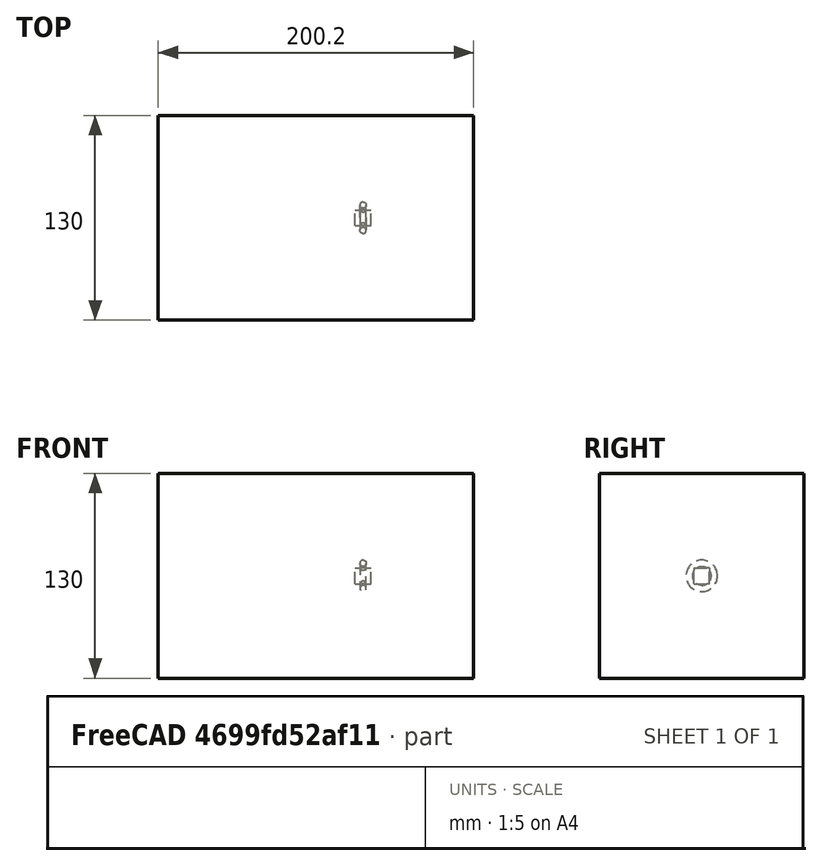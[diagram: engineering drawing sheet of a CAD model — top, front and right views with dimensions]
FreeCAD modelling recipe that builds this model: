
FCSTD DOCUMENT  (FreeCAD 0.21R33694 (Git))
Label: polarArray-7-array-rotated
License: All rights reserved
objects: App::DocumentObjectGroupPython×1251, Part::FeaturePython×4, App::Part×2, Part::MultiFuse×1
note: 4 computed .brp shape members not serialized (recipe doc carries the construction recipe); baked Part::Feature solids carry a one-line shape summary decoded from their .brp

FEATURE [App::DocumentObjectGroupPython] HALFPI  # scripted group (container) (typed FeaturePython)
  name = HALFPI
  value = pi/2.
FEATURE [App::DocumentObjectGroupPython] PI  # scripted group (container) (typed FeaturePython)
  name = PI
  value = 1.*pi
FEATURE [App::DocumentObjectGroupPython] TWOPI  # scripted group (container) (typed FeaturePython)
  name = TWOPI
  value = 2.*pi
FEATURE [App::DocumentObjectGroupPython] Constants  # scripted group (container) (typed FeaturePython)
  Group = -> [HALFPI,PI,TWOPI]
FEATURE [App::DocumentObjectGroupPython] Variables  # scripted group (container) (typed FeaturePython)
FEATURE [App::DocumentObjectGroupPython] Quantities  # scripted group (container) (typed FeaturePython)
FEATURE [App::DocumentObjectGroupPython] Isotopes  # scripted group (container) (typed FeaturePython)
FEATURE [App::DocumentObjectGroupPython] Elements  # scripted group (container) (typed FeaturePython)
FEATURE [App::DocumentObjectGroupPython] Matrix  # scripted group (container) (typed FeaturePython)
FEATURE [App::DocumentObjectGroupPython] Surfaces  # scripted group (container) (typed FeaturePython)
FEATURE [App::DocumentObjectGroupPython] Opticals  # scripted group (container) (typed FeaturePython)
  Group = -> [Matrix,Surfaces]
FEATURE [App::DocumentObjectGroupPython] G4Isotopes  # scripted group (container) (typed FeaturePython)
FEATURE [App::DocumentObjectGroupPython] H_element  # scripted group (container) (typed FeaturePython)
  Z = 1
  atom_value = 1.008
  formula = H
  name = H_element
FEATURE [App::DocumentObjectGroupPython] He_element  # scripted group (container) (typed FeaturePython)
  Z = 2
  atom_value = 4.0026
  formula = He
  name = He_element
FEATURE [App::DocumentObjectGroupPython] Li_element  # scripted group (container) (typed FeaturePython)
  Z = 3
  atom_value = 6.94
  formula = Li
  name = Li_element
FEATURE [App::DocumentObjectGroupPython] Be_element  # scripted group (container) (typed FeaturePython)
  Z = 4
  atom_value = 9.01218
  formula = Be
  name = Be_element
FEATURE [App::DocumentObjectGroupPython] B_element  # scripted group (container) (typed FeaturePython)
  Z = 5
  atom_value = 10.81
  formula = B
  name = B_element
FEATURE [App::DocumentObjectGroupPython] C_element  # scripted group (container) (typed FeaturePython)
  Z = 6
  atom_value = 12.011
  formula = C
  name = C_element
FEATURE [App::DocumentObjectGroupPython] N_element  # scripted group (container) (typed FeaturePython)
  Z = 7
  atom_value = 14.007
  formula = N
  name = N_element
FEATURE [App::DocumentObjectGroupPython] O_element  # scripted group (container) (typed FeaturePython)
  Z = 8
  atom_value = 15.999
  formula = O
  name = O_element
FEATURE [App::DocumentObjectGroupPython] F_element  # scripted group (container) (typed FeaturePython)
  Z = 9
  atom_value = 18.9984
  formula = F
  name = F_element
FEATURE [App::DocumentObjectGroupPython] Ne_element  # scripted group (container) (typed FeaturePython)
  Z = 10
  atom_value = 20.1797
  formula = Ne
  name = Ne_element
FEATURE [App::DocumentObjectGroupPython] Na_element  # scripted group (container) (typed FeaturePython)
  Z = 11
  atom_value = 22.9898
  formula = Na
  name = Na_element
FEATURE [App::DocumentObjectGroupPython] Mg_element  # scripted group (container) (typed FeaturePython)
  Z = 12
  atom_value = 24.305
  formula = Mg
  name = Mg_element
FEATURE [App::DocumentObjectGroupPython] Al_element  # scripted group (container) (typed FeaturePython)
  Z = 13
  atom_value = 26.9815
  formula = Al
  name = Al_element
FEATURE [App::DocumentObjectGroupPython] Si_element  # scripted group (container) (typed FeaturePython)
  Z = 14
  atom_value = 28.085
  formula = Si
  name = Si_element
FEATURE [App::DocumentObjectGroupPython] P_element  # scripted group (container) (typed FeaturePython)
  Z = 15
  atom_value = 30.9738
  formula = P
  name = P_element
FEATURE [App::DocumentObjectGroupPython] S_element  # scripted group (container) (typed FeaturePython)
  Z = 16
  atom_value = 32.06
  formula = S
  name = S_element
FEATURE [App::DocumentObjectGroupPython] Cl_element  # scripted group (container) (typed FeaturePython)
  Z = 17
  atom_value = 35.45
  formula = Cl
  name = Cl_element
FEATURE [App::DocumentObjectGroupPython] Ar_element  # scripted group (container) (typed FeaturePython)
  Z = 18
  atom_value = 39.95
  formula = Ar
  name = Ar_element
FEATURE [App::DocumentObjectGroupPython] K_element  # scripted group (container) (typed FeaturePython)
  Z = 19
  atom_value = 39.0983
  formula = K
  name = K_element
FEATURE [App::DocumentObjectGroupPython] Ca_element  # scripted group (container) (typed FeaturePython)
  Z = 20
  atom_value = 40.078
  formula = Ca
  name = Ca_element
FEATURE [App::DocumentObjectGroupPython] Sc_element  # scripted group (container) (typed FeaturePython)
  Z = 21
  atom_value = 44.9559
  formula = Sc
  name = Sc_element
FEATURE [App::DocumentObjectGroupPython] Ti_element  # scripted group (container) (typed FeaturePython)
  Z = 22
  atom_value = 47.867
  formula = Ti
  name = Ti_element
FEATURE [App::DocumentObjectGroupPython] V_element  # scripted group (container) (typed FeaturePython)
  Z = 23
  atom_value = 50.9415
  formula = V
  name = V_element
FEATURE [App::DocumentObjectGroupPython] Cr_element  # scripted group (container) (typed FeaturePython)
  Z = 24
  atom_value = 51.9961
  formula = Cr
  name = Cr_element
FEATURE [App::DocumentObjectGroupPython] Mn_element  # scripted group (container) (typed FeaturePython)
  Z = 25
  atom_value = 54.938
  formula = Mn
  name = Mn_element
FEATURE [App::DocumentObjectGroupPython] Fe_element  # scripted group (container) (typed FeaturePython)
  Z = 26
  atom_value = 55.845
  formula = Fe
  name = Fe_element
FEATURE [App::DocumentObjectGroupPython] Co_element  # scripted group (container) (typed FeaturePython)
  Z = 27
  atom_value = 58.9332
  formula = Co
  name = Co_element
FEATURE [App::DocumentObjectGroupPython] Ni_element  # scripted group (container) (typed FeaturePython)
  Z = 28
  atom_value = 58.6934
  formula = Ni
  name = Ni_element
FEATURE [App::DocumentObjectGroupPython] Cu_element  # scripted group (container) (typed FeaturePython)
  Z = 29
  atom_value = 63.546
  formula = Cu
  name = Cu_element
FEATURE [App::DocumentObjectGroupPython] Zn_element  # scripted group (container) (typed FeaturePython)
  Z = 30
  atom_value = 65.38
  formula = Zn
  name = Zn_element
FEATURE [App::DocumentObjectGroupPython] Ga_element  # scripted group (container) (typed FeaturePython)
  Z = 31
  atom_value = 69.723
  formula = Ga
  name = Ga_element
FEATURE [App::DocumentObjectGroupPython] Ge_element  # scripted group (container) (typed FeaturePython)
  Z = 32
  atom_value = 72.63
  formula = Ge
  name = Ge_element
FEATURE [App::DocumentObjectGroupPython] As_element  # scripted group (container) (typed FeaturePython)
  Z = 33
  atom_value = 74.9216
  formula = As
  name = As_element
FEATURE [App::DocumentObjectGroupPython] Se_element  # scripted group (container) (typed FeaturePython)
  Z = 34
  atom_value = 78.971
  formula = Se
  name = Se_element
FEATURE [App::DocumentObjectGroupPython] Br_element  # scripted group (container) (typed FeaturePython)
  Z = 35
  atom_value = 79.904
  formula = Br
  name = Br_element
FEATURE [App::DocumentObjectGroupPython] Kr_element  # scripted group (container) (typed FeaturePython)
  Z = 36
  atom_value = 83.798
  formula = Kr
  name = Kr_element
FEATURE [App::DocumentObjectGroupPython] Rb_element  # scripted group (container) (typed FeaturePython)
  Z = 37
  atom_value = 85.4678
  formula = Rb
  name = Rb_element
FEATURE [App::DocumentObjectGroupPython] Sr_element  # scripted group (container) (typed FeaturePython)
  Z = 38
  atom_value = 87.62
  formula = Sr
  name = Sr_element
FEATURE [App::DocumentObjectGroupPython] Y_element  # scripted group (container) (typed FeaturePython)
  Z = 39
  atom_value = 88.9058
  formula = Y
  name = Y_element
FEATURE [App::DocumentObjectGroupPython] Zr_element  # scripted group (container) (typed FeaturePython)
  Z = 40
  atom_value = 91.224
  formula = Zr
  name = Zr_element
FEATURE [App::DocumentObjectGroupPython] Nb_element  # scripted group (container) (typed FeaturePython)
  Z = 41
  atom_value = 92.9064
  formula = Nb
  name = Nb_element
FEATURE [App::DocumentObjectGroupPython] Mo_element  # scripted group (container) (typed FeaturePython)
  Z = 42
  atom_value = 95.95
  formula = Mo
  name = Mo_element
FEATURE [App::DocumentObjectGroupPython] Tc_element  # scripted group (container) (typed FeaturePython)
  Z = 43
  atom_value = 97
  formula = Tc
  name = Tc_element
FEATURE [App::DocumentObjectGroupPython] Ru_element  # scripted group (container) (typed FeaturePython)
  Z = 44
  atom_value = 101.07
  formula = Ru
  name = Ru_element
FEATURE [App::DocumentObjectGroupPython] Rh_element  # scripted group (container) (typed FeaturePython)
  Z = 45
  atom_value = 102.905
  formula = Rh
  name = Rh_element
FEATURE [App::DocumentObjectGroupPython] Pd_element  # scripted group (container) (typed FeaturePython)
  Z = 46
  atom_value = 106.42
  formula = Pd
  name = Pd_element
FEATURE [App::DocumentObjectGroupPython] Ag_element  # scripted group (container) (typed FeaturePython)
  Z = 47
  atom_value = 107.868
  formula = Ag
  name = Ag_element
FEATURE [App::DocumentObjectGroupPython] Cd_element  # scripted group (container) (typed FeaturePython)
  Z = 48
  atom_value = 112.414
  formula = Cd
  name = Cd_element
FEATURE [App::DocumentObjectGroupPython] In_element  # scripted group (container) (typed FeaturePython)
  Z = 49
  atom_value = 114.818
  formula = In
  name = In_element
FEATURE [App::DocumentObjectGroupPython] Sn_element  # scripted group (container) (typed FeaturePython)
  Z = 50
  atom_value = 118.71
  formula = Sn
  name = Sn_element
FEATURE [App::DocumentObjectGroupPython] Sb_element  # scripted group (container) (typed FeaturePython)
  Z = 51
  atom_value = 121.76
  formula = Sb
  name = Sb_element
FEATURE [App::DocumentObjectGroupPython] Te_element  # scripted group (container) (typed FeaturePython)
  Z = 52
  atom_value = 127.6
  formula = Te
  name = Te_element
FEATURE [App::DocumentObjectGroupPython] I_element  # scripted group (container) (typed FeaturePython)
  Z = 53
  atom_value = 126.904
  formula = I
  name = I_element
FEATURE [App::DocumentObjectGroupPython] Xe_element  # scripted group (container) (typed FeaturePython)
  Z = 54
  atom_value = 131.293
  formula = Xe
  name = Xe_element
FEATURE [App::DocumentObjectGroupPython] Cs_element  # scripted group (container) (typed FeaturePython)
  Z = 55
  atom_value = 132.905
  formula = Cs
  name = Cs_element
FEATURE [App::DocumentObjectGroupPython] Ba_element  # scripted group (container) (typed FeaturePython)
  Z = 56
  atom_value = 137.327
  formula = Ba
  name = Ba_element
FEATURE [App::DocumentObjectGroupPython] La_element  # scripted group (container) (typed FeaturePython)
  Z = 57
  atom_value = 138.905
  formula = La
  name = La_element
FEATURE [App::DocumentObjectGroupPython] Ce_element  # scripted group (container) (typed FeaturePython)
  Z = 58
  atom_value = 140.116
  formula = Ce
  name = Ce_element
FEATURE [App::DocumentObjectGroupPython] Pr_element  # scripted group (container) (typed FeaturePython)
  Z = 59
  atom_value = 140.908
  formula = Pr
  name = Pr_element
FEATURE [App::DocumentObjectGroupPython] Nd_element  # scripted group (container) (typed FeaturePython)
  Z = 60
  atom_value = 144.242
  formula = Nd
  name = Nd_element
FEATURE [App::DocumentObjectGroupPython] Pm_element  # scripted group (container) (typed FeaturePython)
  Z = 61
  atom_value = 145
  formula = Pm
  name = Pm_element
FEATURE [App::DocumentObjectGroupPython] Sm_element  # scripted group (container) (typed FeaturePython)
  Z = 62
  atom_value = 150.36
  formula = Sm
  name = Sm_element
FEATURE [App::DocumentObjectGroupPython] Eu_element  # scripted group (container) (typed FeaturePython)
  Z = 63
  atom_value = 151.964
  formula = Eu
  name = Eu_element
FEATURE [App::DocumentObjectGroupPython] Gd_element  # scripted group (container) (typed FeaturePython)
  Z = 64
  atom_value = 157.25
  formula = Gd
  name = Gd_element
FEATURE [App::DocumentObjectGroupPython] Tb_element  # scripted group (container) (typed FeaturePython)
  Z = 65
  atom_value = 158.925
  formula = Tb
  name = Tb_element
FEATURE [App::DocumentObjectGroupPython] Dy_element  # scripted group (container) (typed FeaturePython)
  Z = 66
  atom_value = 162.5
  formula = Dy
  name = Dy_element
FEATURE [App::DocumentObjectGroupPython] Ho_element  # scripted group (container) (typed FeaturePython)
  Z = 67
  atom_value = 164.93
  formula = Ho
  name = Ho_element
FEATURE [App::DocumentObjectGroupPython] Er_element  # scripted group (container) (typed FeaturePython)
  Z = 68
  atom_value = 167.259
  formula = Er
  name = Er_element
FEATURE [App::DocumentObjectGroupPython] Tm_element  # scripted group (container) (typed FeaturePython)
  Z = 69
  atom_value = 168.934
  formula = Tm
  name = Tm_element
FEATURE [App::DocumentObjectGroupPython] Yb_element  # scripted group (container) (typed FeaturePython)
  Z = 70
  atom_value = 173.045
  formula = Yb
  name = Yb_element
FEATURE [App::DocumentObjectGroupPython] Lu_element  # scripted group (container) (typed FeaturePython)
  Z = 71
  atom_value = 174.967
  formula = Lu
  name = Lu_element
FEATURE [App::DocumentObjectGroupPython] Hf_element  # scripted group (container) (typed FeaturePython)
  Z = 72
  atom_value = 178.49
  formula = Hf
  name = Hf_element
FEATURE [App::DocumentObjectGroupPython] Ta_element  # scripted group (container) (typed FeaturePython)
  Z = 73
  atom_value = 180.948
  formula = Ta
  name = Ta_element
FEATURE [App::DocumentObjectGroupPython] W_element  # scripted group (container) (typed FeaturePython)
  Z = 74
  atom_value = 183.84
  formula = W
  name = W_element
FEATURE [App::DocumentObjectGroupPython] Re_element  # scripted group (container) (typed FeaturePython)
  Z = 75
  atom_value = 186.207
  formula = Re
  name = Re_element
FEATURE [App::DocumentObjectGroupPython] Os_element  # scripted group (container) (typed FeaturePython)
  Z = 76
  atom_value = 190.23
  formula = Os
  name = Os_element
FEATURE [App::DocumentObjectGroupPython] Ir_element  # scripted group (container) (typed FeaturePython)
  Z = 77
  atom_value = 192.217
  formula = Ir
  name = Ir_element
FEATURE [App::DocumentObjectGroupPython] Pt_element  # scripted group (container) (typed FeaturePython)
  Z = 78
  atom_value = 195.084
  formula = Pt
  name = Pt_element
FEATURE [App::DocumentObjectGroupPython] Au_element  # scripted group (container) (typed FeaturePython)
  Z = 79
  atom_value = 196.967
  formula = Au
  name = Au_element
FEATURE [App::DocumentObjectGroupPython] Hg_element  # scripted group (container) (typed FeaturePython)
  Z = 80
  atom_value = 200.592
  formula = Hg
  name = Hg_element
FEATURE [App::DocumentObjectGroupPython] Tl_element  # scripted group (container) (typed FeaturePython)
  Z = 81
  atom_value = 204.38
  formula = Tl
  name = Tl_element
FEATURE [App::DocumentObjectGroupPython] Pb_element  # scripted group (container) (typed FeaturePython)
  Z = 82
  atom_value = 207.2
  formula = Pb
  name = Pb_element
FEATURE [App::DocumentObjectGroupPython] Bi_element  # scripted group (container) (typed FeaturePython)
  Z = 83
  atom_value = 208.98
  formula = Bi
  name = Bi_element
FEATURE [App::DocumentObjectGroupPython] Po_element  # scripted group (container) (typed FeaturePython)
  Z = 84
  atom_value = 209
  formula = Po
  name = Po_element
FEATURE [App::DocumentObjectGroupPython] At_element  # scripted group (container) (typed FeaturePython)
  Z = 85
  atom_value = 210
  formula = At
  name = At_element
FEATURE [App::DocumentObjectGroupPython] Rn_element  # scripted group (container) (typed FeaturePython)
  Z = 86
  atom_value = 222
  formula = Rn
  name = Rn_element
FEATURE [App::DocumentObjectGroupPython] Fr_element  # scripted group (container) (typed FeaturePython)
  Z = 87
  atom_value = 223
  formula = Fr
  name = Fr_element
FEATURE [App::DocumentObjectGroupPython] Ra_element  # scripted group (container) (typed FeaturePython)
  Z = 88
  atom_value = 226
  formula = Ra
  name = Ra_element
FEATURE [App::DocumentObjectGroupPython] Ac_element  # scripted group (container) (typed FeaturePython)
  Z = 89
  atom_value = 227
  formula = Ac
  name = Ac_element
FEATURE [App::DocumentObjectGroupPython] Th_element  # scripted group (container) (typed FeaturePython)
  Z = 90
  atom_value = 232.038
  formula = Th
  name = Th_element
FEATURE [App::DocumentObjectGroupPython] Pa_element  # scripted group (container) (typed FeaturePython)
  Z = 91
  atom_value = 231.036
  formula = Pa
  name = Pa_element
FEATURE [App::DocumentObjectGroupPython] U_element  # scripted group (container) (typed FeaturePython)
  Z = 92
  atom_value = 238.029
  formula = U
  name = U_element
FEATURE [App::DocumentObjectGroupPython] Np_element  # scripted group (container) (typed FeaturePython)
  Z = 93
  atom_value = 237
  formula = Np
  name = Np_element
FEATURE [App::DocumentObjectGroupPython] Pu_element  # scripted group (container) (typed FeaturePython)
  Z = 94
  atom_value = 244
  formula = Pu
  name = Pu_element
FEATURE [App::DocumentObjectGroupPython] Am_element  # scripted group (container) (typed FeaturePython)
  Z = 95
  atom_value = 243
  formula = Am
  name = Am_element
FEATURE [App::DocumentObjectGroupPython] Cm_element  # scripted group (container) (typed FeaturePython)
  Z = 96
  atom_value = 247
  formula = Cm
  name = Cm_element
FEATURE [App::DocumentObjectGroupPython] Bk_element  # scripted group (container) (typed FeaturePython)
  Z = 97
  atom_value = 247
  formula = Bk
  name = Bk_element
FEATURE [App::DocumentObjectGroupPython] Cf_element  # scripted group (container) (typed FeaturePython)
  Z = 98
  atom_value = 251
  formula = Cf
  name = Cf_element
FEATURE [App::DocumentObjectGroupPython] G4Elements  # scripted group (container) (typed FeaturePython)
  Group = -> [H_element,He_element,Li_element,Be_element,B_element,C_element,N_element,O_element,F_element,Ne_element,Na_element,Mg_element,Al_element,Si_element,P_element,S_element,Cl_element,Ar_element,K_element,Ca_element,Sc_element,Ti_element,V_element,Cr_element,Mn_element,Fe_element,Co_element,Ni_element,Cu_element,Zn_element,Ga_element,Ge_element,As_element,Se_element,Br_element,Kr_element,Rb_element,+61 more]
FEATURE [App::DocumentObjectGroupPython] H_element001  label="H_element : 0.101"  # scripted group (container) (typed FeaturePython)
  n = 0.101327
FEATURE [App::DocumentObjectGroupPython] C_element001  label="C_element : 0.775"  # scripted group (container) (typed FeaturePython)
  n = 0.7755
FEATURE [App::DocumentObjectGroupPython] N_element001  label="N_element : 0.035"  # scripted group (container) (typed FeaturePython)
  n = 0.035057
FEATURE [App::DocumentObjectGroupPython] O_element001  label="O_element : 0.052"  # scripted group (container) (typed FeaturePython)
  n = 0.0523159
FEATURE [App::DocumentObjectGroupPython] F_element001  label="F_element : 0.017"  # scripted group (container) (typed FeaturePython)
  n = 0.017422
FEATURE [App::DocumentObjectGroupPython] Ca_element001  label="Ca_element : 0.018"  # scripted group (container) (typed FeaturePython)
  n = 0.018378
FEATURE [App::DocumentObjectGroupPython] G4_A_150_TISSUE  label="G4_A-150_TISSUE"  # scripted group (container) (typed FeaturePython)
  Dunit = g/cm3
  Dvalue = 1.127
  Group = -> [H_element001,C_element001,N_element001,O_element001,F_element001,Ca_element001]
  conduct = 2
  density = 1
  expand = 3
  formula = G4_A-150_TISSUE
  name = G4_A-150_TISSUE
  specific = 4
FEATURE [App::DocumentObjectGroupPython] C_element002  label="C_element : 3"  # scripted group (container) (typed FeaturePython)
  n = 3
  ref = C_element
FEATURE [App::DocumentObjectGroupPython] H_element002  label="H_element : 6"  # scripted group (container) (typed FeaturePython)
  n = 6
  ref = H_element
FEATURE [App::DocumentObjectGroupPython] O_element002  label="O_element : 1"  # scripted group (container) (typed FeaturePython)
  n = 1
  ref = O_element
FEATURE [App::DocumentObjectGroupPython] G4_ACETONE  # scripted group (container) (typed FeaturePython)
  Dunit = g/cm3
  Dvalue = 0.7899
  Group = -> [C_element002,H_element002,O_element002]
  conduct = 2
  density = 1
  expand = 3
  formula = G4_ACETONE
  name = G4_ACETONE
  specific = 4
FEATURE [App::DocumentObjectGroupPython] C_element003  label="C_element : 2"  # scripted group (container) (typed FeaturePython)
  n = 2
  ref = C_element
FEATURE [App::DocumentObjectGroupPython] H_element003  label="H_element : 2"  # scripted group (container) (typed FeaturePython)
  n = 2
  ref = H_element
FEATURE [App::DocumentObjectGroupPython] G4_ACETYLENE  # scripted group (container) (typed FeaturePython)
  Dunit = g/cm3
  Dvalue = 0.0010967
  Group = -> [C_element003,H_element003]
  conduct = 2
  density = 1
  expand = 3
  formula = G4_ACETYLENE
  name = G4_ACETYLENE
  specific = 4
FEATURE [App::DocumentObjectGroupPython] C_element004  label="C_element : 5"  # scripted group (container) (typed FeaturePython)
  n = 5
  ref = C_element
FEATURE [App::DocumentObjectGroupPython] H_element004  label="H_element : 5"  # scripted group (container) (typed FeaturePython)
  n = 5
  ref = H_element
FEATURE [App::DocumentObjectGroupPython] N_element002  label="N_element : 5"  # scripted group (container) (typed FeaturePython)
  n = 5
  ref = N_element
FEATURE [App::DocumentObjectGroupPython] G4_ADENINE  # scripted group (container) (typed FeaturePython)
  Dunit = g/cm3
  Dvalue = 1.6
  Group = -> [C_element004,H_element004,N_element002]
  conduct = 2
  density = 1
  expand = 3
  formula = G4_ADENINE
  name = G4_ADENINE
  specific = 4
FEATURE [App::DocumentObjectGroupPython] H_element005  label="H_element : 0.114"  # scripted group (container) (typed FeaturePython)
  n = 0.114
FEATURE [App::DocumentObjectGroupPython] C_element005  label="C_element : 0.598"  # scripted group (container) (typed FeaturePython)
  n = 0.598
FEATURE [App::DocumentObjectGroupPython] N_element003  label="N_element : 0.007"  # scripted group (container) (typed FeaturePython)
  n = 0.007
FEATURE [App::DocumentObjectGroupPython] O_element003  label="O_element : 0.278"  # scripted group (container) (typed FeaturePython)
  n = 0.278
FEATURE [App::DocumentObjectGroupPython] Na_element001  label="Na_element : 0.001"  # scripted group (container) (typed FeaturePython)
  n = 0.001
FEATURE [App::DocumentObjectGroupPython] S_element001  label="S_element : 0.001"  # scripted group (container) (typed FeaturePython)
  n = 0.001
FEATURE [App::DocumentObjectGroupPython] Cl_element001  label="Cl_element : 0.001"  # scripted group (container) (typed FeaturePython)
  n = 0.001
FEATURE [App::DocumentObjectGroupPython] G4_ADIPOSE_TISSUE_ICRP  # scripted group (container) (typed FeaturePython)
  Dunit = g/cm3
  Dvalue = 0.95
  Group = -> [H_element005,C_element005,N_element003,O_element003,Na_element001,S_element001,Cl_element001]
  conduct = 2
  density = 1
  expand = 3
  formula = G4_ADIPOSE_TISSUE_ICRP
  name = G4_ADIPOSE_TISSUE_ICRP
  specific = 4
FEATURE [App::DocumentObjectGroupPython] C_element006  label="C_element : 0.000"  # scripted group (container) (typed FeaturePython)
  n = 0.000124
FEATURE [App::DocumentObjectGroupPython] N_element004  label="N_element : 0.755"  # scripted group (container) (typed FeaturePython)
  n = 0.755268
FEATURE [App::DocumentObjectGroupPython] O_element004  label="O_element : 0.232"  # scripted group (container) (typed FeaturePython)
  n = 0.231781
FEATURE [App::DocumentObjectGroupPython] Ar_element001  label="Ar_element : 0.013"  # scripted group (container) (typed FeaturePython)
  n = 0.012827
FEATURE [App::DocumentObjectGroupPython] G4_AIR  # scripted group (container) (typed FeaturePython)
  Dunit = g/cm3
  Dvalue = 0.00120479
  Group = -> [C_element006,N_element004,O_element004,Ar_element001]
  conduct = 2
  density = 1
  expand = 3
  formula = G4_AIR
  name = G4_AIR
  specific = 4
FEATURE [App::DocumentObjectGroupPython] C_element007  label="C_element : 006"  # scripted group (container) (typed FeaturePython)
  n = 3
  ref = C_element
FEATURE [App::DocumentObjectGroupPython] H_element006  label="H_element : 7"  # scripted group (container) (typed FeaturePython)
  n = 7
  ref = H_element
FEATURE [App::DocumentObjectGroupPython] N_element005  label="N_element : 1"  # scripted group (container) (typed FeaturePython)
  n = 1
  ref = N_element
FEATURE [App::DocumentObjectGroupPython] O_element005  label="O_element : 2"  # scripted group (container) (typed FeaturePython)
  n = 2
  ref = O_element
FEATURE [App::DocumentObjectGroupPython] G4_ALANINE  # scripted group (container) (typed FeaturePython)
  Dunit = g/cm3
  Dvalue = 1.42
  Group = -> [C_element007,H_element006,N_element005,O_element005]
  conduct = 2
  density = 1
  expand = 3
  formula = G4_ALANINE
  name = G4_ALANINE
  specific = 4
FEATURE [App::DocumentObjectGroupPython] Al_element001  label="Al_element : 2"  # scripted group (container) (typed FeaturePython)
  n = 2
  ref = Al_element
FEATURE [App::DocumentObjectGroupPython] O_element006  label="O_element : 3"  # scripted group (container) (typed FeaturePython)
  n = 3
  ref = O_element
FEATURE [App::DocumentObjectGroupPython] G4_ALUMINUM_OXIDE  # scripted group (container) (typed FeaturePython)
  Dunit = g/cm3
  Dvalue = 3.97
  Group = -> [Al_element001,O_element006]
  conduct = 2
  density = 1
  expand = 3
  formula = G4_ALUMINUM_OXIDE
  name = G4_ALUMINUM_OXIDE
  specific = 4
FEATURE [App::DocumentObjectGroupPython] H_element007  label="H_element : 0.106"  # scripted group (container) (typed FeaturePython)
  n = 0.10593
FEATURE [App::DocumentObjectGroupPython] C_element008  label="C_element : 0.789"  # scripted group (container) (typed FeaturePython)
  n = 0.788974
FEATURE [App::DocumentObjectGroupPython] O_element007  label="O_element : 0.105"  # scripted group (container) (typed FeaturePython)
  n = 0.105096
FEATURE [App::DocumentObjectGroupPython] G4_AMBER  # scripted group (container) (typed FeaturePython)
  Dunit = g/cm3
  Dvalue = 1.1
  Group = -> [H_element007,C_element008,O_element007]
  conduct = 2
  density = 1
  expand = 3
  formula = G4_AMBER
  name = G4_AMBER
  specific = 4
FEATURE [App::DocumentObjectGroupPython] N_element006  label="N_element : 006"  # scripted group (container) (typed FeaturePython)
  n = 1
  ref = N_element
FEATURE [App::DocumentObjectGroupPython] H_element008  label="H_element : 3"  # scripted group (container) (typed FeaturePython)
  n = 3
  ref = H_element
FEATURE [App::DocumentObjectGroupPython] G4_AMMONIA  # scripted group (container) (typed FeaturePython)
  Dunit = g/cm3
  Dvalue = 0.000826019
  Group = -> [N_element006,H_element008]
  conduct = 2
  density = 1
  expand = 3
  formula = G4_AMMONIA
  name = G4_AMMONIA
  specific = 4
FEATURE [App::DocumentObjectGroupPython] C_element009  label="C_element : 6"  # scripted group (container) (typed FeaturePython)
  n = 6
  ref = C_element
FEATURE [App::DocumentObjectGroupPython] H_element009  label="H_element : 008"  # scripted group (container) (typed FeaturePython)
  n = 7
  ref = H_element
FEATURE [App::DocumentObjectGroupPython] N_element007  label="N_element : 007"  # scripted group (container) (typed FeaturePython)
  n = 1
  ref = N_element
FEATURE [App::DocumentObjectGroupPython] G4_ANILINE  # scripted group (container) (typed FeaturePython)
  Dunit = g/cm3
  Dvalue = 1.0235
  Group = -> [C_element009,H_element009,N_element007]
  conduct = 2
  density = 1
  expand = 3
  formula = G4_ANILINE
  name = G4_ANILINE
  specific = 4
FEATURE [App::DocumentObjectGroupPython] C_element010  label="C_element : 14"  # scripted group (container) (typed FeaturePython)
  n = 14
  ref = C_element
FEATURE [App::DocumentObjectGroupPython] H_element010  label="H_element : 10"  # scripted group (container) (typed FeaturePython)
  n = 10
  ref = H_element
FEATURE [App::DocumentObjectGroupPython] G4_ANTHRACENE  # scripted group (container) (typed FeaturePython)
  Dunit = g/cm3
  Dvalue = 1.283
  Group = -> [C_element010,H_element010]
  conduct = 2
  density = 1
  expand = 3
  formula = G4_ANTHRACENE
  name = G4_ANTHRACENE
  specific = 4
FEATURE [App::DocumentObjectGroupPython] H_element011  label="H_element : 0.065"  # scripted group (container) (typed FeaturePython)
  n = 0.0654709
FEATURE [App::DocumentObjectGroupPython] C_element011  label="C_element : 0.537"  # scripted group (container) (typed FeaturePython)
  n = 0.536944
FEATURE [App::DocumentObjectGroupPython] N_element008  label="N_element : 0.021"  # scripted group (container) (typed FeaturePython)
  n = 0.0215
FEATURE [App::DocumentObjectGroupPython] O_element008  label="O_element : 0.032"  # scripted group (container) (typed FeaturePython)
  n = 0.032085
FEATURE [App::DocumentObjectGroupPython] F_element002  label="F_element : 0.167"  # scripted group (container) (typed FeaturePython)
  n = 0.167411
FEATURE [App::DocumentObjectGroupPython] Ca_element002  label="Ca_element : 0.177"  # scripted group (container) (typed FeaturePython)
  n = 0.176589
FEATURE [App::DocumentObjectGroupPython] G4_B_100_BONE  label="G4_B-100_BONE"  # scripted group (container) (typed FeaturePython)
  Dunit = g/cm3
  Dvalue = 1.45
  Group = -> [H_element011,C_element011,N_element008,O_element008,F_element002,Ca_element002]
  conduct = 2
  density = 1
  expand = 3
  formula = G4_B-100_BONE
  name = G4_B-100_BONE
  specific = 4
FEATURE [App::DocumentObjectGroupPython] H_element012  label="H_element : 0.057"  # scripted group (container) (typed FeaturePython)
  n = 0.057441
FEATURE [App::DocumentObjectGroupPython] C_element012  label="C_element : 0.790"  # scripted group (container) (typed FeaturePython)
  n = 0.774591
FEATURE [App::DocumentObjectGroupPython] O_element009  label="O_element : 0.168"  # scripted group (container) (typed FeaturePython)
  n = 0.167968
FEATURE [App::DocumentObjectGroupPython] G4_BAKELITE  # scripted group (container) (typed FeaturePython)
  Dunit = g/cm3
  Dvalue = 1.25
  Group = -> [H_element012,C_element012,O_element009]
  conduct = 2
  density = 1
  expand = 3
  formula = G4_BAKELITE
  name = G4_BAKELITE
  specific = 4
FEATURE [App::DocumentObjectGroupPython] Ba_element001  label="Ba_element : 1"  # scripted group (container) (typed FeaturePython)
  n = 1
  ref = Ba_element
FEATURE [App::DocumentObjectGroupPython] F_element003  label="F_element : 2"  # scripted group (container) (typed FeaturePython)
  n = 2
  ref = F_element
FEATURE [App::DocumentObjectGroupPython] G4_BARIUM_FLUORIDE  # scripted group (container) (typed FeaturePython)
  Dunit = g/cm3
  Dvalue = 4.89
  Group = -> [Ba_element001,F_element003]
  conduct = 2
  density = 1
  expand = 3
  formula = G4_BARIUM_FLUORIDE
  name = G4_BARIUM_FLUORIDE
  specific = 4
FEATURE [App::DocumentObjectGroupPython] Ba_element002  label="Ba_element : 002"  # scripted group (container) (typed FeaturePython)
  n = 1
  ref = Ba_element
FEATURE [App::DocumentObjectGroupPython] S_element002  label="S_element : 1"  # scripted group (container) (typed FeaturePython)
  n = 1
  ref = S_element
FEATURE [App::DocumentObjectGroupPython] O_element010  label="O_element : 4"  # scripted group (container) (typed FeaturePython)
  n = 4
  ref = O_element
FEATURE [App::DocumentObjectGroupPython] G4_BARIUM_SULFATE  # scripted group (container) (typed FeaturePython)
  Dunit = g/cm3
  Dvalue = 4.5
  Group = -> [Ba_element002,S_element002,O_element010]
  conduct = 2
  density = 1
  expand = 3
  formula = G4_BARIUM_SULFATE
  name = G4_BARIUM_SULFATE
  specific = 4
FEATURE [App::DocumentObjectGroupPython] C_element013  label="C_element : 007"  # scripted group (container) (typed FeaturePython)
  n = 6
  ref = C_element
FEATURE [App::DocumentObjectGroupPython] H_element013  label="H_element : 009"  # scripted group (container) (typed FeaturePython)
  n = 6
  ref = H_element
FEATURE [App::DocumentObjectGroupPython] G4_BENZENE  # scripted group (container) (typed FeaturePython)
  Dunit = g/cm3
  Dvalue = 0.87865
  Group = -> [C_element013,H_element013]
  conduct = 2
  density = 1
  expand = 3
  formula = G4_BENZENE
  name = G4_BENZENE
  specific = 4
FEATURE [App::DocumentObjectGroupPython] Be_element001  label="Be_element : 1"  # scripted group (container) (typed FeaturePython)
  n = 1
  ref = Be_element
FEATURE [App::DocumentObjectGroupPython] O_element011  label="O_element : 005"  # scripted group (container) (typed FeaturePython)
  n = 1
  ref = O_element
FEATURE [App::DocumentObjectGroupPython] G4_BERYLLIUM_OXIDE  # scripted group (container) (typed FeaturePython)
  Dunit = g/cm3
  Dvalue = 3.01
  Group = -> [Be_element001,O_element011]
  conduct = 2
  density = 1
  expand = 3
  formula = G4_BERYLLIUM_OXIDE
  name = G4_BERYLLIUM_OXIDE
  specific = 4
FEATURE [App::DocumentObjectGroupPython] Bi_element001  label="Bi_element : 4"  # scripted group (container) (typed FeaturePython)
  n = 4
  ref = Bi_element
FEATURE [App::DocumentObjectGroupPython] Ge_element001  label="Ge_element : 3"  # scripted group (container) (typed FeaturePython)
  n = 3
  ref = Ge_element
FEATURE [App::DocumentObjectGroupPython] O_element012  label="O_element : 12"  # scripted group (container) (typed FeaturePython)
  n = 12
  ref = O_element
FEATURE [App::DocumentObjectGroupPython] G4_BGO  # scripted group (container) (typed FeaturePython)
  Dunit = g/cm3
  Dvalue = 7.13
  Group = -> [Bi_element001,Ge_element001,O_element012]
  conduct = 2
  density = 1
  expand = 3
  formula = G4_BGO
  name = G4_BGO
  specific = 4
FEATURE [App::DocumentObjectGroupPython] H_element014  label="H_element : 0.102"  # scripted group (container) (typed FeaturePython)
  n = 0.102
FEATURE [App::DocumentObjectGroupPython] C_element014  label="C_element : 0.110"  # scripted group (container) (typed FeaturePython)
  n = 0.11
FEATURE [App::DocumentObjectGroupPython] N_element009  label="N_element : 0.033"  # scripted group (container) (typed FeaturePython)
  n = 0.033
FEATURE [App::DocumentObjectGroupPython] O_element013  label="O_element : 0.745"  # scripted group (container) (typed FeaturePython)
  n = 0.745
FEATURE [App::DocumentObjectGroupPython] Na_element002  label="Na_element : 0.002"  # scripted group (container) (typed FeaturePython)
  n = 0.001
FEATURE [App::DocumentObjectGroupPython] P_element001  label="P_element : 0.001"  # scripted group (container) (typed FeaturePython)
  n = 0.001
FEATURE [App::DocumentObjectGroupPython] S_element003  label="S_element : 0.002"  # scripted group (container) (typed FeaturePython)
  n = 0.002
FEATURE [App::DocumentObjectGroupPython] Cl_element002  label="Cl_element : 0.003"  # scripted group (container) (typed FeaturePython)
  n = 0.003
FEATURE [App::DocumentObjectGroupPython] K_element001  label="K_element : 0.002"  # scripted group (container) (typed FeaturePython)
  n = 0.002
FEATURE [App::DocumentObjectGroupPython] Fe_element001  label="Fe_element : 0.001"  # scripted group (container) (typed FeaturePython)
  n = 0.001
FEATURE [App::DocumentObjectGroupPython] G4_BLOOD_ICRP  # scripted group (container) (typed FeaturePython)
  Dunit = g/cm3
  Dvalue = 1.06
  Group = -> [H_element014,C_element014,N_element009,O_element013,Na_element002,P_element001,S_element003,Cl_element002,K_element001,Fe_element001]
  conduct = 2
  density = 1
  expand = 3
  formula = G4_BLOOD_ICRP
  name = G4_BLOOD_ICRP
  specific = 4
FEATURE [App::DocumentObjectGroupPython] H_element015  label="H_element : 0.064"  # scripted group (container) (typed FeaturePython)
  n = 0.064
FEATURE [App::DocumentObjectGroupPython] C_element015  label="C_element : 0.278"  # scripted group (container) (typed FeaturePython)
  n = 0.278
FEATURE [App::DocumentObjectGroupPython] N_element010  label="N_element : 0.027"  # scripted group (container) (typed FeaturePython)
  n = 0.027
FEATURE [App::DocumentObjectGroupPython] O_element014  label="O_element : 0.410"  # scripted group (container) (typed FeaturePython)
  n = 0.41
FEATURE [App::DocumentObjectGroupPython] Mg_element001  label="Mg_element : 0.002"  # scripted group (container) (typed FeaturePython)
  n = 0.002
FEATURE [App::DocumentObjectGroupPython] P_element002  label="P_element : 0.070"  # scripted group (container) (typed FeaturePython)
  n = 0.07
FEATURE [App::DocumentObjectGroupPython] S_element004  label="S_element : 0.003"  # scripted group (container) (typed FeaturePython)
  n = 0.002
FEATURE [App::DocumentObjectGroupPython] Ca_element003  label="Ca_element : 0.147"  # scripted group (container) (typed FeaturePython)
  n = 0.147
FEATURE [App::DocumentObjectGroupPython] G4_BONE_COMPACT_ICRU  # scripted group (container) (typed FeaturePython)
  Dunit = g/cm3
  Dvalue = 1.85
  Group = -> [H_element015,C_element015,N_element010,O_element014,Mg_element001,P_element002,S_element004,Ca_element003]
  conduct = 2
  density = 1
  expand = 3
  formula = G4_BONE_COMPACT_ICRU
  name = G4_BONE_COMPACT_ICRU
  specific = 4
FEATURE [App::DocumentObjectGroupPython] H_element016  label="H_element : 0.034"  # scripted group (container) (typed FeaturePython)
  n = 0.034
FEATURE [App::DocumentObjectGroupPython] C_element016  label="C_element : 0.155"  # scripted group (container) (typed FeaturePython)
  n = 0.155
FEATURE [App::DocumentObjectGroupPython] N_element011  label="N_element : 0.042"  # scripted group (container) (typed FeaturePython)
  n = 0.042
FEATURE [App::DocumentObjectGroupPython] O_element015  label="O_element : 0.435"  # scripted group (container) (typed FeaturePython)
  n = 0.435
FEATURE [App::DocumentObjectGroupPython] Na_element003  label="Na_element : 0.003"  # scripted group (container) (typed FeaturePython)
  n = 0.001
FEATURE [App::DocumentObjectGroupPython] Mg_element002  label="Mg_element : 0.003"  # scripted group (container) (typed FeaturePython)
  n = 0.002
FEATURE [App::DocumentObjectGroupPython] P_element003  label="P_element : 0.103"  # scripted group (container) (typed FeaturePython)
  n = 0.103
FEATURE [App::DocumentObjectGroupPython] S_element005  label="S_element : 0.004"  # scripted group (container) (typed FeaturePython)
  n = 0.003
FEATURE [App::DocumentObjectGroupPython] Ca_element004  label="Ca_element : 0.225"  # scripted group (container) (typed FeaturePython)
  n = 0.225
FEATURE [App::DocumentObjectGroupPython] G4_BONE_CORTICAL_ICRP  # scripted group (container) (typed FeaturePython)
  Dunit = g/cm3
  Dvalue = 1.92
  Group = -> [H_element016,C_element016,N_element011,O_element015,Na_element003,Mg_element002,P_element003,S_element005,Ca_element004]
  conduct = 2
  density = 1
  expand = 3
  formula = G4_BONE_CORTICAL_ICRP
  name = G4_BONE_CORTICAL_ICRP
  specific = 4
FEATURE [App::DocumentObjectGroupPython] B_element001  label="B_element : 4"  # scripted group (container) (typed FeaturePython)
  n = 4
  ref = B_element
FEATURE [App::DocumentObjectGroupPython] C_element017  label="C_element : 1"  # scripted group (container) (typed FeaturePython)
  n = 1
  ref = C_element
FEATURE [App::DocumentObjectGroupPython] G4_BORON_CARBIDE  # scripted group (container) (typed FeaturePython)
  Dunit = g/cm3
  Dvalue = 2.52
  Group = -> [B_element001,C_element017]
  conduct = 2
  density = 1
  expand = 3
  formula = G4_BORON_CARBIDE
  name = G4_BORON_CARBIDE
  specific = 4
FEATURE [App::DocumentObjectGroupPython] B_element002  label="B_element : 2"  # scripted group (container) (typed FeaturePython)
  n = 2
  ref = B_element
FEATURE [App::DocumentObjectGroupPython] O_element016  label="O_element : 006"  # scripted group (container) (typed FeaturePython)
  n = 3
  ref = O_element
FEATURE [App::DocumentObjectGroupPython] G4_BORON_OXIDE  # scripted group (container) (typed FeaturePython)
  Dunit = g/cm3
  Dvalue = 1.812
  Group = -> [B_element002,O_element016]
  conduct = 2
  density = 1
  expand = 3
  formula = G4_BORON_OXIDE
  name = G4_BORON_OXIDE
  specific = 4
FEATURE [App::DocumentObjectGroupPython] H_element017  label="H_element : 0.107"  # scripted group (container) (typed FeaturePython)
  n = 0.107
FEATURE [App::DocumentObjectGroupPython] C_element018  label="C_element : 0.145"  # scripted group (container) (typed FeaturePython)
  n = 0.145
FEATURE [App::DocumentObjectGroupPython] N_element012  label="N_element : 0.022"  # scripted group (container) (typed FeaturePython)
  n = 0.022
FEATURE [App::DocumentObjectGroupPython] O_element017  label="O_element : 0.712"  # scripted group (container) (typed FeaturePython)
  n = 0.712
FEATURE [App::DocumentObjectGroupPython] Na_element004  label="Na_element : 0.004"  # scripted group (container) (typed FeaturePython)
  n = 0.002
FEATURE [App::DocumentObjectGroupPython] P_element004  label="P_element : 0.004"  # scripted group (container) (typed FeaturePython)
  n = 0.004
FEATURE [App::DocumentObjectGroupPython] S_element006  label="S_element : 0.005"  # scripted group (container) (typed FeaturePython)
  n = 0.002
FEATURE [App::DocumentObjectGroupPython] Cl_element003  label="Cl_element : 0.004"  # scripted group (container) (typed FeaturePython)
  n = 0.003
FEATURE [App::DocumentObjectGroupPython] K_element002  label="K_element : 0.003"  # scripted group (container) (typed FeaturePython)
  n = 0.003
FEATURE [App::DocumentObjectGroupPython] G4_BRAIN_ICRP  # scripted group (container) (typed FeaturePython)
  Dunit = g/cm3
  Dvalue = 1.04
  Group = -> [H_element017,C_element018,N_element012,O_element017,Na_element004,P_element004,S_element006,Cl_element003,K_element002]
  conduct = 2
  density = 1
  expand = 3
  formula = G4_BRAIN_ICRP
  name = G4_BRAIN_ICRP
  specific = 4
FEATURE [App::DocumentObjectGroupPython] C_element019  label="C_element : 4"  # scripted group (container) (typed FeaturePython)
  n = 4
  ref = C_element
FEATURE [App::DocumentObjectGroupPython] H_element018  label="H_element : 010"  # scripted group (container) (typed FeaturePython)
  n = 10
  ref = H_element
FEATURE [App::DocumentObjectGroupPython] G4_BUTANE  # scripted group (container) (typed FeaturePython)
  Dunit = g/cm3
  Dvalue = 0.00249343
  Group = -> [C_element019,H_element018]
  conduct = 2
  density = 1
  expand = 3
  formula = G4_BUTANE
  name = G4_BUTANE
  specific = 4
FEATURE [App::DocumentObjectGroupPython] C_element020  label="C_element : 008"  # scripted group (container) (typed FeaturePython)
  n = 4
  ref = C_element
FEATURE [App::DocumentObjectGroupPython] H_element019  label="H_element : 011"  # scripted group (container) (typed FeaturePython)
  n = 10
  ref = H_element
FEATURE [App::DocumentObjectGroupPython] O_element018  label="O_element : 007"  # scripted group (container) (typed FeaturePython)
  n = 1
  ref = O_element
FEATURE [App::DocumentObjectGroupPython] G4_N_BUTYL_ALCOHOL  label="G4_N-BUTYL_ALCOHOL"  # scripted group (container) (typed FeaturePython)
  Dunit = g/cm3
  Dvalue = 0.8098
  Group = -> [C_element020,H_element019,O_element018]
  conduct = 2
  density = 1
  expand = 3
  formula = G4_N-BUTYL_ALCOHOL
  name = G4_N-BUTYL_ALCOHOL
  specific = 4
FEATURE [App::DocumentObjectGroupPython] H_element020  label="H_element : 0.025"  # scripted group (container) (typed FeaturePython)
  n = 0.02468
FEATURE [App::DocumentObjectGroupPython] C_element021  label="C_element : 0.502"  # scripted group (container) (typed FeaturePython)
  n = 0.501611
FEATURE [App::DocumentObjectGroupPython] O_element019  label="O_element : 0.005"  # scripted group (container) (typed FeaturePython)
  n = 0.004527
FEATURE [App::DocumentObjectGroupPython] F_element004  label="F_element : 0.465"  # scripted group (container) (typed FeaturePython)
  n = 0.465209
FEATURE [App::DocumentObjectGroupPython] Si_element001  label="Si_element : 0.004"  # scripted group (container) (typed FeaturePython)
  n = 0.003973
FEATURE [App::DocumentObjectGroupPython] G4_C_552  label="G4_C-552"  # scripted group (container) (typed FeaturePython)
  Dunit = g/cm3
  Dvalue = 1.76
  Group = -> [H_element020,C_element021,O_element019,F_element004,Si_element001]
  conduct = 2
  density = 1
  expand = 3
  formula = G4_C-552
  name = G4_C-552
  specific = 4
FEATURE [App::DocumentObjectGroupPython] Cd_element001  label="Cd_element : 1"  # scripted group (container) (typed FeaturePython)
  n = 1
  ref = Cd_element
FEATURE [App::DocumentObjectGroupPython] Te_element001  label="Te_element : 1"  # scripted group (container) (typed FeaturePython)
  n = 1
  ref = Te_element
FEATURE [App::DocumentObjectGroupPython] G4_CADMIUM_TELLURIDE  # scripted group (container) (typed FeaturePython)
  Dunit = g/cm3
  Dvalue = 6.2
  Group = -> [Cd_element001,Te_element001]
  conduct = 2
  density = 1
  expand = 3
  formula = G4_CADMIUM_TELLURIDE
  name = G4_CADMIUM_TELLURIDE
  specific = 4
FEATURE [App::DocumentObjectGroupPython] Cd_element002  label="Cd_element : 002"  # scripted group (container) (typed FeaturePython)
  n = 1
  ref = Cd_element
FEATURE [App::DocumentObjectGroupPython] W_element001  label="W_element : 1"  # scripted group (container) (typed FeaturePython)
  n = 1
  ref = W_element
FEATURE [App::DocumentObjectGroupPython] O_element020  label="O_element : 008"  # scripted group (container) (typed FeaturePython)
  n = 4
  ref = O_element
FEATURE [App::DocumentObjectGroupPython] G4_CADMIUM_TUNGSTATE  # scripted group (container) (typed FeaturePython)
  Dunit = g/cm3
  Dvalue = 7.9
  Group = -> [Cd_element002,W_element001,O_element020]
  conduct = 2
  density = 1
  expand = 3
  formula = G4_CADMIUM_TUNGSTATE
  name = G4_CADMIUM_TUNGSTATE
  specific = 4
FEATURE [App::DocumentObjectGroupPython] Ca_element005  label="Ca_element : 1"  # scripted group (container) (typed FeaturePython)
  n = 1
  ref = Ca_element
FEATURE [App::DocumentObjectGroupPython] C_element022  label="C_element : 009"  # scripted group (container) (typed FeaturePython)
  n = 1
  ref = C_element
FEATURE [App::DocumentObjectGroupPython] O_element021  label="O_element : 009"  # scripted group (container) (typed FeaturePython)
  n = 3
  ref = O_element
FEATURE [App::DocumentObjectGroupPython] G4_CALCIUM_CARBONATE  # scripted group (container) (typed FeaturePython)
  Dunit = g/cm3
  Dvalue = 2.8
  Group = -> [Ca_element005,C_element022,O_element021]
  conduct = 2
  density = 1
  expand = 3
  formula = G4_CALCIUM_CARBONATE
  name = G4_CALCIUM_CARBONATE
  specific = 4
FEATURE [App::DocumentObjectGroupPython] Ca_element006  label="Ca_element : 002"  # scripted group (container) (typed FeaturePython)
  n = 1
  ref = Ca_element
FEATURE [App::DocumentObjectGroupPython] F_element005  label="F_element : 003"  # scripted group (container) (typed FeaturePython)
  n = 2
  ref = F_element
FEATURE [App::DocumentObjectGroupPython] G4_CALCIUM_FLUORIDE  # scripted group (container) (typed FeaturePython)
  Dunit = g/cm3
  Dvalue = 3.18
  Group = -> [Ca_element006,F_element005]
  conduct = 2
  density = 1
  expand = 3
  formula = G4_CALCIUM_FLUORIDE
  name = G4_CALCIUM_FLUORIDE
  specific = 4
FEATURE [App::DocumentObjectGroupPython] Ca_element007  label="Ca_element : 003"  # scripted group (container) (typed FeaturePython)
  n = 1
  ref = Ca_element
FEATURE [App::DocumentObjectGroupPython] O_element022  label="O_element : 010"  # scripted group (container) (typed FeaturePython)
  n = 1
  ref = O_element
FEATURE [App::DocumentObjectGroupPython] G4_CALCIUM_OXIDE  # scripted group (container) (typed FeaturePython)
  Dunit = g/cm3
  Dvalue = 3.3
  Group = -> [Ca_element007,O_element022]
  conduct = 2
  density = 1
  expand = 3
  formula = G4_CALCIUM_OXIDE
  name = G4_CALCIUM_OXIDE
  specific = 4
FEATURE [App::DocumentObjectGroupPython] Ca_element008  label="Ca_element : 004"  # scripted group (container) (typed FeaturePython)
  n = 1
  ref = Ca_element
FEATURE [App::DocumentObjectGroupPython] S_element007  label="S_element : 002"  # scripted group (container) (typed FeaturePython)
  n = 1
  ref = S_element
FEATURE [App::DocumentObjectGroupPython] O_element023  label="O_element : 011"  # scripted group (container) (typed FeaturePython)
  n = 4
  ref = O_element
FEATURE [App::DocumentObjectGroupPython] G4_CALCIUM_SULFATE  # scripted group (container) (typed FeaturePython)
  Dunit = g/cm3
  Dvalue = 2.96
  Group = -> [Ca_element008,S_element007,O_element023]
  conduct = 2
  density = 1
  expand = 3
  formula = G4_CALCIUM_SULFATE
  name = G4_CALCIUM_SULFATE
  specific = 4
FEATURE [App::DocumentObjectGroupPython] Ca_element009  label="Ca_element : 005"  # scripted group (container) (typed FeaturePython)
  n = 1
  ref = Ca_element
FEATURE [App::DocumentObjectGroupPython] W_element002  label="W_element : 002"  # scripted group (container) (typed FeaturePython)
  n = 1
  ref = W_element
FEATURE [App::DocumentObjectGroupPython] O_element024  label="O_element : 012"  # scripted group (container) (typed FeaturePython)
  n = 4
  ref = O_element
FEATURE [App::DocumentObjectGroupPython] G4_CALCIUM_TUNGSTATE  # scripted group (container) (typed FeaturePython)
  Dunit = g/cm3
  Dvalue = 6.062
  Group = -> [Ca_element009,W_element002,O_element024]
  conduct = 2
  density = 1
  expand = 3
  formula = G4_CALCIUM_TUNGSTATE
  name = G4_CALCIUM_TUNGSTATE
  specific = 4
FEATURE [App::DocumentObjectGroupPython] C_element023  label="C_element : 010"  # scripted group (container) (typed FeaturePython)
  n = 1
  ref = C_element
FEATURE [App::DocumentObjectGroupPython] O_element025  label="O_element : 013"  # scripted group (container) (typed FeaturePython)
  n = 2
  ref = O_element
FEATURE [App::DocumentObjectGroupPython] G4_CARBON_DIOXIDE  # scripted group (container) (typed FeaturePython)
  Dunit = g/cm3
  Dvalue = 0.00184212
  Group = -> [C_element023,O_element025]
  conduct = 2
  density = 1
  expand = 3
  formula = G4_CARBON_DIOXIDE
  name = G4_CARBON_DIOXIDE
  specific = 4
FEATURE [App::DocumentObjectGroupPython] C_element024  label="C_element : 011"  # scripted group (container) (typed FeaturePython)
  n = 1
  ref = C_element
FEATURE [App::DocumentObjectGroupPython] Cl_element004  label="Cl_element : 4"  # scripted group (container) (typed FeaturePython)
  n = 4
  ref = Cl_element
FEATURE [App::DocumentObjectGroupPython] G4_CARBON_TETRACHLORIDE  # scripted group (container) (typed FeaturePython)
  Dunit = g/cm3
  Dvalue = 1.594
  Group = -> [C_element024,Cl_element004]
  conduct = 2
  density = 1
  expand = 3
  formula = G4_CARBON_TETRACHLORIDE
  name = G4_CARBON_TETRACHLORIDE
  specific = 4
FEATURE [App::DocumentObjectGroupPython] C_element025  label="C_element : 012"  # scripted group (container) (typed FeaturePython)
  n = 6
  ref = C_element
FEATURE [App::DocumentObjectGroupPython] H_element021  label="H_element : 012"  # scripted group (container) (typed FeaturePython)
  n = 10
  ref = H_element
FEATURE [App::DocumentObjectGroupPython] O_element026  label="O_element : 5"  # scripted group (container) (typed FeaturePython)
  n = 5
  ref = O_element
FEATURE [App::DocumentObjectGroupPython] G4_CELLULOSE_CELLOPHANE  # scripted group (container) (typed FeaturePython)
  Dunit = g/cm3
  Dvalue = 1.42
  Group = -> [C_element025,H_element021,O_element026]
  conduct = 2
  density = 1
  expand = 3
  formula = G4_CELLULOSE_CELLOPHANE
  name = G4_CELLULOSE_CELLOPHANE
  specific = 4
FEATURE [App::DocumentObjectGroupPython] H_element022  label="H_element : 0.067"  # scripted group (container) (typed FeaturePython)
  n = 0.067125
FEATURE [App::DocumentObjectGroupPython] C_element026  label="C_element : 0.545"  # scripted group (container) (typed FeaturePython)
  n = 0.545403
FEATURE [App::DocumentObjectGroupPython] O_element027  label="O_element : 0.387"  # scripted group (container) (typed FeaturePython)
  n = 0.387472
FEATURE [App::DocumentObjectGroupPython] G4_CELLULOSE_BUTYRATE  # scripted group (container) (typed FeaturePython)
  Dunit = g/cm3
  Dvalue = 1.2
  Group = -> [H_element022,C_element026,O_element027]
  conduct = 2
  density = 1
  expand = 3
  formula = G4_CELLULOSE_BUTYRATE
  name = G4_CELLULOSE_BUTYRATE
  specific = 4
FEATURE [App::DocumentObjectGroupPython] H_element023  label="H_element : 0.029"  # scripted group (container) (typed FeaturePython)
  n = 0.029216
FEATURE [App::DocumentObjectGroupPython] C_element027  label="C_element : 0.271"  # scripted group (container) (typed FeaturePython)
  n = 0.271296
FEATURE [App::DocumentObjectGroupPython] N_element013  label="N_element : 0.121"  # scripted group (container) (typed FeaturePython)
  n = 0.121276
FEATURE [App::DocumentObjectGroupPython] O_element028  label="O_element : 0.578"  # scripted group (container) (typed FeaturePython)
  n = 0.578212
FEATURE [App::DocumentObjectGroupPython] G4_CELLULOSE_NITRATE  # scripted group (container) (typed FeaturePython)
  Dunit = g/cm3
  Dvalue = 1.49
  Group = -> [H_element023,C_element027,N_element013,O_element028]
  conduct = 2
  density = 1
  expand = 3
  formula = G4_CELLULOSE_NITRATE
  name = G4_CELLULOSE_NITRATE
  specific = 4
FEATURE [App::DocumentObjectGroupPython] H_element024  label="H_element : 0.108"  # scripted group (container) (typed FeaturePython)
  n = 0.107596
FEATURE [App::DocumentObjectGroupPython] N_element014  label="N_element : 0.001"  # scripted group (container) (typed FeaturePython)
  n = 0.0008
FEATURE [App::DocumentObjectGroupPython] O_element029  label="O_element : 0.875"  # scripted group (container) (typed FeaturePython)
  n = 0.874976
FEATURE [App::DocumentObjectGroupPython] S_element008  label="S_element : 0.015"  # scripted group (container) (typed FeaturePython)
  n = 0.014627
FEATURE [App::DocumentObjectGroupPython] Ce_element001  label="Ce_element : 0.002"  # scripted group (container) (typed FeaturePython)
  n = 0.002001
FEATURE [App::DocumentObjectGroupPython] G4_CERIC_SULFATE  # scripted group (container) (typed FeaturePython)
  Dunit = g/cm3
  Dvalue = 1.03
  Group = -> [H_element024,N_element014,O_element029,S_element008,Ce_element001]
  conduct = 2
  density = 1
  expand = 3
  formula = G4_CERIC_SULFATE
  name = G4_CERIC_SULFATE
  specific = 4
FEATURE [App::DocumentObjectGroupPython] Cs_element001  label="Cs_element : 1"  # scripted group (container) (typed FeaturePython)
  n = 1
  ref = Cs_element
FEATURE [App::DocumentObjectGroupPython] F_element006  label="F_element : 1"  # scripted group (container) (typed FeaturePython)
  n = 1
  ref = F_element
FEATURE [App::DocumentObjectGroupPython] G4_CESIUM_FLUORIDE  # scripted group (container) (typed FeaturePython)
  Dunit = g/cm3
  Dvalue = 4.115
  Group = -> [Cs_element001,F_element006]
  conduct = 2
  density = 1
  expand = 3
  formula = G4_CESIUM_FLUORIDE
  name = G4_CESIUM_FLUORIDE
  specific = 4
FEATURE [App::DocumentObjectGroupPython] Cs_element002  label="Cs_element : 002"  # scripted group (container) (typed FeaturePython)
  n = 1
  ref = Cs_element
FEATURE [App::DocumentObjectGroupPython] I_element001  label="I_element : 1"  # scripted group (container) (typed FeaturePython)
  n = 1
  ref = I_element
FEATURE [App::DocumentObjectGroupPython] G4_CESIUM_IODIDE  # scripted group (container) (typed FeaturePython)
  Dunit = g/cm3
  Dvalue = 4.51
  Group = -> [Cs_element002,I_element001]
  conduct = 2
  density = 1
  expand = 3
  formula = G4_CESIUM_IODIDE
  name = G4_CESIUM_IODIDE
  specific = 4
FEATURE [App::DocumentObjectGroupPython] C_element028  label="C_element : 013"  # scripted group (container) (typed FeaturePython)
  n = 6
  ref = C_element
FEATURE [App::DocumentObjectGroupPython] H_element025  label="H_element : 013"  # scripted group (container) (typed FeaturePython)
  n = 5
  ref = H_element
FEATURE [App::DocumentObjectGroupPython] Cl_element005  label="Cl_element : 1"  # scripted group (container) (typed FeaturePython)
  n = 1
  ref = Cl_element
FEATURE [App::DocumentObjectGroupPython] G4_CHLOROBENZENE  # scripted group (container) (typed FeaturePython)
  Dunit = g/cm3
  Dvalue = 1.1058
  Group = -> [C_element028,H_element025,Cl_element005]
  conduct = 2
  density = 1
  expand = 3
  formula = G4_CHLOROBENZENE
  name = G4_CHLOROBENZENE
  specific = 4
FEATURE [App::DocumentObjectGroupPython] C_element029  label="C_element : 014"  # scripted group (container) (typed FeaturePython)
  n = 1
  ref = C_element
FEATURE [App::DocumentObjectGroupPython] H_element026  label="H_element : 1"  # scripted group (container) (typed FeaturePython)
  n = 1
  ref = H_element
FEATURE [App::DocumentObjectGroupPython] Cl_element006  label="Cl_element : 3"  # scripted group (container) (typed FeaturePython)
  n = 3
  ref = Cl_element
FEATURE [App::DocumentObjectGroupPython] G4_CHLOROFORM  # scripted group (container) (typed FeaturePython)
  Dunit = g/cm3
  Dvalue = 1.4832
  Group = -> [C_element029,H_element026,Cl_element006]
  conduct = 2
  density = 1
  expand = 3
  formula = G4_CHLOROFORM
  name = G4_CHLOROFORM
  specific = 4
FEATURE [App::DocumentObjectGroupPython] H_element027  label="H_element : 0.010"  # scripted group (container) (typed FeaturePython)
  n = 0.01
FEATURE [App::DocumentObjectGroupPython] C_element030  label="C_element : 0.001"  # scripted group (container) (typed FeaturePython)
  n = 0.001
FEATURE [App::DocumentObjectGroupPython] O_element030  label="O_element : 0.529"  # scripted group (container) (typed FeaturePython)
  n = 0.529107
FEATURE [App::DocumentObjectGroupPython] Na_element005  label="Na_element : 0.016"  # scripted group (container) (typed FeaturePython)
  n = 0.016
FEATURE [App::DocumentObjectGroupPython] Mg_element003  label="Mg_element : 0.004"  # scripted group (container) (typed FeaturePython)
  n = 0.002
FEATURE [App::DocumentObjectGroupPython] Al_element002  label="Al_element : 0.034"  # scripted group (container) (typed FeaturePython)
  n = 0.033872
FEATURE [App::DocumentObjectGroupPython] Si_element002  label="Si_element : 0.337"  # scripted group (container) (typed FeaturePython)
  n = 0.337021
FEATURE [App::DocumentObjectGroupPython] K_element003  label="K_element : 0.013"  # scripted group (container) (typed FeaturePython)
  n = 0.013
FEATURE [App::DocumentObjectGroupPython] Ca_element010  label="Ca_element : 0.044"  # scripted group (container) (typed FeaturePython)
  n = 0.044
FEATURE [App::DocumentObjectGroupPython] Fe_element002  label="Fe_element : 0.014"  # scripted group (container) (typed FeaturePython)
  n = 0.014
FEATURE [App::DocumentObjectGroupPython] G4_CONCRETE  # scripted group (container) (typed FeaturePython)
  Dunit = g/cm3
  Dvalue = 2.3
  Group = -> [H_element027,C_element030,O_element030,Na_element005,Mg_element003,Al_element002,Si_element002,K_element003,Ca_element010,Fe_element002]
  conduct = 2
  density = 1
  expand = 3
  formula = G4_CONCRETE
  name = G4_CONCRETE
  specific = 4
FEATURE [App::DocumentObjectGroupPython] C_element031  label="C_element : 015"  # scripted group (container) (typed FeaturePython)
  n = 6
  ref = C_element
FEATURE [App::DocumentObjectGroupPython] H_element028  label="H_element : 12"  # scripted group (container) (typed FeaturePython)
  n = 12
  ref = H_element
FEATURE [App::DocumentObjectGroupPython] G4_CYCLOHEXANE  # scripted group (container) (typed FeaturePython)
  Dunit = g/cm3
  Dvalue = 0.779
  Group = -> [C_element031,H_element028]
  conduct = 2
  density = 1
  expand = 3
  formula = G4_CYCLOHEXANE
  name = G4_CYCLOHEXANE
  specific = 4
FEATURE [App::DocumentObjectGroupPython] C_element032  label="C_element : 016"  # scripted group (container) (typed FeaturePython)
  n = 6
  ref = C_element
FEATURE [App::DocumentObjectGroupPython] H_element029  label="H_element : 4"  # scripted group (container) (typed FeaturePython)
  n = 4
  ref = H_element
FEATURE [App::DocumentObjectGroupPython] Cl_element007  label="Cl_element : 2"  # scripted group (container) (typed FeaturePython)
  n = 2
  ref = Cl_element
FEATURE [App::DocumentObjectGroupPython] G4_1_2_DICHLOROBENZENE  label="G4_1.2-DICHLOROBENZENE"  # scripted group (container) (typed FeaturePython)
  Dunit = g/cm3
  Dvalue = 1.3048
  Group = -> [C_element032,H_element029,Cl_element007]
  conduct = 2
  density = 1
  expand = 3
  formula = G4_1.2-DICHLOROBENZENE
  name = G4_1.2-DICHLOROBENZENE
  specific = 4
FEATURE [App::DocumentObjectGroupPython] C_element033  label="C_element : 017"  # scripted group (container) (typed FeaturePython)
  n = 4
  ref = C_element
FEATURE [App::DocumentObjectGroupPython] H_element030  label="H_element : 8"  # scripted group (container) (typed FeaturePython)
  n = 8
  ref = H_element
FEATURE [App::DocumentObjectGroupPython] O_element031  label="O_element : 014"  # scripted group (container) (typed FeaturePython)
  n = 1
  ref = O_element
FEATURE [App::DocumentObjectGroupPython] Cl_element008  label="Cl_element : 005"  # scripted group (container) (typed FeaturePython)
  n = 2
  ref = Cl_element
FEATURE [App::DocumentObjectGroupPython] G4_DICHLORODIETHYL_ETHER  # scripted group (container) (typed FeaturePython)
  Dunit = g/cm3
  Dvalue = 1.2199
  Group = -> [C_element033,H_element030,O_element031,Cl_element008]
  conduct = 2
  density = 1
  expand = 3
  formula = G4_DICHLORODIETHYL_ETHER
  name = G4_DICHLORODIETHYL_ETHER
  specific = 4
FEATURE [App::DocumentObjectGroupPython] C_element034  label="C_element : 018"  # scripted group (container) (typed FeaturePython)
  n = 2
  ref = C_element
FEATURE [App::DocumentObjectGroupPython] H_element031  label="H_element : 014"  # scripted group (container) (typed FeaturePython)
  n = 4
  ref = H_element
FEATURE [App::DocumentObjectGroupPython] Cl_element009  label="Cl_element : 006"  # scripted group (container) (typed FeaturePython)
  n = 2
  ref = Cl_element
FEATURE [App::DocumentObjectGroupPython] G4_1_2_DICHLOROETHANE  label="G4_1.2-DICHLOROETHANE"  # scripted group (container) (typed FeaturePython)
  Dunit = g/cm3
  Dvalue = 1.2351
  Group = -> [C_element034,H_element031,Cl_element009]
  conduct = 2
  density = 1
  expand = 3
  formula = G4_1.2-DICHLOROETHANE
  name = G4_1.2-DICHLOROETHANE
  specific = 4
FEATURE [App::DocumentObjectGroupPython] C_element035  label="C_element : 019"  # scripted group (container) (typed FeaturePython)
  n = 4
  ref = C_element
FEATURE [App::DocumentObjectGroupPython] H_element032  label="H_element : 015"  # scripted group (container) (typed FeaturePython)
  n = 10
  ref = H_element
FEATURE [App::DocumentObjectGroupPython] O_element032  label="O_element : 015"  # scripted group (container) (typed FeaturePython)
  n = 1
  ref = O_element
FEATURE [App::DocumentObjectGroupPython] G4_DIETHYL_ETHER  # scripted group (container) (typed FeaturePython)
  Dunit = g/cm3
  Dvalue = 0.71378
  Group = -> [C_element035,H_element032,O_element032]
  conduct = 2
  density = 1
  expand = 3
  formula = G4_DIETHYL_ETHER
  name = G4_DIETHYL_ETHER
  specific = 4
FEATURE [App::DocumentObjectGroupPython] C_element036  label="C_element : 020"  # scripted group (container) (typed FeaturePython)
  n = 3
  ref = C_element
FEATURE [App::DocumentObjectGroupPython] H_element033  label="H_element : 016"  # scripted group (container) (typed FeaturePython)
  n = 7
  ref = H_element
FEATURE [App::DocumentObjectGroupPython] N_element015  label="N_element : 008"  # scripted group (container) (typed FeaturePython)
  n = 1
  ref = N_element
FEATURE [App::DocumentObjectGroupPython] O_element033  label="O_element : 016"  # scripted group (container) (typed FeaturePython)
  n = 1
  ref = O_element
FEATURE [App::DocumentObjectGroupPython] G4_N_N_DIMETHYL_FORMAMIDE  label="G4_N.N-DIMETHYL_FORMAMIDE"  # scripted group (container) (typed FeaturePython)
  Dunit = g/cm3
  Dvalue = 0.9487
  Group = -> [C_element036,H_element033,N_element015,O_element033]
  conduct = 2
  density = 1
  expand = 3
  formula = G4_N.N-DIMETHYL_FORMAMIDE
  name = G4_N.N-DIMETHYL_FORMAMIDE
  specific = 4
FEATURE [App::DocumentObjectGroupPython] C_element037  label="C_element : 021"  # scripted group (container) (typed FeaturePython)
  n = 2
  ref = C_element
FEATURE [App::DocumentObjectGroupPython] H_element034  label="H_element : 017"  # scripted group (container) (typed FeaturePython)
  n = 6
  ref = H_element
FEATURE [App::DocumentObjectGroupPython] O_element034  label="O_element : 017"  # scripted group (container) (typed FeaturePython)
  n = 1
  ref = O_element
FEATURE [App::DocumentObjectGroupPython] S_element009  label="S_element : 003"  # scripted group (container) (typed FeaturePython)
  n = 1
  ref = S_element
FEATURE [App::DocumentObjectGroupPython] G4_DIMETHYL_SULFOXIDE  # scripted group (container) (typed FeaturePython)
  Dunit = g/cm3
  Dvalue = 1.1014
  Group = -> [C_element037,H_element034,O_element034,S_element009]
  conduct = 2
  density = 1
  expand = 3
  formula = G4_DIMETHYL_SULFOXIDE
  name = G4_DIMETHYL_SULFOXIDE
  specific = 4
FEATURE [App::DocumentObjectGroupPython] C_element038  label="C_element : 022"  # scripted group (container) (typed FeaturePython)
  n = 2
  ref = C_element
FEATURE [App::DocumentObjectGroupPython] H_element035  label="H_element : 018"  # scripted group (container) (typed FeaturePython)
  n = 6
  ref = H_element
FEATURE [App::DocumentObjectGroupPython] G4_ETHANE  # scripted group (container) (typed FeaturePython)
  Dunit = g/cm3
  Dvalue = 0.00125324
  Group = -> [C_element038,H_element035]
  conduct = 2
  density = 1
  expand = 3
  formula = G4_ETHANE
  name = G4_ETHANE
  specific = 4
FEATURE [App::DocumentObjectGroupPython] C_element039  label="C_element : 023"  # scripted group (container) (typed FeaturePython)
  n = 2
  ref = C_element
FEATURE [App::DocumentObjectGroupPython] H_element036  label="H_element : 019"  # scripted group (container) (typed FeaturePython)
  n = 6
  ref = H_element
FEATURE [App::DocumentObjectGroupPython] O_element035  label="O_element : 018"  # scripted group (container) (typed FeaturePython)
  n = 1
  ref = O_element
FEATURE [App::DocumentObjectGroupPython] G4_ETHYL_ALCOHOL  # scripted group (container) (typed FeaturePython)
  Dunit = g/cm3
  Dvalue = 0.7893
  Group = -> [C_element039,H_element036,O_element035]
  conduct = 2
  density = 1
  expand = 3
  formula = G4_ETHYL_ALCOHOL
  name = G4_ETHYL_ALCOHOL
  specific = 4
FEATURE [App::DocumentObjectGroupPython] H_element037  label="H_element : 0.090"  # scripted group (container) (typed FeaturePython)
  n = 0.090027
FEATURE [App::DocumentObjectGroupPython] C_element040  label="C_element : 0.585"  # scripted group (container) (typed FeaturePython)
  n = 0.585182
FEATURE [App::DocumentObjectGroupPython] O_element036  label="O_element : 0.325"  # scripted group (container) (typed FeaturePython)
  n = 0.324791
FEATURE [App::DocumentObjectGroupPython] G4_ETHYL_CELLULOSE  # scripted group (container) (typed FeaturePython)
  Dunit = g/cm3
  Dvalue = 1.13
  Group = -> [H_element037,C_element040,O_element036]
  conduct = 2
  density = 1
  expand = 3
  formula = G4_ETHYL_CELLULOSE
  name = G4_ETHYL_CELLULOSE
  specific = 4
FEATURE [App::DocumentObjectGroupPython] C_element041  label="C_element : 024"  # scripted group (container) (typed FeaturePython)
  n = 2
  ref = C_element
FEATURE [App::DocumentObjectGroupPython] H_element038  label="H_element : 020"  # scripted group (container) (typed FeaturePython)
  n = 4
  ref = H_element
FEATURE [App::DocumentObjectGroupPython] G4_ETHYLENE  # scripted group (container) (typed FeaturePython)
  Dunit = g/cm3
  Dvalue = 0.00117497
  Group = -> [C_element041,H_element038]
  conduct = 2
  density = 1
  expand = 3
  formula = G4_ETHYLENE
  name = G4_ETHYLENE
  specific = 4
FEATURE [App::DocumentObjectGroupPython] H_element039  label="H_element : 0.096"  # scripted group (container) (typed FeaturePython)
  n = 0.096
FEATURE [App::DocumentObjectGroupPython] C_element042  label="C_element : 0.195"  # scripted group (container) (typed FeaturePython)
  n = 0.195
FEATURE [App::DocumentObjectGroupPython] N_element016  label="N_element : 0.057"  # scripted group (container) (typed FeaturePython)
  n = 0.057
FEATURE [App::DocumentObjectGroupPython] O_element037  label="O_element : 0.646"  # scripted group (container) (typed FeaturePython)
  n = 0.646
FEATURE [App::DocumentObjectGroupPython] Na_element006  label="Na_element : 0.017"  # scripted group (container) (typed FeaturePython)
  n = 0.001
FEATURE [App::DocumentObjectGroupPython] P_element005  label="P_element : 0.104"  # scripted group (container) (typed FeaturePython)
  n = 0.001
FEATURE [App::DocumentObjectGroupPython] S_element010  label="S_element : 0.016"  # scripted group (container) (typed FeaturePython)
  n = 0.003
FEATURE [App::DocumentObjectGroupPython] Cl_element010  label="Cl_element : 0.005"  # scripted group (container) (typed FeaturePython)
  n = 0.001
FEATURE [App::DocumentObjectGroupPython] G4_EYE_LENS_ICRP  # scripted group (container) (typed FeaturePython)
  Dunit = g/cm3
  Dvalue = 1.07
  Group = -> [H_element039,C_element042,N_element016,O_element037,Na_element006,P_element005,S_element010,Cl_element010]
  conduct = 2
  density = 1
  expand = 3
  formula = G4_EYE_LENS_ICRP
  name = G4_EYE_LENS_ICRP
  specific = 4
FEATURE [App::DocumentObjectGroupPython] Fe_element003  label="Fe_element : 2"  # scripted group (container) (typed FeaturePython)
  n = 2
  ref = Fe_element
FEATURE [App::DocumentObjectGroupPython] O_element038  label="O_element : 019"  # scripted group (container) (typed FeaturePython)
  n = 3
  ref = O_element
FEATURE [App::DocumentObjectGroupPython] G4_FERRIC_OXIDE  # scripted group (container) (typed FeaturePython)
  Dunit = g/cm3
  Dvalue = 5.2
  Group = -> [Fe_element003,O_element038]
  conduct = 2
  density = 1
  expand = 3
  formula = G4_FERRIC_OXIDE
  name = G4_FERRIC_OXIDE
  specific = 4
FEATURE [App::DocumentObjectGroupPython] Fe_element004  label="Fe_element : 1"  # scripted group (container) (typed FeaturePython)
  n = 1
  ref = Fe_element
FEATURE [App::DocumentObjectGroupPython] B_element003  label="B_element : 1"  # scripted group (container) (typed FeaturePython)
  n = 1
  ref = B_element
FEATURE [App::DocumentObjectGroupPython] G4_FERROBORIDE  # scripted group (container) (typed FeaturePython)
  Dunit = g/cm3
  Dvalue = 7.15
  Group = -> [Fe_element004,B_element003]
  conduct = 2
  density = 1
  expand = 3
  formula = G4_FERROBORIDE
  name = G4_FERROBORIDE
  specific = 4
FEATURE [App::DocumentObjectGroupPython] Fe_element005  label="Fe_element : 003"  # scripted group (container) (typed FeaturePython)
  n = 1
  ref = Fe_element
FEATURE [App::DocumentObjectGroupPython] O_element039  label="O_element : 020"  # scripted group (container) (typed FeaturePython)
  n = 1
  ref = O_element
FEATURE [App::DocumentObjectGroupPython] G4_FERROUS_OXIDE  # scripted group (container) (typed FeaturePython)
  Dunit = g/cm3
  Dvalue = 5.7
  Group = -> [Fe_element005,O_element039]
  conduct = 2
  density = 1
  expand = 3
  formula = G4_FERROUS_OXIDE
  name = G4_FERROUS_OXIDE
  specific = 4
FEATURE [App::DocumentObjectGroupPython] H_element040  label="H_element : 0.115"  # scripted group (container) (typed FeaturePython)
  n = 0.108259
FEATURE [App::DocumentObjectGroupPython] N_element017  label="N_element : 0.000"  # scripted group (container) (typed FeaturePython)
  n = 2.7e-05
FEATURE [App::DocumentObjectGroupPython] O_element040  label="O_element : 0.879"  # scripted group (container) (typed FeaturePython)
  n = 0.878636
FEATURE [App::DocumentObjectGroupPython] Na_element007  label="Na_element : 0.000"  # scripted group (container) (typed FeaturePython)
  n = 2.2e-05
FEATURE [App::DocumentObjectGroupPython] S_element011  label="S_element : 0.013"  # scripted group (container) (typed FeaturePython)
  n = 0.012968
FEATURE [App::DocumentObjectGroupPython] Cl_element011  label="Cl_element : 0.000"  # scripted group (container) (typed FeaturePython)
  n = 3.4e-05
FEATURE [App::DocumentObjectGroupPython] Fe_element006  label="Fe_element : 0.000"  # scripted group (container) (typed FeaturePython)
  n = 5.4e-05
FEATURE [App::DocumentObjectGroupPython] G4_FERROUS_SULFATE  # scripted group (container) (typed FeaturePython)
  Dunit = g/cm3
  Dvalue = 1.024
  Group = -> [H_element040,N_element017,O_element040,Na_element007,S_element011,Cl_element011,Fe_element006]
  conduct = 2
  density = 1
  expand = 3
  formula = G4_FERROUS_SULFATE
  name = G4_FERROUS_SULFATE
  specific = 4
FEATURE [App::DocumentObjectGroupPython] C_element043  label="C_element : 0.099"  # scripted group (container) (typed FeaturePython)
  n = 0.099335
FEATURE [App::DocumentObjectGroupPython] F_element007  label="F_element : 0.314"  # scripted group (container) (typed FeaturePython)
  n = 0.314247
FEATURE [App::DocumentObjectGroupPython] Cl_element012  label="Cl_element : 0.586"  # scripted group (container) (typed FeaturePython)
  n = 0.586418
FEATURE [App::DocumentObjectGroupPython] G4_FREON_12  label="G4_FREON-12"  # scripted group (container) (typed FeaturePython)
  Dunit = g/cm3
  Dvalue = 1.12
  Group = -> [C_element043,F_element007,Cl_element012]
  conduct = 2
  density = 1
  expand = 3
  formula = G4_FREON-12
  name = G4_FREON-12
  specific = 4
FEATURE [App::DocumentObjectGroupPython] C_element044  label="C_element : 0.057"  # scripted group (container) (typed FeaturePython)
  n = 0.057245
FEATURE [App::DocumentObjectGroupPython] F_element008  label="F_element : 0.181"  # scripted group (container) (typed FeaturePython)
  n = 0.181096
FEATURE [App::DocumentObjectGroupPython] Br_element001  label="Br_element : 0.762"  # scripted group (container) (typed FeaturePython)
  n = 0.761659
FEATURE [App::DocumentObjectGroupPython] G4_FREON_12B2  label="G4_FREON-12B2"  # scripted group (container) (typed FeaturePython)
  Dunit = g/cm3
  Dvalue = 1.8
  Group = -> [C_element044,F_element008,Br_element001]
  conduct = 2
  density = 1
  expand = 3
  formula = G4_FREON-12B2
  name = G4_FREON-12B2
  specific = 4
FEATURE [App::DocumentObjectGroupPython] C_element045  label="C_element : 0.115"  # scripted group (container) (typed FeaturePython)
  n = 0.114983
FEATURE [App::DocumentObjectGroupPython] F_element009  label="F_element : 0.546"  # scripted group (container) (typed FeaturePython)
  n = 0.545621
FEATURE [App::DocumentObjectGroupPython] Cl_element013  label="Cl_element : 0.339"  # scripted group (container) (typed FeaturePython)
  n = 0.339396
FEATURE [App::DocumentObjectGroupPython] G4_FREON_13  label="G4_FREON-13"  # scripted group (container) (typed FeaturePython)
  Dunit = g/cm3
  Dvalue = 0.95
  Group = -> [C_element045,F_element009,Cl_element013]
  conduct = 2
  density = 1
  expand = 3
  formula = G4_FREON-13
  name = G4_FREON-13
  specific = 4
FEATURE [App::DocumentObjectGroupPython] C_element046  label="C_element : 025"  # scripted group (container) (typed FeaturePython)
  n = 1
  ref = C_element
FEATURE [App::DocumentObjectGroupPython] F_element010  label="F_element : 3"  # scripted group (container) (typed FeaturePython)
  n = 3
  ref = F_element
FEATURE [App::DocumentObjectGroupPython] Br_element002  label="Br_element : 1"  # scripted group (container) (typed FeaturePython)
  n = 1
  ref = Br_element
FEATURE [App::DocumentObjectGroupPython] G4_FREON_13B1  label="G4_FREON-13B1"  # scripted group (container) (typed FeaturePython)
  Dunit = g/cm3
  Dvalue = 1.5
  Group = -> [C_element046,F_element010,Br_element002]
  conduct = 2
  density = 1
  expand = 3
  formula = G4_FREON-13B1
  name = G4_FREON-13B1
  specific = 4
FEATURE [App::DocumentObjectGroupPython] C_element047  label="C_element : 0.061"  # scripted group (container) (typed FeaturePython)
  n = 0.061309
FEATURE [App::DocumentObjectGroupPython] F_element011  label="F_element : 0.291"  # scripted group (container) (typed FeaturePython)
  n = 0.290924
FEATURE [App::DocumentObjectGroupPython] I_element002  label="I_element : 0.648"  # scripted group (container) (typed FeaturePython)
  n = 0.647767
FEATURE [App::DocumentObjectGroupPython] G4_FREON_13I1  label="G4_FREON-13I1"  # scripted group (container) (typed FeaturePython)
  Dunit = g/cm3
  Dvalue = 1.8
  Group = -> [C_element047,F_element011,I_element002]
  conduct = 2
  density = 1
  expand = 3
  formula = G4_FREON-13I1
  name = G4_FREON-13I1
  specific = 4
FEATURE [App::DocumentObjectGroupPython] Gd_element001  label="Gd_element : 2"  # scripted group (container) (typed FeaturePython)
  n = 2
  ref = Gd_element
FEATURE [App::DocumentObjectGroupPython] O_element041  label="O_element : 021"  # scripted group (container) (typed FeaturePython)
  n = 2
  ref = O_element
FEATURE [App::DocumentObjectGroupPython] S_element012  label="S_element : 004"  # scripted group (container) (typed FeaturePython)
  n = 1
  ref = S_element
FEATURE [App::DocumentObjectGroupPython] G4_GADOLINIUM_OXYSULFIDE  # scripted group (container) (typed FeaturePython)
  Dunit = g/cm3
  Dvalue = 7.44
  Group = -> [Gd_element001,O_element041,S_element012]
  conduct = 2
  density = 1
  expand = 3
  formula = G4_GADOLINIUM_OXYSULFIDE
  name = G4_GADOLINIUM_OXYSULFIDE
  specific = 4
FEATURE [App::DocumentObjectGroupPython] Ga_element001  label="Ga_element : 1"  # scripted group (container) (typed FeaturePython)
  n = 1
  ref = Ga_element
FEATURE [App::DocumentObjectGroupPython] As_element001  label="As_element : 1"  # scripted group (container) (typed FeaturePython)
  n = 1
  ref = As_element
FEATURE [App::DocumentObjectGroupPython] G4_GALLIUM_ARSENIDE  # scripted group (container) (typed FeaturePython)
  Dunit = g/cm3
  Dvalue = 5.31
  Group = -> [Ga_element001,As_element001]
  conduct = 2
  density = 1
  expand = 3
  formula = G4_GALLIUM_ARSENIDE
  name = G4_GALLIUM_ARSENIDE
  specific = 4
FEATURE [App::DocumentObjectGroupPython] H_element041  label="H_element : 0.081"  # scripted group (container) (typed FeaturePython)
  n = 0.08118
FEATURE [App::DocumentObjectGroupPython] C_element048  label="C_element : 0.416"  # scripted group (container) (typed FeaturePython)
  n = 0.41606
FEATURE [App::DocumentObjectGroupPython] N_element018  label="N_element : 0.111"  # scripted group (container) (typed FeaturePython)
  n = 0.11124
FEATURE [App::DocumentObjectGroupPython] O_element042  label="O_element : 0.381"  # scripted group (container) (typed FeaturePython)
  n = 0.38064
FEATURE [App::DocumentObjectGroupPython] S_element013  label="S_element : 0.011"  # scripted group (container) (typed FeaturePython)
  n = 0.01088
FEATURE [App::DocumentObjectGroupPython] G4_GEL_PHOTO_EMULSION  # scripted group (container) (typed FeaturePython)
  Dunit = g/cm3
  Dvalue = 1.2914
  Group = -> [H_element041,C_element048,N_element018,O_element042,S_element013]
  conduct = 2
  density = 1
  expand = 3
  formula = G4_GEL_PHOTO_EMULSION
  name = G4_GEL_PHOTO_EMULSION
  specific = 4
FEATURE [App::DocumentObjectGroupPython] B_element004  label="B_element : 0.040"  # scripted group (container) (typed FeaturePython)
  n = 0.0400639
FEATURE [App::DocumentObjectGroupPython] O_element043  label="O_element : 0.540"  # scripted group (container) (typed FeaturePython)
  n = 0.539561
FEATURE [App::DocumentObjectGroupPython] Na_element008  label="Na_element : 0.028"  # scripted group (container) (typed FeaturePython)
  n = 0.0281909
FEATURE [App::DocumentObjectGroupPython] Al_element003  label="Al_element : 0.012"  # scripted group (container) (typed FeaturePython)
  n = 0.011644
FEATURE [App::DocumentObjectGroupPython] Si_element003  label="Si_element : 0.377"  # scripted group (container) (typed FeaturePython)
  n = 0.377219
FEATURE [App::DocumentObjectGroupPython] K_element004  label="K_element : 0.014"  # scripted group (container) (typed FeaturePython)
  n = 0.00332099
FEATURE [App::DocumentObjectGroupPython] G4_Pyrex_Glass  # scripted group (container) (typed FeaturePython)
  Dunit = g/cm3
  Dvalue = 2.23
  Group = -> [B_element004,O_element043,Na_element008,Al_element003,Si_element003,K_element004]
  conduct = 2
  density = 1
  expand = 3
  formula = G4_Pyrex_Glass
  name = G4_Pyrex_Glass
  specific = 4
FEATURE [App::DocumentObjectGroupPython] O_element044  label="O_element : 0.156"  # scripted group (container) (typed FeaturePython)
  n = 0.156453
FEATURE [App::DocumentObjectGroupPython] Si_element004  label="Si_element : 0.081"  # scripted group (container) (typed FeaturePython)
  n = 0.080866
FEATURE [App::DocumentObjectGroupPython] Ti_element001  label="Ti_element : 0.008"  # scripted group (container) (typed FeaturePython)
  n = 0.008092
FEATURE [App::DocumentObjectGroupPython] As_element002  label="As_element : 0.003"  # scripted group (container) (typed FeaturePython)
  n = 0.002651
FEATURE [App::DocumentObjectGroupPython] Pb_element001  label="Pb_element : 0.752"  # scripted group (container) (typed FeaturePython)
  n = 0.751938
FEATURE [App::DocumentObjectGroupPython] G4_GLASS_LEAD  # scripted group (container) (typed FeaturePython)
  Dunit = g/cm3
  Dvalue = 6.22
  Group = -> [O_element044,Si_element004,Ti_element001,As_element002,Pb_element001]
  conduct = 2
  density = 1
  expand = 3
  formula = G4_GLASS_LEAD
  name = G4_GLASS_LEAD
  specific = 4
FEATURE [App::DocumentObjectGroupPython] O_element045  label="O_element : 0.460"  # scripted group (container) (typed FeaturePython)
  n = 0.4598
FEATURE [App::DocumentObjectGroupPython] Na_element009  label="Na_element : 0.096"  # scripted group (container) (typed FeaturePython)
  n = 0.0964411
FEATURE [App::DocumentObjectGroupPython] Si_element005  label="Si_element : 0.378"  # scripted group (container) (typed FeaturePython)
  n = 0.336553
FEATURE [App::DocumentObjectGroupPython] Ca_element011  label="Ca_element : 0.107"  # scripted group (container) (typed FeaturePython)
  n = 0.107205
FEATURE [App::DocumentObjectGroupPython] G4_GLASS_PLATE  # scripted group (container) (typed FeaturePython)
  Dunit = g/cm3
  Dvalue = 2.4
  Group = -> [O_element045,Na_element009,Si_element005,Ca_element011]
  conduct = 2
  density = 1
  expand = 3
  formula = G4_GLASS_PLATE
  name = G4_GLASS_PLATE
  specific = 4
FEATURE [App::DocumentObjectGroupPython] C_element049  label="C_element : 026"  # scripted group (container) (typed FeaturePython)
  n = 5
  ref = C_element
FEATURE [App::DocumentObjectGroupPython] H_element042  label="H_element : 021"  # scripted group (container) (typed FeaturePython)
  n = 10
  ref = H_element
FEATURE [App::DocumentObjectGroupPython] N_element019  label="N_element : 2"  # scripted group (container) (typed FeaturePython)
  n = 2
  ref = N_element
FEATURE [App::DocumentObjectGroupPython] O_element046  label="O_element : 022"  # scripted group (container) (typed FeaturePython)
  n = 3
  ref = O_element
FEATURE [App::DocumentObjectGroupPython] G4_GLUTAMINE  # scripted group (container) (typed FeaturePython)
  Dunit = g/cm3
  Dvalue = 1.46
  Group = -> [C_element049,H_element042,N_element019,O_element046]
  conduct = 2
  density = 1
  expand = 3
  formula = G4_GLUTAMINE
  name = G4_GLUTAMINE
  specific = 4
FEATURE [App::DocumentObjectGroupPython] C_element050  label="C_element : 027"  # scripted group (container) (typed FeaturePython)
  n = 3
  ref = C_element
FEATURE [App::DocumentObjectGroupPython] H_element043  label="H_element : 022"  # scripted group (container) (typed FeaturePython)
  n = 8
  ref = H_element
FEATURE [App::DocumentObjectGroupPython] O_element047  label="O_element : 023"  # scripted group (container) (typed FeaturePython)
  n = 3
  ref = O_element
FEATURE [App::DocumentObjectGroupPython] G4_GLYCEROL  # scripted group (container) (typed FeaturePython)
  Dunit = g/cm3
  Dvalue = 1.2613
  Group = -> [C_element050,H_element043,O_element047]
  conduct = 2
  density = 1
  expand = 3
  formula = G4_GLYCEROL
  name = G4_GLYCEROL
  specific = 4
FEATURE [App::DocumentObjectGroupPython] C_element051  label="C_element : 028"  # scripted group (container) (typed FeaturePython)
  n = 5
  ref = C_element
FEATURE [App::DocumentObjectGroupPython] H_element044  label="H_element : 023"  # scripted group (container) (typed FeaturePython)
  n = 5
  ref = H_element
FEATURE [App::DocumentObjectGroupPython] N_element020  label="N_element : 009"  # scripted group (container) (typed FeaturePython)
  n = 5
  ref = N_element
FEATURE [App::DocumentObjectGroupPython] O_element048  label="O_element : 024"  # scripted group (container) (typed FeaturePython)
  n = 1
  ref = O_element
FEATURE [App::DocumentObjectGroupPython] G4_GUANINE  # scripted group (container) (typed FeaturePython)
  Dunit = g/cm3
  Dvalue = 2.2
  Group = -> [C_element051,H_element044,N_element020,O_element048]
  conduct = 2
  density = 1
  expand = 3
  formula = G4_GUANINE
  name = G4_GUANINE
  specific = 4
FEATURE [App::DocumentObjectGroupPython] Ca_element012  label="Ca_element : 006"  # scripted group (container) (typed FeaturePython)
  n = 1
  ref = Ca_element
FEATURE [App::DocumentObjectGroupPython] S_element014  label="S_element : 005"  # scripted group (container) (typed FeaturePython)
  n = 1
  ref = S_element
FEATURE [App::DocumentObjectGroupPython] O_element049  label="O_element : 6"  # scripted group (container) (typed FeaturePython)
  n = 6
  ref = O_element
FEATURE [App::DocumentObjectGroupPython] H_element045  label="H_element : 024"  # scripted group (container) (typed FeaturePython)
  n = 4
  ref = H_element
FEATURE [App::DocumentObjectGroupPython] G4_GYPSUM  # scripted group (container) (typed FeaturePython)
  Dunit = g/cm3
  Dvalue = 2.32
  Group = -> [Ca_element012,S_element014,O_element049,H_element045]
  conduct = 2
  density = 1
  expand = 3
  formula = G4_GYPSUM
  name = G4_GYPSUM
  specific = 4
FEATURE [App::DocumentObjectGroupPython] C_element052  label="C_element : 7"  # scripted group (container) (typed FeaturePython)
  n = 7
  ref = C_element
FEATURE [App::DocumentObjectGroupPython] H_element046  label="H_element : 16"  # scripted group (container) (typed FeaturePython)
  n = 16
  ref = H_element
FEATURE [App::DocumentObjectGroupPython] G4_N_HEPTANE  label="G4_N-HEPTANE"  # scripted group (container) (typed FeaturePython)
  Dunit = g/cm3
  Dvalue = 0.68376
  Group = -> [C_element052,H_element046]
  conduct = 2
  density = 1
  expand = 3
  formula = G4_N-HEPTANE
  name = G4_N-HEPTANE
  specific = 4
FEATURE [App::DocumentObjectGroupPython] C_element053  label="C_element : 029"  # scripted group (container) (typed FeaturePython)
  n = 6
  ref = C_element
FEATURE [App::DocumentObjectGroupPython] H_element047  label="H_element : 14"  # scripted group (container) (typed FeaturePython)
  n = 14
  ref = H_element
FEATURE [App::DocumentObjectGroupPython] G4_N_HEXANE  label="G4_N-HEXANE"  # scripted group (container) (typed FeaturePython)
  Dunit = g/cm3
  Dvalue = 0.6603
  Group = -> [C_element053,H_element047]
  conduct = 2
  density = 1
  expand = 3
  formula = G4_N-HEXANE
  name = G4_N-HEXANE
  specific = 4
FEATURE [App::DocumentObjectGroupPython] C_element054  label="C_element : 22"  # scripted group (container) (typed FeaturePython)
  n = 22
  ref = C_element
FEATURE [App::DocumentObjectGroupPython] H_element048  label="H_element : 025"  # scripted group (container) (typed FeaturePython)
  n = 10
  ref = H_element
FEATURE [App::DocumentObjectGroupPython] N_element021  label="N_element : 010"  # scripted group (container) (typed FeaturePython)
  n = 2
  ref = N_element
FEATURE [App::DocumentObjectGroupPython] O_element050  label="O_element : 025"  # scripted group (container) (typed FeaturePython)
  n = 5
  ref = O_element
FEATURE [App::DocumentObjectGroupPython] G4_KAPTON  # scripted group (container) (typed FeaturePython)
  Dunit = g/cm3
  Dvalue = 1.42
  Group = -> [C_element054,H_element048,N_element021,O_element050]
  conduct = 2
  density = 1
  expand = 3
  formula = G4_KAPTON
  name = G4_KAPTON
  specific = 4
FEATURE [App::DocumentObjectGroupPython] La_element001  label="La_element : 1"  # scripted group (container) (typed FeaturePython)
  n = 1
  ref = La_element
FEATURE [App::DocumentObjectGroupPython] Br_element003  label="Br_element : 002"  # scripted group (container) (typed FeaturePython)
  n = 1
  ref = Br_element
FEATURE [App::DocumentObjectGroupPython] O_element051  label="O_element : 026"  # scripted group (container) (typed FeaturePython)
  n = 1
  ref = O_element
FEATURE [App::DocumentObjectGroupPython] G4_LANTHANUM_OXYBROMIDE  # scripted group (container) (typed FeaturePython)
  Dunit = g/cm3
  Dvalue = 6.28
  Group = -> [La_element001,Br_element003,O_element051]
  conduct = 2
  density = 1
  expand = 3
  formula = G4_LANTHANUM_OXYBROMIDE
  name = G4_LANTHANUM_OXYBROMIDE
  specific = 4
FEATURE [App::DocumentObjectGroupPython] La_element002  label="La_element : 2"  # scripted group (container) (typed FeaturePython)
  n = 2
  ref = La_element
FEATURE [App::DocumentObjectGroupPython] O_element052  label="O_element : 027"  # scripted group (container) (typed FeaturePython)
  n = 2
  ref = O_element
FEATURE [App::DocumentObjectGroupPython] S_element015  label="S_element : 006"  # scripted group (container) (typed FeaturePython)
  n = 1
  ref = S_element
FEATURE [App::DocumentObjectGroupPython] G4_LANTHANUM_OXYSULFIDE  # scripted group (container) (typed FeaturePython)
  Dunit = g/cm3
  Dvalue = 5.86
  Group = -> [La_element002,O_element052,S_element015]
  conduct = 2
  density = 1
  expand = 3
  formula = G4_LANTHANUM_OXYSULFIDE
  name = G4_LANTHANUM_OXYSULFIDE
  specific = 4
FEATURE [App::DocumentObjectGroupPython] O_element053  label="O_element : 0.072"  # scripted group (container) (typed FeaturePython)
  n = 0.071682
FEATURE [App::DocumentObjectGroupPython] Pb_element002  label="Pb_element : 0.928"  # scripted group (container) (typed FeaturePython)
  n = 0.928318
FEATURE [App::DocumentObjectGroupPython] G4_LEAD_OXIDE  # scripted group (container) (typed FeaturePython)
  Dunit = g/cm3
  Dvalue = 9.53
  Group = -> [O_element053,Pb_element002]
  conduct = 2
  density = 1
  expand = 3
  formula = G4_LEAD_OXIDE
  name = G4_LEAD_OXIDE
  specific = 4
FEATURE [App::DocumentObjectGroupPython] Li_element001  label="Li_element : 1"  # scripted group (container) (typed FeaturePython)
  n = 1
  ref = Li_element
FEATURE [App::DocumentObjectGroupPython] N_element022  label="N_element : 011"  # scripted group (container) (typed FeaturePython)
  n = 1
  ref = N_element
FEATURE [App::DocumentObjectGroupPython] H_element049  label="H_element : 026"  # scripted group (container) (typed FeaturePython)
  n = 2
  ref = H_element
FEATURE [App::DocumentObjectGroupPython] G4_LITHIUM_AMIDE  # scripted group (container) (typed FeaturePython)
  Dunit = g/cm3
  Dvalue = 1.178
  Group = -> [Li_element001,N_element022,H_element049]
  conduct = 2
  density = 1
  expand = 3
  formula = G4_LITHIUM_AMIDE
  name = G4_LITHIUM_AMIDE
  specific = 4
FEATURE [App::DocumentObjectGroupPython] Li_element002  label="Li_element : 2"  # scripted group (container) (typed FeaturePython)
  n = 2
  ref = Li_element
FEATURE [App::DocumentObjectGroupPython] C_element055  label="C_element : 030"  # scripted group (container) (typed FeaturePython)
  n = 1
  ref = C_element
FEATURE [App::DocumentObjectGroupPython] O_element054  label="O_element : 028"  # scripted group (container) (typed FeaturePython)
  n = 3
  ref = O_element
FEATURE [App::DocumentObjectGroupPython] G4_LITHIUM_CARBONATE  # scripted group (container) (typed FeaturePython)
  Dunit = g/cm3
  Dvalue = 2.11
  Group = -> [Li_element002,C_element055,O_element054]
  conduct = 2
  density = 1
  expand = 3
  formula = G4_LITHIUM_CARBONATE
  name = G4_LITHIUM_CARBONATE
  specific = 4
FEATURE [App::DocumentObjectGroupPython] Li_element003  label="Li_element : 003"  # scripted group (container) (typed FeaturePython)
  n = 1
  ref = Li_element
FEATURE [App::DocumentObjectGroupPython] F_element012  label="F_element : 004"  # scripted group (container) (typed FeaturePython)
  n = 1
  ref = F_element
FEATURE [App::DocumentObjectGroupPython] G4_LITHIUM_FLUORIDE  # scripted group (container) (typed FeaturePython)
  Dunit = g/cm3
  Dvalue = 2.635
  Group = -> [Li_element003,F_element012]
  conduct = 2
  density = 1
  expand = 3
  formula = G4_LITHIUM_FLUORIDE
  name = G4_LITHIUM_FLUORIDE
  specific = 4
FEATURE [App::DocumentObjectGroupPython] Li_element004  label="Li_element : 004"  # scripted group (container) (typed FeaturePython)
  n = 1
  ref = Li_element
FEATURE [App::DocumentObjectGroupPython] H_element050  label="H_element : 027"  # scripted group (container) (typed FeaturePython)
  n = 1
  ref = H_element
FEATURE [App::DocumentObjectGroupPython] G4_LITHIUM_HYDRIDE  # scripted group (container) (typed FeaturePython)
  Dunit = g/cm3
  Dvalue = 0.82
  Group = -> [Li_element004,H_element050]
  conduct = 2
  density = 1
  expand = 3
  formula = G4_LITHIUM_HYDRIDE
  name = G4_LITHIUM_HYDRIDE
  specific = 4
FEATURE [App::DocumentObjectGroupPython] Li_element005  label="Li_element : 005"  # scripted group (container) (typed FeaturePython)
  n = 1
  ref = Li_element
FEATURE [App::DocumentObjectGroupPython] I_element003  label="I_element : 002"  # scripted group (container) (typed FeaturePython)
  n = 1
  ref = I_element
FEATURE [App::DocumentObjectGroupPython] G4_LITHIUM_IODIDE  # scripted group (container) (typed FeaturePython)
  Dunit = g/cm3
  Dvalue = 3.494
  Group = -> [Li_element005,I_element003]
  conduct = 2
  density = 1
  expand = 3
  formula = G4_LITHIUM_IODIDE
  name = G4_LITHIUM_IODIDE
  specific = 4
FEATURE [App::DocumentObjectGroupPython] Li_element006  label="Li_element : 006"  # scripted group (container) (typed FeaturePython)
  n = 2
  ref = Li_element
FEATURE [App::DocumentObjectGroupPython] O_element055  label="O_element : 029"  # scripted group (container) (typed FeaturePython)
  n = 1
  ref = O_element
FEATURE [App::DocumentObjectGroupPython] G4_LITHIUM_OXIDE  # scripted group (container) (typed FeaturePython)
  Dunit = g/cm3
  Dvalue = 2.013
  Group = -> [Li_element006,O_element055]
  conduct = 2
  density = 1
  expand = 3
  formula = G4_LITHIUM_OXIDE
  name = G4_LITHIUM_OXIDE
  specific = 4
FEATURE [App::DocumentObjectGroupPython] Li_element007  label="Li_element : 007"  # scripted group (container) (typed FeaturePython)
  n = 2
  ref = Li_element
FEATURE [App::DocumentObjectGroupPython] B_element005  label="B_element : 005"  # scripted group (container) (typed FeaturePython)
  n = 4
  ref = B_element
FEATURE [App::DocumentObjectGroupPython] O_element056  label="O_element : 7"  # scripted group (container) (typed FeaturePython)
  n = 7
  ref = O_element
FEATURE [App::DocumentObjectGroupPython] G4_LITHIUM_TETRABORATE  # scripted group (container) (typed FeaturePython)
  Dunit = g/cm3
  Dvalue = 2.44
  Group = -> [Li_element007,B_element005,O_element056]
  conduct = 2
  density = 1
  expand = 3
  formula = G4_LITHIUM_TETRABORATE
  name = G4_LITHIUM_TETRABORATE
  specific = 4
FEATURE [App::DocumentObjectGroupPython] H_element051  label="H_element : 0.105"  # scripted group (container) (typed FeaturePython)
  n = 0.105
FEATURE [App::DocumentObjectGroupPython] C_element056  label="C_element : 0.083"  # scripted group (container) (typed FeaturePython)
  n = 0.083
FEATURE [App::DocumentObjectGroupPython] N_element023  label="N_element : 0.023"  # scripted group (container) (typed FeaturePython)
  n = 0.023
FEATURE [App::DocumentObjectGroupPython] O_element057  label="O_element : 0.779"  # scripted group (container) (typed FeaturePython)
  n = 0.779
FEATURE [App::DocumentObjectGroupPython] Na_element010  label="Na_element : 0.097"  # scripted group (container) (typed FeaturePython)
  n = 0.002
FEATURE [App::DocumentObjectGroupPython] P_element006  label="P_element : 0.105"  # scripted group (container) (typed FeaturePython)
  n = 0.001
FEATURE [App::DocumentObjectGroupPython] S_element016  label="S_element : 0.017"  # scripted group (container) (typed FeaturePython)
  n = 0.002
FEATURE [App::DocumentObjectGroupPython] Cl_element014  label="Cl_element : 0.587"  # scripted group (container) (typed FeaturePython)
  n = 0.003
FEATURE [App::DocumentObjectGroupPython] K_element005  label="K_element : 0.015"  # scripted group (container) (typed FeaturePython)
  n = 0.002
FEATURE [App::DocumentObjectGroupPython] G4_LUNG_ICRP  # scripted group (container) (typed FeaturePython)
  Dunit = g/cm3
  Dvalue = 1.04
  Group = -> [H_element051,C_element056,N_element023,O_element057,Na_element010,P_element006,S_element016,Cl_element014,K_element005]
  conduct = 2
  density = 1
  expand = 3
  formula = G4_LUNG_ICRP
  name = G4_LUNG_ICRP
  specific = 4
FEATURE [App::DocumentObjectGroupPython] H_element052  label="H_element : 0.116"  # scripted group (container) (typed FeaturePython)
  n = 0.114318
FEATURE [App::DocumentObjectGroupPython] C_element057  label="C_element : 0.656"  # scripted group (container) (typed FeaturePython)
  n = 0.655824
FEATURE [App::DocumentObjectGroupPython] O_element058  label="O_element : 0.092"  # scripted group (container) (typed FeaturePython)
  n = 0.0921831
FEATURE [App::DocumentObjectGroupPython] Mg_element004  label="Mg_element : 0.135"  # scripted group (container) (typed FeaturePython)
  n = 0.134792
FEATURE [App::DocumentObjectGroupPython] Ca_element013  label="Ca_element : 0.003"  # scripted group (container) (typed FeaturePython)
  n = 0.002883
FEATURE [App::DocumentObjectGroupPython] G4_M3_WAX  # scripted group (container) (typed FeaturePython)
  Dunit = g/cm3
  Dvalue = 1.05
  Group = -> [H_element052,C_element057,O_element058,Mg_element004,Ca_element013]
  conduct = 2
  density = 1
  expand = 3
  formula = G4_M3_WAX
  name = G4_M3_WAX
  specific = 4
FEATURE [App::DocumentObjectGroupPython] Mg_element005  label="Mg_element : 1"  # scripted group (container) (typed FeaturePython)
  n = 1
  ref = Mg_element
FEATURE [App::DocumentObjectGroupPython] C_element058  label="C_element : 031"  # scripted group (container) (typed FeaturePython)
  n = 1
  ref = C_element
FEATURE [App::DocumentObjectGroupPython] O_element059  label="O_element : 030"  # scripted group (container) (typed FeaturePython)
  n = 3
  ref = O_element
FEATURE [App::DocumentObjectGroupPython] G4_MAGNESIUM_CARBONATE  # scripted group (container) (typed FeaturePython)
  Dunit = g/cm3
  Dvalue = 2.958
  Group = -> [Mg_element005,C_element058,O_element059]
  conduct = 2
  density = 1
  expand = 3
  formula = G4_MAGNESIUM_CARBONATE
  name = G4_MAGNESIUM_CARBONATE
  specific = 4
FEATURE [App::DocumentObjectGroupPython] Mg_element006  label="Mg_element : 002"  # scripted group (container) (typed FeaturePython)
  n = 1
  ref = Mg_element
FEATURE [App::DocumentObjectGroupPython] F_element013  label="F_element : 005"  # scripted group (container) (typed FeaturePython)
  n = 2
  ref = F_element
FEATURE [App::DocumentObjectGroupPython] G4_MAGNESIUM_FLUORIDE  # scripted group (container) (typed FeaturePython)
  Dunit = g/cm3
  Dvalue = 3
  Group = -> [Mg_element006,F_element013]
  conduct = 2
  density = 1
  expand = 3
  formula = G4_MAGNESIUM_FLUORIDE
  name = G4_MAGNESIUM_FLUORIDE
  specific = 4
FEATURE [App::DocumentObjectGroupPython] Mg_element007  label="Mg_element : 003"  # scripted group (container) (typed FeaturePython)
  n = 1
  ref = Mg_element
FEATURE [App::DocumentObjectGroupPython] O_element060  label="O_element : 031"  # scripted group (container) (typed FeaturePython)
  n = 1
  ref = O_element
FEATURE [App::DocumentObjectGroupPython] G4_MAGNESIUM_OXIDE  # scripted group (container) (typed FeaturePython)
  Dunit = g/cm3
  Dvalue = 3.58
  Group = -> [Mg_element007,O_element060]
  conduct = 2
  density = 1
  expand = 3
  formula = G4_MAGNESIUM_OXIDE
  name = G4_MAGNESIUM_OXIDE
  specific = 4
FEATURE [App::DocumentObjectGroupPython] Mg_element008  label="Mg_element : 004"  # scripted group (container) (typed FeaturePython)
  n = 1
  ref = Mg_element
FEATURE [App::DocumentObjectGroupPython] B_element006  label="B_element : 006"  # scripted group (container) (typed FeaturePython)
  n = 4
  ref = B_element
FEATURE [App::DocumentObjectGroupPython] O_element061  label="O_element : 032"  # scripted group (container) (typed FeaturePython)
  n = 7
  ref = O_element
FEATURE [App::DocumentObjectGroupPython] G4_MAGNESIUM_TETRABORATE  # scripted group (container) (typed FeaturePython)
  Dunit = g/cm3
  Dvalue = 2.53
  Group = -> [Mg_element008,B_element006,O_element061]
  conduct = 2
  density = 1
  expand = 3
  formula = G4_MAGNESIUM_TETRABORATE
  name = G4_MAGNESIUM_TETRABORATE
  specific = 4
FEATURE [App::DocumentObjectGroupPython] Hg_element001  label="Hg_element : 1"  # scripted group (container) (typed FeaturePython)
  n = 1
  ref = Hg_element
FEATURE [App::DocumentObjectGroupPython] I_element004  label="I_element : 2"  # scripted group (container) (typed FeaturePython)
  n = 2
  ref = I_element
FEATURE [App::DocumentObjectGroupPython] G4_MERCURIC_IODIDE  # scripted group (container) (typed FeaturePython)
  Dunit = g/cm3
  Dvalue = 6.36
  Group = -> [Hg_element001,I_element004]
  conduct = 2
  density = 1
  expand = 3
  formula = G4_MERCURIC_IODIDE
  name = G4_MERCURIC_IODIDE
  specific = 4
FEATURE [App::DocumentObjectGroupPython] C_element059  label="C_element : 032"  # scripted group (container) (typed FeaturePython)
  n = 1
  ref = C_element
FEATURE [App::DocumentObjectGroupPython] H_element053  label="H_element : 028"  # scripted group (container) (typed FeaturePython)
  n = 4
  ref = H_element
FEATURE [App::DocumentObjectGroupPython] G4_METHANE  # scripted group (container) (typed FeaturePython)
  Dunit = g/cm3
  Dvalue = 0.000667151
  Group = -> [C_element059,H_element053]
  conduct = 2
  density = 1
  expand = 3
  formula = G4_METHANE
  name = G4_METHANE
  specific = 4
FEATURE [App::DocumentObjectGroupPython] C_element060  label="C_element : 033"  # scripted group (container) (typed FeaturePython)
  n = 1
  ref = C_element
FEATURE [App::DocumentObjectGroupPython] H_element054  label="H_element : 029"  # scripted group (container) (typed FeaturePython)
  n = 4
  ref = H_element
FEATURE [App::DocumentObjectGroupPython] O_element062  label="O_element : 033"  # scripted group (container) (typed FeaturePython)
  n = 1
  ref = O_element
FEATURE [App::DocumentObjectGroupPython] G4_METHANOL  # scripted group (container) (typed FeaturePython)
  Dunit = g/cm3
  Dvalue = 0.7914
  Group = -> [C_element060,H_element054,O_element062]
  conduct = 2
  density = 1
  expand = 3
  formula = G4_METHANOL
  name = G4_METHANOL
  specific = 4
FEATURE [App::DocumentObjectGroupPython] H_element055  label="H_element : 0.134"  # scripted group (container) (typed FeaturePython)
  n = 0.13404
FEATURE [App::DocumentObjectGroupPython] C_element061  label="C_element : 0.778"  # scripted group (container) (typed FeaturePython)
  n = 0.77796
FEATURE [App::DocumentObjectGroupPython] O_element063  label="O_element : 0.035"  # scripted group (container) (typed FeaturePython)
  n = 0.03502
FEATURE [App::DocumentObjectGroupPython] Mg_element009  label="Mg_element : 0.039"  # scripted group (container) (typed FeaturePython)
  n = 0.038594
FEATURE [App::DocumentObjectGroupPython] Ti_element002  label="Ti_element : 0.014"  # scripted group (container) (typed FeaturePython)
  n = 0.014386
FEATURE [App::DocumentObjectGroupPython] G4_MIX_D_WAX  # scripted group (container) (typed FeaturePython)
  Dunit = g/cm3
  Dvalue = 0.99
  Group = -> [H_element055,C_element061,O_element063,Mg_element009,Ti_element002]
  conduct = 2
  density = 1
  expand = 3
  formula = G4_MIX_D_WAX
  name = G4_MIX_D_WAX
  specific = 4
FEATURE [App::DocumentObjectGroupPython] H_element056  label="H_element : 0.135"  # scripted group (container) (typed FeaturePython)
  n = 0.081192
FEATURE [App::DocumentObjectGroupPython] C_element062  label="C_element : 0.583"  # scripted group (container) (typed FeaturePython)
  n = 0.583442
FEATURE [App::DocumentObjectGroupPython] N_element024  label="N_element : 0.018"  # scripted group (container) (typed FeaturePython)
  n = 0.017798
FEATURE [App::DocumentObjectGroupPython] O_element064  label="O_element : 0.186"  # scripted group (container) (typed FeaturePython)
  n = 0.186381
FEATURE [App::DocumentObjectGroupPython] Mg_element010  label="Mg_element : 0.130"  # scripted group (container) (typed FeaturePython)
  n = 0.130287
FEATURE [App::DocumentObjectGroupPython] Cl_element015  label="Cl_element : 0.588"  # scripted group (container) (typed FeaturePython)
  n = 0.0009
FEATURE [App::DocumentObjectGroupPython] G4_MS20_TISSUE  # scripted group (container) (typed FeaturePython)
  Dunit = g/cm3
  Dvalue = 1
  Group = -> [H_element056,C_element062,N_element024,O_element064,Mg_element010,Cl_element015]
  conduct = 2
  density = 1
  expand = 3
  formula = G4_MS20_TISSUE
  name = G4_MS20_TISSUE
  specific = 4
FEATURE [App::DocumentObjectGroupPython] H_element057  label="H_element : 0.136"  # scripted group (container) (typed FeaturePython)
  n = 0.102
FEATURE [App::DocumentObjectGroupPython] C_element063  label="C_element : 0.143"  # scripted group (container) (typed FeaturePython)
  n = 0.143
FEATURE [App::DocumentObjectGroupPython] N_element025  label="N_element : 0.034"  # scripted group (container) (typed FeaturePython)
  n = 0.034
FEATURE [App::DocumentObjectGroupPython] O_element065  label="O_element : 0.710"  # scripted group (container) (typed FeaturePython)
  n = 0.71
FEATURE [App::DocumentObjectGroupPython] Na_element011  label="Na_element : 0.098"  # scripted group (container) (typed FeaturePython)
  n = 0.001
FEATURE [App::DocumentObjectGroupPython] P_element007  label="P_element : 0.002"  # scripted group (container) (typed FeaturePython)
  n = 0.002
FEATURE [App::DocumentObjectGroupPython] S_element017  label="S_element : 0.018"  # scripted group (container) (typed FeaturePython)
  n = 0.003
FEATURE [App::DocumentObjectGroupPython] Cl_element016  label="Cl_element : 0.589"  # scripted group (container) (typed FeaturePython)
  n = 0.001
FEATURE [App::DocumentObjectGroupPython] K_element006  label="K_element : 0.004"  # scripted group (container) (typed FeaturePython)
  n = 0.004
FEATURE [App::DocumentObjectGroupPython] G4_MUSCLE_SKELETAL_ICRP  # scripted group (container) (typed FeaturePython)
  Dunit = g/cm3
  Dvalue = 1.05
  Group = -> [H_element057,C_element063,N_element025,O_element065,Na_element011,P_element007,S_element017,Cl_element016,K_element006]
  conduct = 2
  density = 1
  expand = 3
  formula = G4_MUSCLE_SKELETAL_ICRP
  name = G4_MUSCLE_SKELETAL_ICRP
  specific = 4
FEATURE [App::DocumentObjectGroupPython] H_element058  label="H_element : 0.137"  # scripted group (container) (typed FeaturePython)
  n = 0.102102
FEATURE [App::DocumentObjectGroupPython] C_element064  label="C_element : 0.123"  # scripted group (container) (typed FeaturePython)
  n = 0.123123
FEATURE [App::DocumentObjectGroupPython] N_element026  label="N_element : 0.756"  # scripted group (container) (typed FeaturePython)
  n = 0.035035
FEATURE [App::DocumentObjectGroupPython] O_element066  label="O_element : 0.730"  # scripted group (container) (typed FeaturePython)
  n = 0.72973
FEATURE [App::DocumentObjectGroupPython] Na_element012  label="Na_element : 0.099"  # scripted group (container) (typed FeaturePython)
  n = 0.001001
FEATURE [App::DocumentObjectGroupPython] P_element008  label="P_element : 0.106"  # scripted group (container) (typed FeaturePython)
  n = 0.002002
FEATURE [App::DocumentObjectGroupPython] S_element018  label="S_element : 0.019"  # scripted group (container) (typed FeaturePython)
  n = 0.004004
FEATURE [App::DocumentObjectGroupPython] K_element007  label="K_element : 0.016"  # scripted group (container) (typed FeaturePython)
  n = 0.003003
FEATURE [App::DocumentObjectGroupPython] G4_MUSCLE_STRIATED_ICRU  # scripted group (container) (typed FeaturePython)
  Dunit = g/cm3
  Dvalue = 1.04
  Group = -> [H_element058,C_element064,N_element026,O_element066,Na_element012,P_element008,S_element018,K_element007]
  conduct = 2
  density = 1
  expand = 3
  formula = G4_MUSCLE_STRIATED_ICRU
  name = G4_MUSCLE_STRIATED_ICRU
  specific = 4
FEATURE [App::DocumentObjectGroupPython] H_element059  label="H_element : 0.098"  # scripted group (container) (typed FeaturePython)
  n = 0.0982341
FEATURE [App::DocumentObjectGroupPython] C_element065  label="C_element : 0.156"  # scripted group (container) (typed FeaturePython)
  n = 0.156214
FEATURE [App::DocumentObjectGroupPython] N_element027  label="N_element : 0.757"  # scripted group (container) (typed FeaturePython)
  n = 0.035451
FEATURE [App::DocumentObjectGroupPython] O_element067  label="O_element : 0.880"  # scripted group (container) (typed FeaturePython)
  n = 0.710101
FEATURE [App::DocumentObjectGroupPython] G4_MUSCLE_WITH_SUCROSE  # scripted group (container) (typed FeaturePython)
  Dunit = g/cm3
  Dvalue = 1.11
  Group = -> [H_element059,C_element065,N_element027,O_element067]
  conduct = 2
  density = 1
  expand = 3
  formula = G4_MUSCLE_WITH_SUCROSE
  name = G4_MUSCLE_WITH_SUCROSE
  specific = 4
FEATURE [App::DocumentObjectGroupPython] H_element060  label="H_element : 0.138"  # scripted group (container) (typed FeaturePython)
  n = 0.101969
FEATURE [App::DocumentObjectGroupPython] C_element066  label="C_element : 0.120"  # scripted group (container) (typed FeaturePython)
  n = 0.120058
FEATURE [App::DocumentObjectGroupPython] N_element028  label="N_element : 0.758"  # scripted group (container) (typed FeaturePython)
  n = 0.035451
FEATURE [App::DocumentObjectGroupPython] O_element068  label="O_element : 0.743"  # scripted group (container) (typed FeaturePython)
  n = 0.742522
FEATURE [App::DocumentObjectGroupPython] G4_MUSCLE_WITHOUT_SUCROSE  # scripted group (container) (typed FeaturePython)
  Dunit = g/cm3
  Dvalue = 1.07
  Group = -> [H_element060,C_element066,N_element028,O_element068]
  conduct = 2
  density = 1
  expand = 3
  formula = G4_MUSCLE_WITHOUT_SUCROSE
  name = G4_MUSCLE_WITHOUT_SUCROSE
  specific = 4
FEATURE [App::DocumentObjectGroupPython] C_element067  label="C_element : 10"  # scripted group (container) (typed FeaturePython)
  n = 10
  ref = C_element
FEATURE [App::DocumentObjectGroupPython] H_element061  label="H_element : 030"  # scripted group (container) (typed FeaturePython)
  n = 8
  ref = H_element
FEATURE [App::DocumentObjectGroupPython] G4_NAPHTHALENE  # scripted group (container) (typed FeaturePython)
  Dunit = g/cm3
  Dvalue = 1.145
  Group = -> [C_element067,H_element061]
  conduct = 2
  density = 1
  expand = 3
  formula = G4_NAPHTHALENE
  name = G4_NAPHTHALENE
  specific = 4
FEATURE [App::DocumentObjectGroupPython] C_element068  label="C_element : 034"  # scripted group (container) (typed FeaturePython)
  n = 6
  ref = C_element
FEATURE [App::DocumentObjectGroupPython] H_element062  label="H_element : 031"  # scripted group (container) (typed FeaturePython)
  n = 5
  ref = H_element
FEATURE [App::DocumentObjectGroupPython] N_element029  label="N_element : 012"  # scripted group (container) (typed FeaturePython)
  n = 1
  ref = N_element
FEATURE [App::DocumentObjectGroupPython] O_element069  label="O_element : 034"  # scripted group (container) (typed FeaturePython)
  n = 2
  ref = O_element
FEATURE [App::DocumentObjectGroupPython] G4_NITROBENZENE  # scripted group (container) (typed FeaturePython)
  Dunit = g/cm3
  Dvalue = 1.19867
  Group = -> [C_element068,H_element062,N_element029,O_element069]
  conduct = 2
  density = 1
  expand = 3
  formula = G4_NITROBENZENE
  name = G4_NITROBENZENE
  specific = 4
FEATURE [App::DocumentObjectGroupPython] N_element030  label="N_element : 013"  # scripted group (container) (typed FeaturePython)
  n = 2
  ref = N_element
FEATURE [App::DocumentObjectGroupPython] O_element070  label="O_element : 035"  # scripted group (container) (typed FeaturePython)
  n = 1
  ref = O_element
FEATURE [App::DocumentObjectGroupPython] G4_NITROUS_OXIDE  # scripted group (container) (typed FeaturePython)
  Dunit = g/cm3
  Dvalue = 0.00183094
  Group = -> [N_element030,O_element070]
  conduct = 2
  density = 1
  expand = 3
  formula = G4_NITROUS_OXIDE
  name = G4_NITROUS_OXIDE
  specific = 4
FEATURE [App::DocumentObjectGroupPython] H_element063  label="H_element : 0.104"  # scripted group (container) (typed FeaturePython)
  n = 0.103509
FEATURE [App::DocumentObjectGroupPython] C_element069  label="C_element : 0.648"  # scripted group (container) (typed FeaturePython)
  n = 0.648416
FEATURE [App::DocumentObjectGroupPython] N_element031  label="N_element : 0.100"  # scripted group (container) (typed FeaturePython)
  n = 0.0995361
FEATURE [App::DocumentObjectGroupPython] O_element071  label="O_element : 0.149"  # scripted group (container) (typed FeaturePython)
  n = 0.148539
FEATURE [App::DocumentObjectGroupPython] G4_NYLON_8062  label="G4_NYLON-8062"  # scripted group (container) (typed FeaturePython)
  Dunit = g/cm3
  Dvalue = 1.08
  Group = -> [H_element063,C_element069,N_element031,O_element071]
  conduct = 2
  density = 1
  expand = 3
  formula = G4_NYLON-8062
  name = G4_NYLON-8062
  specific = 4
FEATURE [App::DocumentObjectGroupPython] C_element070  label="C_element : 035"  # scripted group (container) (typed FeaturePython)
  n = 6
  ref = C_element
FEATURE [App::DocumentObjectGroupPython] H_element064  label="H_element : 11"  # scripted group (container) (typed FeaturePython)
  n = 11
  ref = H_element
FEATURE [App::DocumentObjectGroupPython] N_element032  label="N_element : 014"  # scripted group (container) (typed FeaturePython)
  n = 1
  ref = N_element
FEATURE [App::DocumentObjectGroupPython] O_element072  label="O_element : 036"  # scripted group (container) (typed FeaturePython)
  n = 1
  ref = O_element
FEATURE [App::DocumentObjectGroupPython] G4_NYLON_6_6  label="G4_NYLON-6-6"  # scripted group (container) (typed FeaturePython)
  Dunit = g/cm3
  Dvalue = 1.14
  Group = -> [C_element070,H_element064,N_element032,O_element072]
  conduct = 2
  density = 1
  expand = 3
  formula = G4_NYLON-6-6
  name = G4_NYLON-6-6
  specific = 4
FEATURE [App::DocumentObjectGroupPython] H_element065  label="H_element : 0.139"  # scripted group (container) (typed FeaturePython)
  n = 0.107062
FEATURE [App::DocumentObjectGroupPython] C_element071  label="C_element : 0.680"  # scripted group (container) (typed FeaturePython)
  n = 0.680449
FEATURE [App::DocumentObjectGroupPython] N_element033  label="N_element : 0.099"  # scripted group (container) (typed FeaturePython)
  n = 0.099189
FEATURE [App::DocumentObjectGroupPython] O_element073  label="O_element : 0.113"  # scripted group (container) (typed FeaturePython)
  n = 0.1133
FEATURE [App::DocumentObjectGroupPython] G4_NYLON_6_10  label="G4_NYLON-6-10"  # scripted group (container) (typed FeaturePython)
  Dunit = g/cm3
  Dvalue = 1.14
  Group = -> [H_element065,C_element071,N_element033,O_element073]
  conduct = 2
  density = 1
  expand = 3
  formula = G4_NYLON-6-10
  name = G4_NYLON-6-10
  specific = 4
FEATURE [App::DocumentObjectGroupPython] H_element066  label="H_element : 0.140"  # scripted group (container) (typed FeaturePython)
  n = 0.115476
FEATURE [App::DocumentObjectGroupPython] C_element072  label="C_element : 0.721"  # scripted group (container) (typed FeaturePython)
  n = 0.720818
FEATURE [App::DocumentObjectGroupPython] N_element034  label="N_element : 0.076"  # scripted group (container) (typed FeaturePython)
  n = 0.0764169
FEATURE [App::DocumentObjectGroupPython] O_element074  label="O_element : 0.087"  # scripted group (container) (typed FeaturePython)
  n = 0.0872889
FEATURE [App::DocumentObjectGroupPython] G4_NYLON_11_RILSAN  label="G4_NYLON-11_RILSAN"  # scripted group (container) (typed FeaturePython)
  Dunit = g/cm3
  Dvalue = 1.425
  Group = -> [H_element066,C_element072,N_element034,O_element074]
  conduct = 2
  density = 1
  expand = 3
  formula = G4_NYLON-11_RILSAN
  name = G4_NYLON-11_RILSAN
  specific = 4
FEATURE [App::DocumentObjectGroupPython] C_element073  label="C_element : 8"  # scripted group (container) (typed FeaturePython)
  n = 8
  ref = C_element
FEATURE [App::DocumentObjectGroupPython] H_element067  label="H_element : 18"  # scripted group (container) (typed FeaturePython)
  n = 18
  ref = H_element
FEATURE [App::DocumentObjectGroupPython] G4_OCTANE  # scripted group (container) (typed FeaturePython)
  Dunit = g/cm3
  Dvalue = 0.7026
  Group = -> [C_element073,H_element067]
  conduct = 2
  density = 1
  expand = 3
  formula = G4_OCTANE
  name = G4_OCTANE
  specific = 4
FEATURE [App::DocumentObjectGroupPython] C_element074  label="C_element : 25"  # scripted group (container) (typed FeaturePython)
  n = 25
  ref = C_element
FEATURE [App::DocumentObjectGroupPython] H_element068  label="H_element : 52"  # scripted group (container) (typed FeaturePython)
  n = 52
  ref = H_element
FEATURE [App::DocumentObjectGroupPython] G4_PARAFFIN  # scripted group (container) (typed FeaturePython)
  Dunit = g/cm3
  Dvalue = 0.93
  Group = -> [C_element074,H_element068]
  conduct = 2
  density = 1
  expand = 3
  formula = G4_PARAFFIN
  name = G4_PARAFFIN
  specific = 4
FEATURE [App::DocumentObjectGroupPython] C_element075  label="C_element : 036"  # scripted group (container) (typed FeaturePython)
  n = 5
  ref = C_element
FEATURE [App::DocumentObjectGroupPython] H_element069  label="H_element : 032"  # scripted group (container) (typed FeaturePython)
  n = 12
  ref = H_element
FEATURE [App::DocumentObjectGroupPython] G4_N_PENTANE  label="G4_N-PENTANE"  # scripted group (container) (typed FeaturePython)
  Dunit = g/cm3
  Dvalue = 0.6262
  Group = -> [C_element075,H_element069]
  conduct = 2
  density = 1
  expand = 3
  formula = G4_N-PENTANE
  name = G4_N-PENTANE
  specific = 4
FEATURE [App::DocumentObjectGroupPython] H_element070  label="H_element : 0.014"  # scripted group (container) (typed FeaturePython)
  n = 0.0141
FEATURE [App::DocumentObjectGroupPython] C_element076  label="C_element : 0.072"  # scripted group (container) (typed FeaturePython)
  n = 0.072261
FEATURE [App::DocumentObjectGroupPython] N_element035  label="N_element : 0.019"  # scripted group (container) (typed FeaturePython)
  n = 0.01932
FEATURE [App::DocumentObjectGroupPython] O_element075  label="O_element : 0.066"  # scripted group (container) (typed FeaturePython)
  n = 0.066101
FEATURE [App::DocumentObjectGroupPython] S_element019  label="S_element : 0.020"  # scripted group (container) (typed FeaturePython)
  n = 0.00189
FEATURE [App::DocumentObjectGroupPython] Br_element004  label="Br_element : 0.349"  # scripted group (container) (typed FeaturePython)
  n = 0.349103
FEATURE [App::DocumentObjectGroupPython] Ag_element001  label="Ag_element : 0.474"  # scripted group (container) (typed FeaturePython)
  n = 0.474105
FEATURE [App::DocumentObjectGroupPython] I_element005  label="I_element : 0.003"  # scripted group (container) (typed FeaturePython)
  n = 0.00312
FEATURE [App::DocumentObjectGroupPython] G4_PHOTO_EMULSION  # scripted group (container) (typed FeaturePython)
  Dunit = g/cm3
  Dvalue = 3.815
  Group = -> [H_element070,C_element076,N_element035,O_element075,S_element019,Br_element004,Ag_element001,I_element005]
  conduct = 2
  density = 1
  expand = 3
  formula = G4_PHOTO_EMULSION
  name = G4_PHOTO_EMULSION
  specific = 4
FEATURE [App::DocumentObjectGroupPython] C_element077  label="C_element : 9"  # scripted group (container) (typed FeaturePython)
  n = 9
  ref = C_element
FEATURE [App::DocumentObjectGroupPython] H_element071  label="H_element : 033"  # scripted group (container) (typed FeaturePython)
  n = 10
  ref = H_element
FEATURE [App::DocumentObjectGroupPython] G4_PLASTIC_SC_VINYLTOLUENE  # scripted group (container) (typed FeaturePython)
  Dunit = g/cm3
  Dvalue = 1.032
  Group = -> [C_element077,H_element071]
  conduct = 2
  density = 1
  expand = 3
  formula = G4_PLASTIC_SC_VINYLTOLUENE
  name = G4_PLASTIC_SC_VINYLTOLUENE
  specific = 4
FEATURE [App::DocumentObjectGroupPython] Pu_element001  label="Pu_element : 1"  # scripted group (container) (typed FeaturePython)
  n = 1
  ref = Pu_element
FEATURE [App::DocumentObjectGroupPython] O_element076  label="O_element : 037"  # scripted group (container) (typed FeaturePython)
  n = 2
  ref = O_element
FEATURE [App::DocumentObjectGroupPython] G4_PLUTONIUM_DIOXIDE  # scripted group (container) (typed FeaturePython)
  Dunit = g/cm3
  Dvalue = 11.46
  Group = -> [Pu_element001,O_element076]
  conduct = 2
  density = 1
  expand = 3
  formula = G4_PLUTONIUM_DIOXIDE
  name = G4_PLUTONIUM_DIOXIDE
  specific = 4
FEATURE [App::DocumentObjectGroupPython] C_element078  label="C_element : 037"  # scripted group (container) (typed FeaturePython)
  n = 3
  ref = C_element
FEATURE [App::DocumentObjectGroupPython] H_element072  label="H_element : 034"  # scripted group (container) (typed FeaturePython)
  n = 3
  ref = H_element
FEATURE [App::DocumentObjectGroupPython] N_element036  label="N_element : 015"  # scripted group (container) (typed FeaturePython)
  n = 1
  ref = N_element
FEATURE [App::DocumentObjectGroupPython] G4_POLYACRYLONITRILE  # scripted group (container) (typed FeaturePython)
  Dunit = g/cm3
  Dvalue = 1.17
  Group = -> [C_element078,H_element072,N_element036]
  conduct = 2
  density = 1
  expand = 3
  formula = G4_POLYACRYLONITRILE
  name = G4_POLYACRYLONITRILE
  specific = 4
FEATURE [App::DocumentObjectGroupPython] C_element079  label="C_element : 16"  # scripted group (container) (typed FeaturePython)
  n = 16
  ref = C_element
FEATURE [App::DocumentObjectGroupPython] H_element073  label="H_element : 035"  # scripted group (container) (typed FeaturePython)
  n = 14
  ref = H_element
FEATURE [App::DocumentObjectGroupPython] O_element077  label="O_element : 038"  # scripted group (container) (typed FeaturePython)
  n = 3
  ref = O_element
FEATURE [App::DocumentObjectGroupPython] G4_POLYCARBONATE  # scripted group (container) (typed FeaturePython)
  Dunit = g/cm3
  Dvalue = 1.2
  Group = -> [C_element079,H_element073,O_element077]
  conduct = 2
  density = 1
  expand = 3
  formula = G4_POLYCARBONATE
  name = G4_POLYCARBONATE
  specific = 4
FEATURE [App::DocumentObjectGroupPython] C_element080  label="C_element : 038"  # scripted group (container) (typed FeaturePython)
  n = 8
  ref = C_element
FEATURE [App::DocumentObjectGroupPython] H_element074  label="H_element : 036"  # scripted group (container) (typed FeaturePython)
  n = 7
  ref = H_element
FEATURE [App::DocumentObjectGroupPython] Cl_element017  label="Cl_element : 007"  # scripted group (container) (typed FeaturePython)
  n = 1
  ref = Cl_element
FEATURE [App::DocumentObjectGroupPython] G4_POLYCHLOROSTYRENE  # scripted group (container) (typed FeaturePython)
  Dunit = g/cm3
  Dvalue = 1.3
  Group = -> [C_element080,H_element074,Cl_element017]
  conduct = 2
  density = 1
  expand = 3
  formula = G4_POLYCHLOROSTYRENE
  name = G4_POLYCHLOROSTYRENE
  specific = 4
FEATURE [App::DocumentObjectGroupPython] C_element081  label="C_element : 039"  # scripted group (container) (typed FeaturePython)
  n = 1
  ref = C_element
FEATURE [App::DocumentObjectGroupPython] H_element075  label="H_element : 037"  # scripted group (container) (typed FeaturePython)
  n = 2
  ref = H_element
FEATURE [App::DocumentObjectGroupPython] G4_POLYETHYLENE  # scripted group (container) (typed FeaturePython)
  Dunit = g/cm3
  Dvalue = 0.94
  Group = -> [C_element081,H_element075]
  conduct = 2
  density = 1
  expand = 3
  formula = G4_POLYETHYLENE
  name = G4_POLYETHYLENE
  specific = 4
FEATURE [App::DocumentObjectGroupPython] C_element082  label="C_element : 040"  # scripted group (container) (typed FeaturePython)
  n = 10
  ref = C_element
FEATURE [App::DocumentObjectGroupPython] H_element076  label="H_element : 038"  # scripted group (container) (typed FeaturePython)
  n = 8
  ref = H_element
FEATURE [App::DocumentObjectGroupPython] O_element078  label="O_element : 039"  # scripted group (container) (typed FeaturePython)
  n = 4
  ref = O_element
FEATURE [App::DocumentObjectGroupPython] G4_MYLAR  # scripted group (container) (typed FeaturePython)
  Dunit = g/cm3
  Dvalue = 1.4
  Group = -> [C_element082,H_element076,O_element078]
  conduct = 2
  density = 1
  expand = 3
  formula = G4_MYLAR
  name = G4_MYLAR
  specific = 4
FEATURE [App::DocumentObjectGroupPython] C_element083  label="C_element : 041"  # scripted group (container) (typed FeaturePython)
  n = 5
  ref = C_element
FEATURE [App::DocumentObjectGroupPython] H_element077  label="H_element : 039"  # scripted group (container) (typed FeaturePython)
  n = 8
  ref = H_element
FEATURE [App::DocumentObjectGroupPython] O_element079  label="O_element : 040"  # scripted group (container) (typed FeaturePython)
  n = 2
  ref = O_element
FEATURE [App::DocumentObjectGroupPython] G4_PLEXIGLASS  # scripted group (container) (typed FeaturePython)
  Dunit = g/cm3
  Dvalue = 1.19
  Group = -> [C_element083,H_element077,O_element079]
  conduct = 2
  density = 1
  expand = 3
  formula = G4_PLEXIGLASS
  name = G4_PLEXIGLASS
  specific = 4
FEATURE [App::DocumentObjectGroupPython] C_element084  label="C_element : 042"  # scripted group (container) (typed FeaturePython)
  n = 1
  ref = C_element
FEATURE [App::DocumentObjectGroupPython] H_element078  label="H_element : 040"  # scripted group (container) (typed FeaturePython)
  n = 2
  ref = H_element
FEATURE [App::DocumentObjectGroupPython] O_element080  label="O_element : 041"  # scripted group (container) (typed FeaturePython)
  n = 1
  ref = O_element
FEATURE [App::DocumentObjectGroupPython] G4_POLYOXYMETHYLENE  # scripted group (container) (typed FeaturePython)
  Dunit = g/cm3
  Dvalue = 1.425
  Group = -> [C_element084,H_element078,O_element080]
  conduct = 2
  density = 1
  expand = 3
  formula = G4_POLYOXYMETHYLENE
  name = G4_POLYOXYMETHYLENE
  specific = 4
FEATURE [App::DocumentObjectGroupPython] C_element085  label="C_element : 043"  # scripted group (container) (typed FeaturePython)
  n = 2
  ref = C_element
FEATURE [App::DocumentObjectGroupPython] H_element079  label="H_element : 041"  # scripted group (container) (typed FeaturePython)
  n = 4
  ref = H_element
FEATURE [App::DocumentObjectGroupPython] G4_POLYPROPYLENE  # scripted group (container) (typed FeaturePython)
  Dunit = g/cm3
  Dvalue = 0.9
  Group = -> [C_element085,H_element079]
  conduct = 2
  density = 1
  expand = 3
  formula = G4_POLYPROPYLENE
  name = G4_POLYPROPYLENE
  specific = 4
FEATURE [App::DocumentObjectGroupPython] C_element086  label="C_element : 044"  # scripted group (container) (typed FeaturePython)
  n = 8
  ref = C_element
FEATURE [App::DocumentObjectGroupPython] H_element080  label="H_element : 042"  # scripted group (container) (typed FeaturePython)
  n = 8
  ref = H_element
FEATURE [App::DocumentObjectGroupPython] G4_POLYSTYRENE  # scripted group (container) (typed FeaturePython)
  Dunit = g/cm3
  Dvalue = 1.06
  Group = -> [C_element086,H_element080]
  conduct = 2
  density = 1
  expand = 3
  formula = G4_POLYSTYRENE
  name = G4_POLYSTYRENE
  specific = 4
FEATURE [App::DocumentObjectGroupPython] C_element087  label="C_element : 045"  # scripted group (container) (typed FeaturePython)
  n = 2
  ref = C_element
FEATURE [App::DocumentObjectGroupPython] F_element014  label="F_element : 4"  # scripted group (container) (typed FeaturePython)
  n = 4
  ref = F_element
FEATURE [App::DocumentObjectGroupPython] G4_TEFLON  # scripted group (container) (typed FeaturePython)
  Dunit = g/cm3
  Dvalue = 2.2
  Group = -> [C_element087,F_element014]
  conduct = 2
  density = 1
  expand = 3
  formula = G4_TEFLON
  name = G4_TEFLON
  specific = 4
FEATURE [App::DocumentObjectGroupPython] C_element088  label="C_element : 046"  # scripted group (container) (typed FeaturePython)
  n = 2
  ref = C_element
FEATURE [App::DocumentObjectGroupPython] F_element015  label="F_element : 006"  # scripted group (container) (typed FeaturePython)
  n = 3
  ref = F_element
FEATURE [App::DocumentObjectGroupPython] Cl_element018  label="Cl_element : 008"  # scripted group (container) (typed FeaturePython)
  n = 1
  ref = Cl_element
FEATURE [App::DocumentObjectGroupPython] G4_POLYTRIFLUOROCHLOROETHYLENE  # scripted group (container) (typed FeaturePython)
  Dunit = g/cm3
  Dvalue = 2.1
  Group = -> [C_element088,F_element015,Cl_element018]
  conduct = 2
  density = 1
  expand = 3
  formula = G4_POLYTRIFLUOROCHLOROETHYLENE
  name = G4_POLYTRIFLUOROCHLOROETHYLENE
  specific = 4
FEATURE [App::DocumentObjectGroupPython] C_element089  label="C_element : 047"  # scripted group (container) (typed FeaturePython)
  n = 4
  ref = C_element
FEATURE [App::DocumentObjectGroupPython] H_element081  label="H_element : 043"  # scripted group (container) (typed FeaturePython)
  n = 6
  ref = H_element
FEATURE [App::DocumentObjectGroupPython] O_element081  label="O_element : 042"  # scripted group (container) (typed FeaturePython)
  n = 2
  ref = O_element
FEATURE [App::DocumentObjectGroupPython] G4_POLYVINYL_ACETATE  # scripted group (container) (typed FeaturePython)
  Dunit = g/cm3
  Dvalue = 1.19
  Group = -> [C_element089,H_element081,O_element081]
  conduct = 2
  density = 1
  expand = 3
  formula = G4_POLYVINYL_ACETATE
  name = G4_POLYVINYL_ACETATE
  specific = 4
FEATURE [App::DocumentObjectGroupPython] C_element090  label="C_element : 048"  # scripted group (container) (typed FeaturePython)
  n = 2
  ref = C_element
FEATURE [App::DocumentObjectGroupPython] H_element082  label="H_element : 044"  # scripted group (container) (typed FeaturePython)
  n = 4
  ref = H_element
FEATURE [App::DocumentObjectGroupPython] O_element082  label="O_element : 043"  # scripted group (container) (typed FeaturePython)
  n = 1
  ref = O_element
FEATURE [App::DocumentObjectGroupPython] G4_POLYVINYL_ALCOHOL  # scripted group (container) (typed FeaturePython)
  Dunit = g/cm3
  Dvalue = 1.3
  Group = -> [C_element090,H_element082,O_element082]
  conduct = 2
  density = 1
  expand = 3
  formula = G4_POLYVINYL_ALCOHOL
  name = G4_POLYVINYL_ALCOHOL
  specific = 4
FEATURE [App::DocumentObjectGroupPython] C_element091  label="C_element : 049"  # scripted group (container) (typed FeaturePython)
  n = 8
  ref = C_element
FEATURE [App::DocumentObjectGroupPython] H_element083  label="H_element : 045"  # scripted group (container) (typed FeaturePython)
  n = 14
  ref = H_element
FEATURE [App::DocumentObjectGroupPython] O_element083  label="O_element : 044"  # scripted group (container) (typed FeaturePython)
  n = 2
  ref = O_element
FEATURE [App::DocumentObjectGroupPython] G4_POLYVINYL_BUTYRAL  # scripted group (container) (typed FeaturePython)
  Dunit = g/cm3
  Dvalue = 1.12
  Group = -> [C_element091,H_element083,O_element083]
  conduct = 2
  density = 1
  expand = 3
  formula = G4_POLYVINYL_BUTYRAL
  name = G4_POLYVINYL_BUTYRAL
  specific = 4
FEATURE [App::DocumentObjectGroupPython] C_element092  label="C_element : 050"  # scripted group (container) (typed FeaturePython)
  n = 2
  ref = C_element
FEATURE [App::DocumentObjectGroupPython] H_element084  label="H_element : 046"  # scripted group (container) (typed FeaturePython)
  n = 3
  ref = H_element
FEATURE [App::DocumentObjectGroupPython] Cl_element019  label="Cl_element : 009"  # scripted group (container) (typed FeaturePython)
  n = 1
  ref = Cl_element
FEATURE [App::DocumentObjectGroupPython] G4_POLYVINYL_CHLORIDE  # scripted group (container) (typed FeaturePython)
  Dunit = g/cm3
  Dvalue = 1.3
  Group = -> [C_element092,H_element084,Cl_element019]
  conduct = 2
  density = 1
  expand = 3
  formula = G4_POLYVINYL_CHLORIDE
  name = G4_POLYVINYL_CHLORIDE
  specific = 4
FEATURE [App::DocumentObjectGroupPython] C_element093  label="C_element : 051"  # scripted group (container) (typed FeaturePython)
  n = 2
  ref = C_element
FEATURE [App::DocumentObjectGroupPython] H_element085  label="H_element : 047"  # scripted group (container) (typed FeaturePython)
  n = 2
  ref = H_element
FEATURE [App::DocumentObjectGroupPython] Cl_element020  label="Cl_element : 010"  # scripted group (container) (typed FeaturePython)
  n = 2
  ref = Cl_element
FEATURE [App::DocumentObjectGroupPython] G4_POLYVINYLIDENE_CHLORIDE  # scripted group (container) (typed FeaturePython)
  Dunit = g/cm3
  Dvalue = 1.7
  Group = -> [C_element093,H_element085,Cl_element020]
  conduct = 2
  density = 1
  expand = 3
  formula = G4_POLYVINYLIDENE_CHLORIDE
  name = G4_POLYVINYLIDENE_CHLORIDE
  specific = 4
FEATURE [App::DocumentObjectGroupPython] C_element094  label="C_element : 052"  # scripted group (container) (typed FeaturePython)
  n = 2
  ref = C_element
FEATURE [App::DocumentObjectGroupPython] H_element086  label="H_element : 048"  # scripted group (container) (typed FeaturePython)
  n = 2
  ref = H_element
FEATURE [App::DocumentObjectGroupPython] F_element016  label="F_element : 007"  # scripted group (container) (typed FeaturePython)
  n = 2
  ref = F_element
FEATURE [App::DocumentObjectGroupPython] G4_POLYVINYLIDENE_FLUORIDE  # scripted group (container) (typed FeaturePython)
  Dunit = g/cm3
  Dvalue = 1.76
  Group = -> [C_element094,H_element086,F_element016]
  conduct = 2
  density = 1
  expand = 3
  formula = G4_POLYVINYLIDENE_FLUORIDE
  name = G4_POLYVINYLIDENE_FLUORIDE
  specific = 4
FEATURE [App::DocumentObjectGroupPython] C_element095  label="C_element : 053"  # scripted group (container) (typed FeaturePython)
  n = 6
  ref = C_element
FEATURE [App::DocumentObjectGroupPython] H_element087  label="H_element : 9"  # scripted group (container) (typed FeaturePython)
  n = 9
  ref = H_element
FEATURE [App::DocumentObjectGroupPython] N_element037  label="N_element : 016"  # scripted group (container) (typed FeaturePython)
  n = 1
  ref = N_element
FEATURE [App::DocumentObjectGroupPython] O_element084  label="O_element : 045"  # scripted group (container) (typed FeaturePython)
  n = 1
  ref = O_element
FEATURE [App::DocumentObjectGroupPython] G4_POLYVINYL_PYRROLIDONE  # scripted group (container) (typed FeaturePython)
  Dunit = g/cm3
  Dvalue = 1.25
  Group = -> [C_element095,H_element087,N_element037,O_element084]
  conduct = 2
  density = 1
  expand = 3
  formula = G4_POLYVINYL_PYRROLIDONE
  name = G4_POLYVINYL_PYRROLIDONE
  specific = 4
FEATURE [App::DocumentObjectGroupPython] K_element008  label="K_element : 1"  # scripted group (container) (typed FeaturePython)
  n = 1
  ref = K_element
FEATURE [App::DocumentObjectGroupPython] I_element006  label="I_element : 003"  # scripted group (container) (typed FeaturePython)
  n = 1
  ref = I_element
FEATURE [App::DocumentObjectGroupPython] G4_POTASSIUM_IODIDE  # scripted group (container) (typed FeaturePython)
  Dunit = g/cm3
  Dvalue = 3.13
  Group = -> [K_element008,I_element006]
  conduct = 2
  density = 1
  expand = 3
  formula = G4_POTASSIUM_IODIDE
  name = G4_POTASSIUM_IODIDE
  specific = 4
FEATURE [App::DocumentObjectGroupPython] K_element009  label="K_element : 2"  # scripted group (container) (typed FeaturePython)
  n = 2
  ref = K_element
FEATURE [App::DocumentObjectGroupPython] O_element085  label="O_element : 046"  # scripted group (container) (typed FeaturePython)
  n = 1
  ref = O_element
FEATURE [App::DocumentObjectGroupPython] G4_POTASSIUM_OXIDE  # scripted group (container) (typed FeaturePython)
  Dunit = g/cm3
  Dvalue = 2.32
  Group = -> [K_element009,O_element085]
  conduct = 2
  density = 1
  expand = 3
  formula = G4_POTASSIUM_OXIDE
  name = G4_POTASSIUM_OXIDE
  specific = 4
FEATURE [App::DocumentObjectGroupPython] C_element096  label="C_element : 054"  # scripted group (container) (typed FeaturePython)
  n = 3
  ref = C_element
FEATURE [App::DocumentObjectGroupPython] H_element088  label="H_element : 049"  # scripted group (container) (typed FeaturePython)
  n = 8
  ref = H_element
FEATURE [App::DocumentObjectGroupPython] G4_PROPANE  # scripted group (container) (typed FeaturePython)
  Dunit = g/cm3
  Dvalue = 0.00187939
  Group = -> [C_element096,H_element088]
  conduct = 2
  density = 1
  expand = 3
  formula = G4_PROPANE
  name = G4_PROPANE
  specific = 4
FEATURE [App::DocumentObjectGroupPython] C_element097  label="C_element : 055"  # scripted group (container) (typed FeaturePython)
  n = 3
  ref = C_element
FEATURE [App::DocumentObjectGroupPython] H_element089  label="H_element : 050"  # scripted group (container) (typed FeaturePython)
  n = 8
  ref = H_element
FEATURE [App::DocumentObjectGroupPython] G4_lPROPANE  # scripted group (container) (typed FeaturePython)
  Dunit = g/cm3
  Dvalue = 0.43
  Group = -> [C_element097,H_element089]
  conduct = 2
  density = 1
  expand = 3
  formula = G4_lPROPANE
  name = G4_lPROPANE
  specific = 4
FEATURE [App::DocumentObjectGroupPython] C_element098  label="C_element : 056"  # scripted group (container) (typed FeaturePython)
  n = 3
  ref = C_element
FEATURE [App::DocumentObjectGroupPython] H_element090  label="H_element : 051"  # scripted group (container) (typed FeaturePython)
  n = 8
  ref = H_element
FEATURE [App::DocumentObjectGroupPython] O_element086  label="O_element : 047"  # scripted group (container) (typed FeaturePython)
  n = 1
  ref = O_element
FEATURE [App::DocumentObjectGroupPython] G4_N_PROPYL_ALCOHOL  label="G4_N-PROPYL_ALCOHOL"  # scripted group (container) (typed FeaturePython)
  Dunit = g/cm3
  Dvalue = 0.8035
  Group = -> [C_element098,H_element090,O_element086]
  conduct = 2
  density = 1
  expand = 3
  formula = G4_N-PROPYL_ALCOHOL
  name = G4_N-PROPYL_ALCOHOL
  specific = 4
FEATURE [App::DocumentObjectGroupPython] C_element099  label="C_element : 057"  # scripted group (container) (typed FeaturePython)
  n = 5
  ref = C_element
FEATURE [App::DocumentObjectGroupPython] H_element091  label="H_element : 052"  # scripted group (container) (typed FeaturePython)
  n = 5
  ref = H_element
FEATURE [App::DocumentObjectGroupPython] N_element038  label="N_element : 017"  # scripted group (container) (typed FeaturePython)
  n = 1
  ref = N_element
FEATURE [App::DocumentObjectGroupPython] G4_PYRIDINE  # scripted group (container) (typed FeaturePython)
  Dunit = g/cm3
  Dvalue = 0.9819
  Group = -> [C_element099,H_element091,N_element038]
  conduct = 2
  density = 1
  expand = 3
  formula = G4_PYRIDINE
  name = G4_PYRIDINE
  specific = 4
FEATURE [App::DocumentObjectGroupPython] H_element092  label="H_element : 0.144"  # scripted group (container) (typed FeaturePython)
  n = 0.143711
FEATURE [App::DocumentObjectGroupPython] C_element100  label="C_element : 0.856"  # scripted group (container) (typed FeaturePython)
  n = 0.856289
FEATURE [App::DocumentObjectGroupPython] G4_RUBBER_BUTYL  # scripted group (container) (typed FeaturePython)
  Dunit = g/cm3
  Dvalue = 0.92
  Group = -> [H_element092,C_element100]
  conduct = 2
  density = 1
  expand = 3
  formula = G4_RUBBER_BUTYL
  name = G4_RUBBER_BUTYL
  specific = 4
FEATURE [App::DocumentObjectGroupPython] H_element093  label="H_element : 0.118"  # scripted group (container) (typed FeaturePython)
  n = 0.118371
FEATURE [App::DocumentObjectGroupPython] C_element101  label="C_element : 0.882"  # scripted group (container) (typed FeaturePython)
  n = 0.881629
FEATURE [App::DocumentObjectGroupPython] G4_RUBBER_NATURAL  # scripted group (container) (typed FeaturePython)
  Dunit = g/cm3
  Dvalue = 0.92
  Group = -> [H_element093,C_element101]
  conduct = 2
  density = 1
  expand = 3
  formula = G4_RUBBER_NATURAL
  name = G4_RUBBER_NATURAL
  specific = 4
FEATURE [App::DocumentObjectGroupPython] H_element094  label="H_element : 0.145"  # scripted group (container) (typed FeaturePython)
  n = 0.05692
FEATURE [App::DocumentObjectGroupPython] C_element102  label="C_element : 0.543"  # scripted group (container) (typed FeaturePython)
  n = 0.542646
FEATURE [App::DocumentObjectGroupPython] Cl_element021  label="Cl_element : 0.400"  # scripted group (container) (typed FeaturePython)
  n = 0.400434
FEATURE [App::DocumentObjectGroupPython] G4_RUBBER_NEOPRENE  # scripted group (container) (typed FeaturePython)
  Dunit = g/cm3
  Dvalue = 1.23
  Group = -> [H_element094,C_element102,Cl_element021]
  conduct = 2
  density = 1
  expand = 3
  formula = G4_RUBBER_NEOPRENE
  name = G4_RUBBER_NEOPRENE
  specific = 4
FEATURE [App::DocumentObjectGroupPython] Si_element006  label="Si_element : 1"  # scripted group (container) (typed FeaturePython)
  n = 1
  ref = Si_element
FEATURE [App::DocumentObjectGroupPython] O_element087  label="O_element : 048"  # scripted group (container) (typed FeaturePython)
  n = 2
  ref = O_element
FEATURE [App::DocumentObjectGroupPython] G4_SILICON_DIOXIDE  # scripted group (container) (typed FeaturePython)
  Dunit = g/cm3
  Dvalue = 2.32
  Group = -> [Si_element006,O_element087]
  conduct = 2
  density = 1
  expand = 3
  formula = G4_SILICON_DIOXIDE
  name = G4_SILICON_DIOXIDE
  specific = 4
FEATURE [App::DocumentObjectGroupPython] Ag_element002  label="Ag_element : 1"  # scripted group (container) (typed FeaturePython)
  n = 1
  ref = Ag_element
FEATURE [App::DocumentObjectGroupPython] Br_element005  label="Br_element : 003"  # scripted group (container) (typed FeaturePython)
  n = 1
  ref = Br_element
FEATURE [App::DocumentObjectGroupPython] G4_SILVER_BROMIDE  # scripted group (container) (typed FeaturePython)
  Dunit = g/cm3
  Dvalue = 6.473
  Group = -> [Ag_element002,Br_element005]
  conduct = 2
  density = 1
  expand = 3
  formula = G4_SILVER_BROMIDE
  name = G4_SILVER_BROMIDE
  specific = 4
FEATURE [App::DocumentObjectGroupPython] Ag_element003  label="Ag_element : 002"  # scripted group (container) (typed FeaturePython)
  n = 1
  ref = Ag_element
FEATURE [App::DocumentObjectGroupPython] Cl_element022  label="Cl_element : 011"  # scripted group (container) (typed FeaturePython)
  n = 1
  ref = Cl_element
FEATURE [App::DocumentObjectGroupPython] G4_SILVER_CHLORIDE  # scripted group (container) (typed FeaturePython)
  Dunit = g/cm3
  Dvalue = 5.56
  Group = -> [Ag_element003,Cl_element022]
  conduct = 2
  density = 1
  expand = 3
  formula = G4_SILVER_CHLORIDE
  name = G4_SILVER_CHLORIDE
  specific = 4
FEATURE [App::DocumentObjectGroupPython] Br_element006  label="Br_element : 0.423"  # scripted group (container) (typed FeaturePython)
  n = 0.422895
FEATURE [App::DocumentObjectGroupPython] Ag_element004  label="Ag_element : 0.574"  # scripted group (container) (typed FeaturePython)
  n = 0.573748
FEATURE [App::DocumentObjectGroupPython] I_element007  label="I_element : 0.649"  # scripted group (container) (typed FeaturePython)
  n = 0.003357
FEATURE [App::DocumentObjectGroupPython] G4_SILVER_HALIDES  # scripted group (container) (typed FeaturePython)
  Dunit = g/cm3
  Dvalue = 6.47
  Group = -> [Br_element006,Ag_element004,I_element007]
  conduct = 2
  density = 1
  expand = 3
  formula = G4_SILVER_HALIDES
  name = G4_SILVER_HALIDES
  specific = 4
FEATURE [App::DocumentObjectGroupPython] Ag_element005  label="Ag_element : 003"  # scripted group (container) (typed FeaturePython)
  n = 1
  ref = Ag_element
FEATURE [App::DocumentObjectGroupPython] I_element008  label="I_element : 004"  # scripted group (container) (typed FeaturePython)
  n = 1
  ref = I_element
FEATURE [App::DocumentObjectGroupPython] G4_SILVER_IODIDE  # scripted group (container) (typed FeaturePython)
  Dunit = g/cm3
  Dvalue = 6.01
  Group = -> [Ag_element005,I_element008]
  conduct = 2
  density = 1
  expand = 3
  formula = G4_SILVER_IODIDE
  name = G4_SILVER_IODIDE
  specific = 4
FEATURE [App::DocumentObjectGroupPython] H_element095  label="H_element : 0.100"  # scripted group (container) (typed FeaturePython)
  n = 0.1
FEATURE [App::DocumentObjectGroupPython] C_element103  label="C_element : 0.204"  # scripted group (container) (typed FeaturePython)
  n = 0.204
FEATURE [App::DocumentObjectGroupPython] N_element039  label="N_element : 0.759"  # scripted group (container) (typed FeaturePython)
  n = 0.042
FEATURE [App::DocumentObjectGroupPython] O_element088  label="O_element : 0.645"  # scripted group (container) (typed FeaturePython)
  n = 0.645
FEATURE [App::DocumentObjectGroupPython] Na_element013  label="Na_element : 0.100"  # scripted group (container) (typed FeaturePython)
  n = 0.002
FEATURE [App::DocumentObjectGroupPython] P_element009  label="P_element : 0.107"  # scripted group (container) (typed FeaturePython)
  n = 0.001
FEATURE [App::DocumentObjectGroupPython] S_element020  label="S_element : 0.021"  # scripted group (container) (typed FeaturePython)
  n = 0.002
FEATURE [App::DocumentObjectGroupPython] Cl_element023  label="Cl_element : 0.590"  # scripted group (container) (typed FeaturePython)
  n = 0.003
FEATURE [App::DocumentObjectGroupPython] K_element010  label="K_element : 0.001"  # scripted group (container) (typed FeaturePython)
  n = 0.001
FEATURE [App::DocumentObjectGroupPython] G4_SKIN_ICRP  # scripted group (container) (typed FeaturePython)
  Dunit = g/cm3
  Dvalue = 1.09
  Group = -> [H_element095,C_element103,N_element039,O_element088,Na_element013,P_element009,S_element020,Cl_element023,K_element010]
  conduct = 2
  density = 1
  expand = 3
  formula = G4_SKIN_ICRP
  name = G4_SKIN_ICRP
  specific = 4
FEATURE [App::DocumentObjectGroupPython] Na_element014  label="Na_element : 2"  # scripted group (container) (typed FeaturePython)
  n = 2
  ref = Na_element
FEATURE [App::DocumentObjectGroupPython] C_element104  label="C_element : 058"  # scripted group (container) (typed FeaturePython)
  n = 1
  ref = C_element
FEATURE [App::DocumentObjectGroupPython] O_element089  label="O_element : 049"  # scripted group (container) (typed FeaturePython)
  n = 3
  ref = O_element
FEATURE [App::DocumentObjectGroupPython] G4_SODIUM_CARBONATE  # scripted group (container) (typed FeaturePython)
  Dunit = g/cm3
  Dvalue = 2.532
  Group = -> [Na_element014,C_element104,O_element089]
  conduct = 2
  density = 1
  expand = 3
  formula = G4_SODIUM_CARBONATE
  name = G4_SODIUM_CARBONATE
  specific = 4
FEATURE [App::DocumentObjectGroupPython] Na_element015  label="Na_element : 1"  # scripted group (container) (typed FeaturePython)
  n = 1
  ref = Na_element
FEATURE [App::DocumentObjectGroupPython] I_element009  label="I_element : 005"  # scripted group (container) (typed FeaturePython)
  n = 1
  ref = I_element
FEATURE [App::DocumentObjectGroupPython] G4_SODIUM_IODIDE  # scripted group (container) (typed FeaturePython)
  Dunit = g/cm3
  Dvalue = 3.667
  Group = -> [Na_element015,I_element009]
  conduct = 2
  density = 1
  expand = 3
  formula = G4_SODIUM_IODIDE
  name = G4_SODIUM_IODIDE
  specific = 4
FEATURE [App::DocumentObjectGroupPython] Na_element016  label="Na_element : 003"  # scripted group (container) (typed FeaturePython)
  n = 2
  ref = Na_element
FEATURE [App::DocumentObjectGroupPython] O_element090  label="O_element : 050"  # scripted group (container) (typed FeaturePython)
  n = 1
  ref = O_element
FEATURE [App::DocumentObjectGroupPython] G4_SODIUM_MONOXIDE  # scripted group (container) (typed FeaturePython)
  Dunit = g/cm3
  Dvalue = 2.27
  Group = -> [Na_element016,O_element090]
  conduct = 2
  density = 1
  expand = 3
  formula = G4_SODIUM_MONOXIDE
  name = G4_SODIUM_MONOXIDE
  specific = 4
FEATURE [App::DocumentObjectGroupPython] Na_element017  label="Na_element : 004"  # scripted group (container) (typed FeaturePython)
  n = 1
  ref = Na_element
FEATURE [App::DocumentObjectGroupPython] N_element040  label="N_element : 018"  # scripted group (container) (typed FeaturePython)
  n = 1
  ref = N_element
FEATURE [App::DocumentObjectGroupPython] O_element091  label="O_element : 051"  # scripted group (container) (typed FeaturePython)
  n = 3
  ref = O_element
FEATURE [App::DocumentObjectGroupPython] G4_SODIUM_NITRATE  # scripted group (container) (typed FeaturePython)
  Dunit = g/cm3
  Dvalue = 2.261
  Group = -> [Na_element017,N_element040,O_element091]
  conduct = 2
  density = 1
  expand = 3
  formula = G4_SODIUM_NITRATE
  name = G4_SODIUM_NITRATE
  specific = 4
FEATURE [App::DocumentObjectGroupPython] C_element105  label="C_element : 059"  # scripted group (container) (typed FeaturePython)
  n = 14
  ref = C_element
FEATURE [App::DocumentObjectGroupPython] H_element096  label="H_element : 053"  # scripted group (container) (typed FeaturePython)
  n = 12
  ref = H_element
FEATURE [App::DocumentObjectGroupPython] G4_STILBENE  # scripted group (container) (typed FeaturePython)
  Dunit = g/cm3
  Dvalue = 0.9707
  Group = -> [C_element105,H_element096]
  conduct = 2
  density = 1
  expand = 3
  formula = G4_STILBENE
  name = G4_STILBENE
  specific = 4
FEATURE [App::DocumentObjectGroupPython] C_element106  label="C_element : 12"  # scripted group (container) (typed FeaturePython)
  n = 12
  ref = C_element
FEATURE [App::DocumentObjectGroupPython] H_element097  label="H_element : 22"  # scripted group (container) (typed FeaturePython)
  n = 22
  ref = H_element
FEATURE [App::DocumentObjectGroupPython] O_element092  label="O_element : 11"  # scripted group (container) (typed FeaturePython)
  n = 11
  ref = O_element
FEATURE [App::DocumentObjectGroupPython] G4_SUCROSE  # scripted group (container) (typed FeaturePython)
  Dunit = g/cm3
  Dvalue = 1.5805
  Group = -> [C_element106,H_element097,O_element092]
  conduct = 2
  density = 1
  expand = 3
  formula = G4_SUCROSE
  name = G4_SUCROSE
  specific = 4
FEATURE [App::DocumentObjectGroupPython] C_element107  label="C_element : 18"  # scripted group (container) (typed FeaturePython)
  n = 18
  ref = C_element
FEATURE [App::DocumentObjectGroupPython] H_element098  label="H_element : 054"  # scripted group (container) (typed FeaturePython)
  n = 14
  ref = H_element
FEATURE [App::DocumentObjectGroupPython] G4_TERPHENYL  # scripted group (container) (typed FeaturePython)
  Dunit = g/cm3
  Dvalue = 1.24
  Group = -> [C_element107,H_element098]
  conduct = 2
  density = 1
  expand = 3
  formula = G4_TERPHENYL
  name = G4_TERPHENYL
  specific = 4
FEATURE [App::DocumentObjectGroupPython] H_element099  label="H_element : 0.146"  # scripted group (container) (typed FeaturePython)
  n = 0.106
FEATURE [App::DocumentObjectGroupPython] C_element108  label="C_element : 0.883"  # scripted group (container) (typed FeaturePython)
  n = 0.099
FEATURE [App::DocumentObjectGroupPython] N_element041  label="N_element : 0.020"  # scripted group (container) (typed FeaturePython)
  n = 0.02
FEATURE [App::DocumentObjectGroupPython] O_element093  label="O_element : 0.766"  # scripted group (container) (typed FeaturePython)
  n = 0.766
FEATURE [App::DocumentObjectGroupPython] Na_element018  label="Na_element : 0.101"  # scripted group (container) (typed FeaturePython)
  n = 0.002
FEATURE [App::DocumentObjectGroupPython] P_element010  label="P_element : 0.108"  # scripted group (container) (typed FeaturePython)
  n = 0.001
FEATURE [App::DocumentObjectGroupPython] S_element021  label="S_element : 0.022"  # scripted group (container) (typed FeaturePython)
  n = 0.002
FEATURE [App::DocumentObjectGroupPython] Cl_element024  label="Cl_element : 0.002"  # scripted group (container) (typed FeaturePython)
  n = 0.002
FEATURE [App::DocumentObjectGroupPython] K_element011  label="K_element : 0.017"  # scripted group (container) (typed FeaturePython)
  n = 0.002
FEATURE [App::DocumentObjectGroupPython] G4_TESTIS_ICRP  # scripted group (container) (typed FeaturePython)
  Dunit = g/cm3
  Dvalue = 1.04
  Group = -> [H_element099,C_element108,N_element041,O_element093,Na_element018,P_element010,S_element021,Cl_element024,K_element011]
  conduct = 2
  density = 1
  expand = 3
  formula = G4_TESTIS_ICRP
  name = G4_TESTIS_ICRP
  specific = 4
FEATURE [App::DocumentObjectGroupPython] C_element109  label="C_element : 060"  # scripted group (container) (typed FeaturePython)
  n = 2
  ref = C_element
FEATURE [App::DocumentObjectGroupPython] Cl_element025  label="Cl_element : 012"  # scripted group (container) (typed FeaturePython)
  n = 4
  ref = Cl_element
FEATURE [App::DocumentObjectGroupPython] G4_TETRACHLOROETHYLENE  # scripted group (container) (typed FeaturePython)
  Dunit = g/cm3
  Dvalue = 1.625
  Group = -> [C_element109,Cl_element025]
  conduct = 2
  density = 1
  expand = 3
  formula = G4_TETRACHLOROETHYLENE
  name = G4_TETRACHLOROETHYLENE
  specific = 4
FEATURE [App::DocumentObjectGroupPython] Tl_element001  label="Tl_element : 1"  # scripted group (container) (typed FeaturePython)
  n = 1
  ref = Tl_element
FEATURE [App::DocumentObjectGroupPython] Cl_element026  label="Cl_element : 013"  # scripted group (container) (typed FeaturePython)
  n = 1
  ref = Cl_element
FEATURE [App::DocumentObjectGroupPython] G4_THALLIUM_CHLORIDE  # scripted group (container) (typed FeaturePython)
  Dunit = g/cm3
  Dvalue = 7.004
  Group = -> [Tl_element001,Cl_element026]
  conduct = 2
  density = 1
  expand = 3
  formula = G4_THALLIUM_CHLORIDE
  name = G4_THALLIUM_CHLORIDE
  specific = 4
FEATURE [App::DocumentObjectGroupPython] H_element100  label="H_element : 0.147"  # scripted group (container) (typed FeaturePython)
  n = 0.105
FEATURE [App::DocumentObjectGroupPython] C_element110  label="C_element : 0.256"  # scripted group (container) (typed FeaturePython)
  n = 0.256
FEATURE [App::DocumentObjectGroupPython] N_element042  label="N_element : 0.760"  # scripted group (container) (typed FeaturePython)
  n = 0.027
FEATURE [App::DocumentObjectGroupPython] O_element094  label="O_element : 0.602"  # scripted group (container) (typed FeaturePython)
  n = 0.602
FEATURE [App::DocumentObjectGroupPython] Na_element019  label="Na_element : 0.102"  # scripted group (container) (typed FeaturePython)
  n = 0.001
FEATURE [App::DocumentObjectGroupPython] P_element011  label="P_element : 0.109"  # scripted group (container) (typed FeaturePython)
  n = 0.002
FEATURE [App::DocumentObjectGroupPython] S_element022  label="S_element : 0.023"  # scripted group (container) (typed FeaturePython)
  n = 0.003
FEATURE [App::DocumentObjectGroupPython] Cl_element027  label="Cl_element : 0.591"  # scripted group (container) (typed FeaturePython)
  n = 0.002
FEATURE [App::DocumentObjectGroupPython] K_element012  label="K_element : 0.018"  # scripted group (container) (typed FeaturePython)
  n = 0.002
FEATURE [App::DocumentObjectGroupPython] G4_TISSUE_SOFT_ICRP  # scripted group (container) (typed FeaturePython)
  Dunit = g/cm3
  Dvalue = 1.03
  Group = -> [H_element100,C_element110,N_element042,O_element094,Na_element019,P_element011,S_element022,Cl_element027,K_element012]
  conduct = 2
  density = 1
  expand = 3
  formula = G4_TISSUE_SOFT_ICRP
  name = G4_TISSUE_SOFT_ICRP
  specific = 4
FEATURE [App::DocumentObjectGroupPython] H_element101  label="H_element : 0.148"  # scripted group (container) (typed FeaturePython)
  n = 0.101
FEATURE [App::DocumentObjectGroupPython] C_element111  label="C_element : 0.111"  # scripted group (container) (typed FeaturePython)
  n = 0.111
FEATURE [App::DocumentObjectGroupPython] N_element043  label="N_element : 0.026"  # scripted group (container) (typed FeaturePython)
  n = 0.026
FEATURE [App::DocumentObjectGroupPython] O_element095  label="O_element : 0.762"  # scripted group (container) (typed FeaturePython)
  n = 0.762
FEATURE [App::DocumentObjectGroupPython] G4_TISSUE_SOFT_ICRU_4  label="G4_TISSUE_SOFT_ICRU-4"  # scripted group (container) (typed FeaturePython)
  Dunit = g/cm3
  Dvalue = 1
  Group = -> [H_element101,C_element111,N_element043,O_element095]
  conduct = 2
  density = 1
  expand = 3
  formula = G4_TISSUE_SOFT_ICRU-4
  name = G4_TISSUE_SOFT_ICRU-4
  specific = 4
FEATURE [App::DocumentObjectGroupPython] H_element102  label="H_element : 0.149"  # scripted group (container) (typed FeaturePython)
  n = 0.101869
FEATURE [App::DocumentObjectGroupPython] C_element112  label="C_element : 0.456"  # scripted group (container) (typed FeaturePython)
  n = 0.456179
FEATURE [App::DocumentObjectGroupPython] N_element044  label="N_element : 0.761"  # scripted group (container) (typed FeaturePython)
  n = 0.035172
FEATURE [App::DocumentObjectGroupPython] O_element096  label="O_element : 0.407"  # scripted group (container) (typed FeaturePython)
  n = 0.40678
FEATURE [App::DocumentObjectGroupPython] G4_TISSUE_METHANE  label="G4_TISSUE-METHANE"  # scripted group (container) (typed FeaturePython)
  Dunit = g/cm3
  Dvalue = 0.00106409
  Group = -> [H_element102,C_element112,N_element044,O_element096]
  conduct = 2
  density = 1
  expand = 3
  formula = G4_TISSUE-METHANE
  name = G4_TISSUE-METHANE
  specific = 4
FEATURE [App::DocumentObjectGroupPython] H_element103  label="H_element : 0.103"  # scripted group (container) (typed FeaturePython)
  n = 0.102672
FEATURE [App::DocumentObjectGroupPython] C_element113  label="C_element : 0.569"  # scripted group (container) (typed FeaturePython)
  n = 0.56894
FEATURE [App::DocumentObjectGroupPython] N_element045  label="N_element : 0.762"  # scripted group (container) (typed FeaturePython)
  n = 0.035022
FEATURE [App::DocumentObjectGroupPython] O_element097  label="O_element : 0.293"  # scripted group (container) (typed FeaturePython)
  n = 0.293366
FEATURE [App::DocumentObjectGroupPython] G4_TISSUE_PROPANE  label="G4_TISSUE-PROPANE"  # scripted group (container) (typed FeaturePython)
  Dunit = g/cm3
  Dvalue = 0.00182628
  Group = -> [H_element103,C_element113,N_element045,O_element097]
  conduct = 2
  density = 1
  expand = 3
  formula = G4_TISSUE-PROPANE
  name = G4_TISSUE-PROPANE
  specific = 4
FEATURE [App::DocumentObjectGroupPython] Ti_element003  label="Ti_element : 1"  # scripted group (container) (typed FeaturePython)
  n = 1
  ref = Ti_element
FEATURE [App::DocumentObjectGroupPython] O_element098  label="O_element : 052"  # scripted group (container) (typed FeaturePython)
  n = 2
  ref = O_element
FEATURE [App::DocumentObjectGroupPython] G4_TITANIUM_DIOXIDE  # scripted group (container) (typed FeaturePython)
  Dunit = g/cm3
  Dvalue = 4.26
  Group = -> [Ti_element003,O_element098]
  conduct = 2
  density = 1
  expand = 3
  formula = G4_TITANIUM_DIOXIDE
  name = G4_TITANIUM_DIOXIDE
  specific = 4
FEATURE [App::DocumentObjectGroupPython] C_element114  label="C_element : 061"  # scripted group (container) (typed FeaturePython)
  n = 7
  ref = C_element
FEATURE [App::DocumentObjectGroupPython] H_element104  label="H_element : 055"  # scripted group (container) (typed FeaturePython)
  n = 8
  ref = H_element
FEATURE [App::DocumentObjectGroupPython] G4_TOLUENE  # scripted group (container) (typed FeaturePython)
  Dunit = g/cm3
  Dvalue = 0.8669
  Group = -> [C_element114,H_element104]
  conduct = 2
  density = 1
  expand = 3
  formula = G4_TOLUENE
  name = G4_TOLUENE
  specific = 4
FEATURE [App::DocumentObjectGroupPython] C_element115  label="C_element : 062"  # scripted group (container) (typed FeaturePython)
  n = 2
  ref = C_element
FEATURE [App::DocumentObjectGroupPython] H_element105  label="H_element : 056"  # scripted group (container) (typed FeaturePython)
  n = 1
  ref = H_element
FEATURE [App::DocumentObjectGroupPython] Cl_element028  label="Cl_element : 014"  # scripted group (container) (typed FeaturePython)
  n = 3
  ref = Cl_element
FEATURE [App::DocumentObjectGroupPython] G4_TRICHLOROETHYLENE  # scripted group (container) (typed FeaturePython)
  Dunit = g/cm3
  Dvalue = 1.46
  Group = -> [C_element115,H_element105,Cl_element028]
  conduct = 2
  density = 1
  expand = 3
  formula = G4_TRICHLOROETHYLENE
  name = G4_TRICHLOROETHYLENE
  specific = 4
FEATURE [App::DocumentObjectGroupPython] C_element116  label="C_element : 063"  # scripted group (container) (typed FeaturePython)
  n = 6
  ref = C_element
FEATURE [App::DocumentObjectGroupPython] H_element106  label="H_element : 15"  # scripted group (container) (typed FeaturePython)
  n = 15
  ref = H_element
FEATURE [App::DocumentObjectGroupPython] O_element099  label="O_element : 053"  # scripted group (container) (typed FeaturePython)
  n = 4
  ref = O_element
FEATURE [App::DocumentObjectGroupPython] P_element012  label="P_element : 1"  # scripted group (container) (typed FeaturePython)
  n = 1
  ref = P_element
FEATURE [App::DocumentObjectGroupPython] G4_TRIETHYL_PHOSPHATE  # scripted group (container) (typed FeaturePython)
  Dunit = g/cm3
  Dvalue = 1.07
  Group = -> [C_element116,H_element106,O_element099,P_element012]
  conduct = 2
  density = 1
  expand = 3
  formula = G4_TRIETHYL_PHOSPHATE
  name = G4_TRIETHYL_PHOSPHATE
  specific = 4
FEATURE [App::DocumentObjectGroupPython] W_element003  label="W_element : 003"  # scripted group (container) (typed FeaturePython)
  n = 1
  ref = W_element
FEATURE [App::DocumentObjectGroupPython] F_element017  label="F_element : 6"  # scripted group (container) (typed FeaturePython)
  n = 6
  ref = F_element
FEATURE [App::DocumentObjectGroupPython] G4_TUNGSTEN_HEXAFLUORIDE  # scripted group (container) (typed FeaturePython)
  Dunit = g/cm3
  Dvalue = 2.4
  Group = -> [W_element003,F_element017]
  conduct = 2
  density = 1
  expand = 3
  formula = G4_TUNGSTEN_HEXAFLUORIDE
  name = G4_TUNGSTEN_HEXAFLUORIDE
  specific = 4
FEATURE [App::DocumentObjectGroupPython] U_element001  label="U_element : 1"  # scripted group (container) (typed FeaturePython)
  n = 1
  ref = U_element
FEATURE [App::DocumentObjectGroupPython] C_element117  label="C_element : 064"  # scripted group (container) (typed FeaturePython)
  n = 2
  ref = C_element
FEATURE [App::DocumentObjectGroupPython] G4_URANIUM_DICARBIDE  # scripted group (container) (typed FeaturePython)
  Dunit = g/cm3
  Dvalue = 11.28
  Group = -> [U_element001,C_element117]
  conduct = 2
  density = 1
  expand = 3
  formula = G4_URANIUM_DICARBIDE
  name = G4_URANIUM_DICARBIDE
  specific = 4
FEATURE [App::DocumentObjectGroupPython] U_element002  label="U_element : 002"  # scripted group (container) (typed FeaturePython)
  n = 1
  ref = U_element
FEATURE [App::DocumentObjectGroupPython] C_element118  label="C_element : 065"  # scripted group (container) (typed FeaturePython)
  n = 1
  ref = C_element
FEATURE [App::DocumentObjectGroupPython] G4_URANIUM_MONOCARBIDE  # scripted group (container) (typed FeaturePython)
  Dunit = g/cm3
  Dvalue = 13.63
  Group = -> [U_element002,C_element118]
  conduct = 2
  density = 1
  expand = 3
  formula = G4_URANIUM_MONOCARBIDE
  name = G4_URANIUM_MONOCARBIDE
  specific = 4
FEATURE [App::DocumentObjectGroupPython] U_element003  label="U_element : 003"  # scripted group (container) (typed FeaturePython)
  n = 1
  ref = U_element
FEATURE [App::DocumentObjectGroupPython] O_element100  label="O_element : 054"  # scripted group (container) (typed FeaturePython)
  n = 2
  ref = O_element
FEATURE [App::DocumentObjectGroupPython] G4_URANIUM_OXIDE  # scripted group (container) (typed FeaturePython)
  Dunit = g/cm3
  Dvalue = 10.96
  Group = -> [U_element003,O_element100]
  conduct = 2
  density = 1
  expand = 3
  formula = G4_URANIUM_OXIDE
  name = G4_URANIUM_OXIDE
  specific = 4
FEATURE [App::DocumentObjectGroupPython] C_element119  label="C_element : 066"  # scripted group (container) (typed FeaturePython)
  n = 1
  ref = C_element
FEATURE [App::DocumentObjectGroupPython] H_element107  label="H_element : 057"  # scripted group (container) (typed FeaturePython)
  n = 4
  ref = H_element
FEATURE [App::DocumentObjectGroupPython] N_element046  label="N_element : 019"  # scripted group (container) (typed FeaturePython)
  n = 2
  ref = N_element
FEATURE [App::DocumentObjectGroupPython] O_element101  label="O_element : 055"  # scripted group (container) (typed FeaturePython)
  n = 1
  ref = O_element
FEATURE [App::DocumentObjectGroupPython] G4_UREA  # scripted group (container) (typed FeaturePython)
  Dunit = g/cm3
  Dvalue = 1.323
  Group = -> [C_element119,H_element107,N_element046,O_element101]
  conduct = 2
  density = 1
  expand = 3
  formula = G4_UREA
  name = G4_UREA
  specific = 4
FEATURE [App::DocumentObjectGroupPython] C_element120  label="C_element : 067"  # scripted group (container) (typed FeaturePython)
  n = 5
  ref = C_element
FEATURE [App::DocumentObjectGroupPython] H_element108  label="H_element : 058"  # scripted group (container) (typed FeaturePython)
  n = 11
  ref = H_element
FEATURE [App::DocumentObjectGroupPython] N_element047  label="N_element : 020"  # scripted group (container) (typed FeaturePython)
  n = 1
  ref = N_element
FEATURE [App::DocumentObjectGroupPython] O_element102  label="O_element : 056"  # scripted group (container) (typed FeaturePython)
  n = 2
  ref = O_element
FEATURE [App::DocumentObjectGroupPython] G4_VALINE  # scripted group (container) (typed FeaturePython)
  Dunit = g/cm3
  Dvalue = 1.23
  Group = -> [C_element120,H_element108,N_element047,O_element102]
  conduct = 2
  density = 1
  expand = 3
  formula = G4_VALINE
  name = G4_VALINE
  specific = 4
FEATURE [App::DocumentObjectGroupPython] H_element109  label="H_element : 0.009"  # scripted group (container) (typed FeaturePython)
  n = 0.009417
FEATURE [App::DocumentObjectGroupPython] C_element121  label="C_element : 0.281"  # scripted group (container) (typed FeaturePython)
  n = 0.280555
FEATURE [App::DocumentObjectGroupPython] F_element018  label="F_element : 0.710"  # scripted group (container) (typed FeaturePython)
  n = 0.710028
FEATURE [App::DocumentObjectGroupPython] G4_VITON  # scripted group (container) (typed FeaturePython)
  Dunit = g/cm3
  Dvalue = 1.8
  Group = -> [H_element109,C_element121,F_element018]
  conduct = 2
  density = 1
  expand = 3
  formula = G4_VITON
  name = G4_VITON
  specific = 4
FEATURE [App::DocumentObjectGroupPython] H_element110  label="H_element : 059"  # scripted group (container) (typed FeaturePython)
  n = 2
  ref = H_element
FEATURE [App::DocumentObjectGroupPython] O_element103  label="O_element : 057"  # scripted group (container) (typed FeaturePython)
  n = 1
  ref = O_element
FEATURE [App::DocumentObjectGroupPython] G4_WATER  # scripted group (container) (typed FeaturePython)
  Dunit = g/cm3
  Dvalue = 1
  Group = -> [H_element110,O_element103]
  conduct = 2
  density = 1
  expand = 3
  formula = G4_WATER
  name = G4_WATER
  specific = 4
FEATURE [App::DocumentObjectGroupPython] H_element111  label="H_element : 060"  # scripted group (container) (typed FeaturePython)
  n = 2
  ref = H_element
FEATURE [App::DocumentObjectGroupPython] O_element104  label="O_element : 058"  # scripted group (container) (typed FeaturePython)
  n = 1
  ref = O_element
FEATURE [App::DocumentObjectGroupPython] G4_WATER_VAPOR  # scripted group (container) (typed FeaturePython)
  Dunit = g/cm3
  Dvalue = 0.000756182
  Group = -> [H_element111,O_element104]
  conduct = 2
  density = 1
  expand = 3
  formula = G4_WATER_VAPOR
  name = G4_WATER_VAPOR
  specific = 4
FEATURE [App::DocumentObjectGroupPython] C_element122  label="C_element : 068"  # scripted group (container) (typed FeaturePython)
  n = 8
  ref = C_element
FEATURE [App::DocumentObjectGroupPython] H_element112  label="H_element : 061"  # scripted group (container) (typed FeaturePython)
  n = 10
  ref = H_element
FEATURE [App::DocumentObjectGroupPython] G4_XYLENE  # scripted group (container) (typed FeaturePython)
  Dunit = g/cm3
  Dvalue = 0.87
  Group = -> [C_element122,H_element112]
  conduct = 2
  density = 1
  expand = 3
  formula = G4_XYLENE
  name = G4_XYLENE
  specific = 4
FEATURE [App::DocumentObjectGroupPython] C_element123  label="C_element : 069"  # scripted group (container) (typed FeaturePython)
  n = 1
  ref = C_element
FEATURE [App::DocumentObjectGroupPython] G4_GRAPHITE  # scripted group (container) (typed FeaturePython)
  Dunit = g/cm3
  Dvalue = 2.21
  Group = -> [C_element123]
  conduct = 2
  density = 1
  expand = 3
  formula = G4_GRAPHITE
  name = G4_GRAPHITE
  specific = 4
FEATURE [App::DocumentObjectGroupPython] NIST  # scripted group (container) (typed FeaturePython)
  Group = -> [G4_A_150_TISSUE,G4_ACETONE,G4_ACETYLENE,G4_ADENINE,G4_ADIPOSE_TISSUE_ICRP,G4_AIR,G4_ALANINE,G4_ALUMINUM_OXIDE,G4_AMBER,G4_AMMONIA,G4_ANILINE,G4_ANTHRACENE,G4_B_100_BONE,G4_BAKELITE,G4_BARIUM_FLUORIDE,G4_BARIUM_SULFATE,G4_BENZENE,G4_BERYLLIUM_OXIDE,G4_BGO,G4_BLOOD_ICRP,G4_BONE_COMPACT_ICRU,G4_BONE_CORTICAL_ICRP,G4_BORON_CARBIDE,G4_BORON_OXIDE,G4_BRAIN_ICRP,G4_BUTANE,G4_N_BUTYL_ALCOHOL,G4_C_552,+152 more]
FEATURE [App::DocumentObjectGroupPython] H_element113  label="H_element : 062"  # scripted group (container) (typed FeaturePython)
  n = 1
  ref = H_element
FEATURE [App::DocumentObjectGroupPython] G4_H  # scripted group (container) (typed FeaturePython)
  Dunit = g/cm3
  Dvalue = 8.3748e-05
  Group = -> [H_element113]
  conduct = 2
  density = 1
  expand = 3
  formula = H
  name = G4_H
  specific = 4
FEATURE [App::DocumentObjectGroupPython] He_element001  label="He_element : 1"  # scripted group (container) (typed FeaturePython)
  n = 1
  ref = He_element
FEATURE [App::DocumentObjectGroupPython] G4_He  # scripted group (container) (typed FeaturePython)
  Dunit = g/cm3
  Dvalue = 0.000166322
  Group = -> [He_element001]
  conduct = 2
  density = 1
  expand = 3
  formula = He
  name = G4_He
  specific = 4
FEATURE [App::DocumentObjectGroupPython] Li_element008  label="Li_element : 008"  # scripted group (container) (typed FeaturePython)
  n = 1
  ref = Li_element
FEATURE [App::DocumentObjectGroupPython] G4_Li  # scripted group (container) (typed FeaturePython)
  Dunit = g/cm3
  Dvalue = 0.534
  Group = -> [Li_element008]
  conduct = 2
  density = 1
  expand = 3
  formula = Li
  name = G4_Li
  specific = 4
FEATURE [App::DocumentObjectGroupPython] Be_element002  label="Be_element : 002"  # scripted group (container) (typed FeaturePython)
  n = 1
  ref = Be_element
FEATURE [App::DocumentObjectGroupPython] G4_Be  # scripted group (container) (typed FeaturePython)
  Dunit = g/cm3
  Dvalue = 1.848
  Group = -> [Be_element002]
  conduct = 2
  density = 1
  expand = 3
  formula = Be
  name = G4_Be
  specific = 4
FEATURE [App::DocumentObjectGroupPython] B_element007  label="B_element : 007"  # scripted group (container) (typed FeaturePython)
  n = 1
  ref = B_element
FEATURE [App::DocumentObjectGroupPython] G4_B  # scripted group (container) (typed FeaturePython)
  Dunit = g/cm3
  Dvalue = 2.37
  Group = -> [B_element007]
  conduct = 2
  density = 1
  expand = 3
  formula = B
  name = G4_B
  specific = 4
FEATURE [App::DocumentObjectGroupPython] C_element124  label="C_element : 070"  # scripted group (container) (typed FeaturePython)
  n = 1
  ref = C_element
FEATURE [App::DocumentObjectGroupPython] G4_C  # scripted group (container) (typed FeaturePython)
  Dunit = g/cm3
  Dvalue = 2
  Group = -> [C_element124]
  conduct = 2
  density = 1
  expand = 3
  formula = C
  name = G4_C
  specific = 4
FEATURE [App::DocumentObjectGroupPython] N_element048  label="N_element : 021"  # scripted group (container) (typed FeaturePython)
  n = 1
  ref = N_element
FEATURE [App::DocumentObjectGroupPython] G4_N  # scripted group (container) (typed FeaturePython)
  Dunit = g/cm3
  Dvalue = 0.0011652
  Group = -> [N_element048]
  conduct = 2
  density = 1
  expand = 3
  formula = N
  name = G4_N
  specific = 4
FEATURE [App::DocumentObjectGroupPython] O_element105  label="O_element : 059"  # scripted group (container) (typed FeaturePython)
  n = 1
  ref = O_element
FEATURE [App::DocumentObjectGroupPython] G4_O  # scripted group (container) (typed FeaturePython)
  Dunit = g/cm3
  Dvalue = 0.00133151
  Group = -> [O_element105]
  conduct = 2
  density = 1
  expand = 3
  formula = O
  name = G4_O
  specific = 4
FEATURE [App::DocumentObjectGroupPython] F_element019  label="F_element : 008"  # scripted group (container) (typed FeaturePython)
  n = 1
  ref = F_element
FEATURE [App::DocumentObjectGroupPython] G4_F  # scripted group (container) (typed FeaturePython)
  Dunit = g/cm3
  Dvalue = 0.00158029
  Group = -> [F_element019]
  conduct = 2
  density = 1
  expand = 3
  formula = F
  name = G4_F
  specific = 4
FEATURE [App::DocumentObjectGroupPython] Ne_element001  label="Ne_element : 1"  # scripted group (container) (typed FeaturePython)
  n = 1
  ref = Ne_element
FEATURE [App::DocumentObjectGroupPython] G4_Ne  # scripted group (container) (typed FeaturePython)
  Dunit = g/cm3
  Dvalue = 0.000838505
  Group = -> [Ne_element001]
  conduct = 2
  density = 1
  expand = 3
  formula = Ne
  name = G4_Ne
  specific = 4
FEATURE [App::DocumentObjectGroupPython] Na_element020  label="Na_element : 005"  # scripted group (container) (typed FeaturePython)
  n = 1
  ref = Na_element
FEATURE [App::DocumentObjectGroupPython] G4_Na  # scripted group (container) (typed FeaturePython)
  Dunit = g/cm3
  Dvalue = 0.971
  Group = -> [Na_element020]
  conduct = 2
  density = 1
  expand = 3
  formula = Na
  name = G4_Na
  specific = 4
FEATURE [App::DocumentObjectGroupPython] Mg_element011  label="Mg_element : 005"  # scripted group (container) (typed FeaturePython)
  n = 1
  ref = Mg_element
FEATURE [App::DocumentObjectGroupPython] G4_Mg  # scripted group (container) (typed FeaturePython)
  Dunit = g/cm3
  Dvalue = 1.74
  Group = -> [Mg_element011]
  conduct = 2
  density = 1
  expand = 3
  formula = Mg
  name = G4_Mg
  specific = 4
FEATURE [App::DocumentObjectGroupPython] Al_element004  label="Al_element : 1"  # scripted group (container) (typed FeaturePython)
  n = 1
  ref = Al_element
FEATURE [App::DocumentObjectGroupPython] G4_Al  # scripted group (container) (typed FeaturePython)
  Dunit = g/cm3
  Dvalue = 2.699
  Group = -> [Al_element004]
  conduct = 2
  density = 1
  expand = 3
  formula = Al
  name = G4_Al
  specific = 4
FEATURE [App::DocumentObjectGroupPython] Si_element007  label="Si_element : 002"  # scripted group (container) (typed FeaturePython)
  n = 1
  ref = Si_element
FEATURE [App::DocumentObjectGroupPython] G4_Si  # scripted group (container) (typed FeaturePython)
  Dunit = g/cm3
  Dvalue = 2.33
  Group = -> [Si_element007]
  conduct = 2
  density = 1
  expand = 3
  formula = Si
  name = G4_Si
  specific = 4
FEATURE [App::DocumentObjectGroupPython] P_element013  label="P_element : 002"  # scripted group (container) (typed FeaturePython)
  n = 1
  ref = P_element
FEATURE [App::DocumentObjectGroupPython] G4_P  # scripted group (container) (typed FeaturePython)
  Dunit = g/cm3
  Dvalue = 2.2
  Group = -> [P_element013]
  conduct = 2
  density = 1
  expand = 3
  formula = P
  name = G4_P
  specific = 4
FEATURE [App::DocumentObjectGroupPython] S_element023  label="S_element : 007"  # scripted group (container) (typed FeaturePython)
  n = 1
  ref = S_element
FEATURE [App::DocumentObjectGroupPython] G4_S  # scripted group (container) (typed FeaturePython)
  Dunit = g/cm3
  Dvalue = 2
  Group = -> [S_element023]
  conduct = 2
  density = 1
  expand = 3
  formula = S
  name = G4_S
  specific = 4
FEATURE [App::DocumentObjectGroupPython] Cl_element029  label="Cl_element : 015"  # scripted group (container) (typed FeaturePython)
  n = 1
  ref = Cl_element
FEATURE [App::DocumentObjectGroupPython] G4_Cl  # scripted group (container) (typed FeaturePython)
  Dunit = g/cm3
  Dvalue = 0.00299473
  Group = -> [Cl_element029]
  conduct = 2
  density = 1
  expand = 3
  formula = Cl
  name = G4_Cl
  specific = 4
FEATURE [App::DocumentObjectGroupPython] Ar_element002  label="Ar_element : 1"  # scripted group (container) (typed FeaturePython)
  n = 1
  ref = Ar_element
FEATURE [App::DocumentObjectGroupPython] G4_Ar  # scripted group (container) (typed FeaturePython)
  Dunit = g/cm3
  Dvalue = 0.00166201
  Group = -> [Ar_element002]
  conduct = 2
  density = 1
  expand = 3
  formula = Ar
  name = G4_Ar
  specific = 4
FEATURE [App::DocumentObjectGroupPython] K_element013  label="K_element : 003"  # scripted group (container) (typed FeaturePython)
  n = 1
  ref = K_element
FEATURE [App::DocumentObjectGroupPython] G4_K  # scripted group (container) (typed FeaturePython)
  Dunit = g/cm3
  Dvalue = 0.862
  Group = -> [K_element013]
  conduct = 2
  density = 1
  expand = 3
  formula = K
  name = G4_K
  specific = 4
FEATURE [App::DocumentObjectGroupPython] Ca_element014  label="Ca_element : 007"  # scripted group (container) (typed FeaturePython)
  n = 1
  ref = Ca_element
FEATURE [App::DocumentObjectGroupPython] G4_Ca  # scripted group (container) (typed FeaturePython)
  Dunit = g/cm3
  Dvalue = 1.55
  Group = -> [Ca_element014]
  conduct = 2
  density = 1
  expand = 3
  formula = Ca
  name = G4_Ca
  specific = 4
FEATURE [App::DocumentObjectGroupPython] Sc_element001  label="Sc_element : 1"  # scripted group (container) (typed FeaturePython)
  n = 1
  ref = Sc_element
FEATURE [App::DocumentObjectGroupPython] G4_Sc  # scripted group (container) (typed FeaturePython)
  Dunit = g/cm3
  Dvalue = 2.989
  Group = -> [Sc_element001]
  conduct = 2
  density = 1
  expand = 3
  formula = Sc
  name = G4_Sc
  specific = 4
FEATURE [App::DocumentObjectGroupPython] Ti_element004  label="Ti_element : 002"  # scripted group (container) (typed FeaturePython)
  n = 1
  ref = Ti_element
FEATURE [App::DocumentObjectGroupPython] G4_Ti  # scripted group (container) (typed FeaturePython)
  Dunit = g/cm3
  Dvalue = 4.54
  Group = -> [Ti_element004]
  conduct = 2
  density = 1
  expand = 3
  formula = Ti
  name = G4_Ti
  specific = 4
FEATURE [App::DocumentObjectGroupPython] V_element001  label="V_element : 1"  # scripted group (container) (typed FeaturePython)
  n = 1
  ref = V_element
FEATURE [App::DocumentObjectGroupPython] G4_V  # scripted group (container) (typed FeaturePython)
  Dunit = g/cm3
  Dvalue = 6.11
  Group = -> [V_element001]
  conduct = 2
  density = 1
  expand = 3
  formula = V
  name = G4_V
  specific = 4
FEATURE [App::DocumentObjectGroupPython] Cr_element001  label="Cr_element : 1"  # scripted group (container) (typed FeaturePython)
  n = 1
  ref = Cr_element
FEATURE [App::DocumentObjectGroupPython] G4_Cr  # scripted group (container) (typed FeaturePython)
  Dunit = g/cm3
  Dvalue = 7.18
  Group = -> [Cr_element001]
  conduct = 2
  density = 1
  expand = 3
  formula = Cr
  name = G4_Cr
  specific = 4
FEATURE [App::DocumentObjectGroupPython] Mn_element001  label="Mn_element : 1"  # scripted group (container) (typed FeaturePython)
  n = 1
  ref = Mn_element
FEATURE [App::DocumentObjectGroupPython] G4_Mn  # scripted group (container) (typed FeaturePython)
  Dunit = g/cm3
  Dvalue = 7.44
  Group = -> [Mn_element001]
  conduct = 2
  density = 1
  expand = 3
  formula = Mn
  name = G4_Mn
  specific = 4
FEATURE [App::DocumentObjectGroupPython] Fe_element007  label="Fe_element : 004"  # scripted group (container) (typed FeaturePython)
  n = 1
  ref = Fe_element
FEATURE [App::DocumentObjectGroupPython] G4_Fe  # scripted group (container) (typed FeaturePython)
  Dunit = g/cm3
  Dvalue = 7.874
  Group = -> [Fe_element007]
  conduct = 2
  density = 1
  expand = 3
  formula = Fe
  name = G4_Fe
  specific = 4
FEATURE [App::DocumentObjectGroupPython] Co_element001  label="Co_element : 1"  # scripted group (container) (typed FeaturePython)
  n = 1
  ref = Co_element
FEATURE [App::DocumentObjectGroupPython] G4_Co  # scripted group (container) (typed FeaturePython)
  Dunit = g/cm3
  Dvalue = 8.9
  Group = -> [Co_element001]
  conduct = 2
  density = 1
  expand = 3
  formula = Co
  name = G4_Co
  specific = 4
FEATURE [App::DocumentObjectGroupPython] Ni_element001  label="Ni_element : 1"  # scripted group (container) (typed FeaturePython)
  n = 1
  ref = Ni_element
FEATURE [App::DocumentObjectGroupPython] G4_Ni  # scripted group (container) (typed FeaturePython)
  Dunit = g/cm3
  Dvalue = 8.902
  Group = -> [Ni_element001]
  conduct = 2
  density = 1
  expand = 3
  formula = Ni
  name = G4_Ni
  specific = 4
FEATURE [App::DocumentObjectGroupPython] Cu_element001  label="Cu_element : 1"  # scripted group (container) (typed FeaturePython)
  n = 1
  ref = Cu_element
FEATURE [App::DocumentObjectGroupPython] G4_Cu  # scripted group (container) (typed FeaturePython)
  Dunit = g/cm3
  Dvalue = 8.96
  Group = -> [Cu_element001]
  conduct = 2
  density = 1
  expand = 3
  formula = Cu
  name = G4_Cu
  specific = 4
FEATURE [App::DocumentObjectGroupPython] Zn_element001  label="Zn_element : 1"  # scripted group (container) (typed FeaturePython)
  n = 1
  ref = Zn_element
FEATURE [App::DocumentObjectGroupPython] G4_Zn  # scripted group (container) (typed FeaturePython)
  Dunit = g/cm3
  Dvalue = 7.133
  Group = -> [Zn_element001]
  conduct = 2
  density = 1
  expand = 3
  formula = Zn
  name = G4_Zn
  specific = 4
FEATURE [App::DocumentObjectGroupPython] Ga_element002  label="Ga_element : 002"  # scripted group (container) (typed FeaturePython)
  n = 1
  ref = Ga_element
FEATURE [App::DocumentObjectGroupPython] G4_Ga  # scripted group (container) (typed FeaturePython)
  Dunit = g/cm3
  Dvalue = 5.904
  Group = -> [Ga_element002]
  conduct = 2
  density = 1
  expand = 3
  formula = Ga
  name = G4_Ga
  specific = 4
FEATURE [App::DocumentObjectGroupPython] Ge_element002  label="Ge_element : 1"  # scripted group (container) (typed FeaturePython)
  n = 1
  ref = Ge_element
FEATURE [App::DocumentObjectGroupPython] G4_Ge  # scripted group (container) (typed FeaturePython)
  Dunit = g/cm3
  Dvalue = 5.323
  Group = -> [Ge_element002]
  conduct = 2
  density = 1
  expand = 3
  formula = Ge
  name = G4_Ge
  specific = 4
FEATURE [App::DocumentObjectGroupPython] As_element003  label="As_element : 002"  # scripted group (container) (typed FeaturePython)
  n = 1
  ref = As_element
FEATURE [App::DocumentObjectGroupPython] G4_As  # scripted group (container) (typed FeaturePython)
  Dunit = g/cm3
  Dvalue = 5.73
  Group = -> [As_element003]
  conduct = 2
  density = 1
  expand = 3
  formula = As
  name = G4_As
  specific = 4
FEATURE [App::DocumentObjectGroupPython] Se_element001  label="Se_element : 1"  # scripted group (container) (typed FeaturePython)
  n = 1
  ref = Se_element
FEATURE [App::DocumentObjectGroupPython] G4_Se  # scripted group (container) (typed FeaturePython)
  Dunit = g/cm3
  Dvalue = 4.5
  Group = -> [Se_element001]
  conduct = 2
  density = 1
  expand = 3
  formula = Se
  name = G4_Se
  specific = 4
FEATURE [App::DocumentObjectGroupPython] Br_element007  label="Br_element : 004"  # scripted group (container) (typed FeaturePython)
  n = 1
  ref = Br_element
FEATURE [App::DocumentObjectGroupPython] G4_Br  # scripted group (container) (typed FeaturePython)
  Dunit = g/cm3
  Dvalue = 0.0070721
  Group = -> [Br_element007]
  conduct = 2
  density = 1
  expand = 3
  formula = Br
  name = G4_Br
  specific = 4
FEATURE [App::DocumentObjectGroupPython] Kr_element001  label="Kr_element : 1"  # scripted group (container) (typed FeaturePython)
  n = 1
  ref = Kr_element
FEATURE [App::DocumentObjectGroupPython] G4_Kr  # scripted group (container) (typed FeaturePython)
  Dunit = g/cm3
  Dvalue = 0.00347832
  Group = -> [Kr_element001]
  conduct = 2
  density = 1
  expand = 3
  formula = Kr
  name = G4_Kr
  specific = 4
FEATURE [App::DocumentObjectGroupPython] Rb_element001  label="Rb_element : 1"  # scripted group (container) (typed FeaturePython)
  n = 1
  ref = Rb_element
FEATURE [App::DocumentObjectGroupPython] G4_Rb  # scripted group (container) (typed FeaturePython)
  Dunit = g/cm3
  Dvalue = 1.532
  Group = -> [Rb_element001]
  conduct = 2
  density = 1
  expand = 3
  formula = Rb
  name = G4_Rb
  specific = 4
FEATURE [App::DocumentObjectGroupPython] Sr_element001  label="Sr_element : 1"  # scripted group (container) (typed FeaturePython)
  n = 1
  ref = Sr_element
FEATURE [App::DocumentObjectGroupPython] G4_Sr  # scripted group (container) (typed FeaturePython)
  Dunit = g/cm3
  Dvalue = 2.54
  Group = -> [Sr_element001]
  conduct = 2
  density = 1
  expand = 3
  formula = Sr
  name = G4_Sr
  specific = 4
FEATURE [App::DocumentObjectGroupPython] Y_element001  label="Y_element : 1"  # scripted group (container) (typed FeaturePython)
  n = 1
  ref = Y_element
FEATURE [App::DocumentObjectGroupPython] G4_Y  # scripted group (container) (typed FeaturePython)
  Dunit = g/cm3
  Dvalue = 4.469
  Group = -> [Y_element001]
  conduct = 2
  density = 1
  expand = 3
  formula = Y
  name = G4_Y
  specific = 4
FEATURE [App::DocumentObjectGroupPython] Zr_element001  label="Zr_element : 1"  # scripted group (container) (typed FeaturePython)
  n = 1
  ref = Zr_element
FEATURE [App::DocumentObjectGroupPython] G4_Zr  # scripted group (container) (typed FeaturePython)
  Dunit = g/cm3
  Dvalue = 6.506
  Group = -> [Zr_element001]
  conduct = 2
  density = 1
  expand = 3
  formula = Zr
  name = G4_Zr
  specific = 4
FEATURE [App::DocumentObjectGroupPython] Nb_element001  label="Nb_element : 1"  # scripted group (container) (typed FeaturePython)
  n = 1
  ref = Nb_element
FEATURE [App::DocumentObjectGroupPython] G4_Nb  # scripted group (container) (typed FeaturePython)
  Dunit = g/cm3
  Dvalue = 8.57
  Group = -> [Nb_element001]
  conduct = 2
  density = 1
  expand = 3
  formula = Nb
  name = G4_Nb
  specific = 4
FEATURE [App::DocumentObjectGroupPython] Mo_element001  label="Mo_element : 1"  # scripted group (container) (typed FeaturePython)
  n = 1
  ref = Mo_element
FEATURE [App::DocumentObjectGroupPython] G4_Mo  # scripted group (container) (typed FeaturePython)
  Dunit = g/cm3
  Dvalue = 10.22
  Group = -> [Mo_element001]
  conduct = 2
  density = 1
  expand = 3
  formula = Mo
  name = G4_Mo
  specific = 4
FEATURE [App::DocumentObjectGroupPython] Tc_element001  label="Tc_element : 1"  # scripted group (container) (typed FeaturePython)
  n = 1
  ref = Tc_element
FEATURE [App::DocumentObjectGroupPython] G4_Tc  # scripted group (container) (typed FeaturePython)
  Dunit = g/cm3
  Dvalue = 11.5
  Group = -> [Tc_element001]
  conduct = 2
  density = 1
  expand = 3
  formula = Tc
  name = G4_Tc
  specific = 4
FEATURE [App::DocumentObjectGroupPython] Ru_element001  label="Ru_element : 1"  # scripted group (container) (typed FeaturePython)
  n = 1
  ref = Ru_element
FEATURE [App::DocumentObjectGroupPython] G4_Ru  # scripted group (container) (typed FeaturePython)
  Dunit = g/cm3
  Dvalue = 12.41
  Group = -> [Ru_element001]
  conduct = 2
  density = 1
  expand = 3
  formula = Ru
  name = G4_Ru
  specific = 4
FEATURE [App::DocumentObjectGroupPython] Rh_element001  label="Rh_element : 1"  # scripted group (container) (typed FeaturePython)
  n = 1
  ref = Rh_element
FEATURE [App::DocumentObjectGroupPython] G4_Rh  # scripted group (container) (typed FeaturePython)
  Dunit = g/cm3
  Dvalue = 12.41
  Group = -> [Rh_element001]
  conduct = 2
  density = 1
  expand = 3
  formula = Rh
  name = G4_Rh
  specific = 4
FEATURE [App::DocumentObjectGroupPython] Pd_element001  label="Pd_element : 1"  # scripted group (container) (typed FeaturePython)
  n = 1
  ref = Pd_element
FEATURE [App::DocumentObjectGroupPython] G4_Pd  # scripted group (container) (typed FeaturePython)
  Dunit = g/cm3
  Dvalue = 12.02
  Group = -> [Pd_element001]
  conduct = 2
  density = 1
  expand = 3
  formula = Pd
  name = G4_Pd
  specific = 4
FEATURE [App::DocumentObjectGroupPython] Ag_element006  label="Ag_element : 004"  # scripted group (container) (typed FeaturePython)
  n = 1
  ref = Ag_element
FEATURE [App::DocumentObjectGroupPython] G4_Ag  # scripted group (container) (typed FeaturePython)
  Dunit = g/cm3
  Dvalue = 10.5
  Group = -> [Ag_element006]
  conduct = 2
  density = 1
  expand = 3
  formula = Ag
  name = G4_Ag
  specific = 4
FEATURE [App::DocumentObjectGroupPython] Cd_element003  label="Cd_element : 003"  # scripted group (container) (typed FeaturePython)
  n = 1
  ref = Cd_element
FEATURE [App::DocumentObjectGroupPython] G4_Cd  # scripted group (container) (typed FeaturePython)
  Dunit = g/cm3
  Dvalue = 8.65
  Group = -> [Cd_element003]
  conduct = 2
  density = 1
  expand = 3
  formula = Cd
  name = G4_Cd
  specific = 4
FEATURE [App::DocumentObjectGroupPython] In_element001  label="In_element : 1"  # scripted group (container) (typed FeaturePython)
  n = 1
  ref = In_element
FEATURE [App::DocumentObjectGroupPython] G4_In  # scripted group (container) (typed FeaturePython)
  Dunit = g/cm3
  Dvalue = 7.31
  Group = -> [In_element001]
  conduct = 2
  density = 1
  expand = 3
  formula = In
  name = G4_In
  specific = 4
FEATURE [App::DocumentObjectGroupPython] Sn_element001  label="Sn_element : 1"  # scripted group (container) (typed FeaturePython)
  n = 1
  ref = Sn_element
FEATURE [App::DocumentObjectGroupPython] G4_Sn  # scripted group (container) (typed FeaturePython)
  Dunit = g/cm3
  Dvalue = 7.31
  Group = -> [Sn_element001]
  conduct = 2
  density = 1
  expand = 3
  formula = Sn
  name = G4_Sn
  specific = 4
FEATURE [App::DocumentObjectGroupPython] Sb_element001  label="Sb_element : 1"  # scripted group (container) (typed FeaturePython)
  n = 1
  ref = Sb_element
FEATURE [App::DocumentObjectGroupPython] G4_Sb  # scripted group (container) (typed FeaturePython)
  Dunit = g/cm3
  Dvalue = 6.691
  Group = -> [Sb_element001]
  conduct = 2
  density = 1
  expand = 3
  formula = Sb
  name = G4_Sb
  specific = 4
FEATURE [App::DocumentObjectGroupPython] Te_element002  label="Te_element : 002"  # scripted group (container) (typed FeaturePython)
  n = 1
  ref = Te_element
FEATURE [App::DocumentObjectGroupPython] G4_Te  # scripted group (container) (typed FeaturePython)
  Dunit = g/cm3
  Dvalue = 6.24
  Group = -> [Te_element002]
  conduct = 2
  density = 1
  expand = 3
  formula = Te
  name = G4_Te
  specific = 4
FEATURE [App::DocumentObjectGroupPython] I_element010  label="I_element : 006"  # scripted group (container) (typed FeaturePython)
  n = 1
  ref = I_element
FEATURE [App::DocumentObjectGroupPython] G4_I  # scripted group (container) (typed FeaturePython)
  Dunit = g/cm3
  Dvalue = 4.93
  Group = -> [I_element010]
  conduct = 2
  density = 1
  expand = 3
  formula = I
  name = G4_I
  specific = 4
FEATURE [App::DocumentObjectGroupPython] Xe_element001  label="Xe_element : 1"  # scripted group (container) (typed FeaturePython)
  n = 1
  ref = Xe_element
FEATURE [App::DocumentObjectGroupPython] G4_Xe  # scripted group (container) (typed FeaturePython)
  Dunit = g/cm3
  Dvalue = 0.00548536
  Group = -> [Xe_element001]
  conduct = 2
  density = 1
  expand = 3
  formula = Xe
  name = G4_Xe
  specific = 4
FEATURE [App::DocumentObjectGroupPython] Cs_element003  label="Cs_element : 003"  # scripted group (container) (typed FeaturePython)
  n = 1
  ref = Cs_element
FEATURE [App::DocumentObjectGroupPython] G4_Cs  # scripted group (container) (typed FeaturePython)
  Dunit = g/cm3
  Dvalue = 1.873
  Group = -> [Cs_element003]
  conduct = 2
  density = 1
  expand = 3
  formula = Cs
  name = G4_Cs
  specific = 4
FEATURE [App::DocumentObjectGroupPython] Ba_element003  label="Ba_element : 003"  # scripted group (container) (typed FeaturePython)
  n = 1
  ref = Ba_element
FEATURE [App::DocumentObjectGroupPython] G4_Ba  # scripted group (container) (typed FeaturePython)
  Dunit = g/cm3
  Dvalue = 3.5
  Group = -> [Ba_element003]
  conduct = 2
  density = 1
  expand = 3
  formula = Ba
  name = G4_Ba
  specific = 4
FEATURE [App::DocumentObjectGroupPython] La_element003  label="La_element : 003"  # scripted group (container) (typed FeaturePython)
  n = 1
  ref = La_element
FEATURE [App::DocumentObjectGroupPython] G4_La  # scripted group (container) (typed FeaturePython)
  Dunit = g/cm3
  Dvalue = 6.154
  Group = -> [La_element003]
  conduct = 2
  density = 1
  expand = 3
  formula = La
  name = G4_La
  specific = 4
FEATURE [App::DocumentObjectGroupPython] Ce_element002  label="Ce_element : 1"  # scripted group (container) (typed FeaturePython)
  n = 1
  ref = Ce_element
FEATURE [App::DocumentObjectGroupPython] G4_Ce  # scripted group (container) (typed FeaturePython)
  Dunit = g/cm3
  Dvalue = 6.657
  Group = -> [Ce_element002]
  conduct = 2
  density = 1
  expand = 3
  formula = Ce
  name = G4_Ce
  specific = 4
FEATURE [App::DocumentObjectGroupPython] Pr_element001  label="Pr_element : 1"  # scripted group (container) (typed FeaturePython)
  n = 1
  ref = Pr_element
FEATURE [App::DocumentObjectGroupPython] G4_Pr  # scripted group (container) (typed FeaturePython)
  Dunit = g/cm3
  Dvalue = 6.71
  Group = -> [Pr_element001]
  conduct = 2
  density = 1
  expand = 3
  formula = Pr
  name = G4_Pr
  specific = 4
FEATURE [App::DocumentObjectGroupPython] Nd_element001  label="Nd_element : 1"  # scripted group (container) (typed FeaturePython)
  n = 1
  ref = Nd_element
FEATURE [App::DocumentObjectGroupPython] G4_Nd  # scripted group (container) (typed FeaturePython)
  Dunit = g/cm3
  Dvalue = 6.9
  Group = -> [Nd_element001]
  conduct = 2
  density = 1
  expand = 3
  formula = Nd
  name = G4_Nd
  specific = 4
FEATURE [App::DocumentObjectGroupPython] Pm_element001  label="Pm_element : 1"  # scripted group (container) (typed FeaturePython)
  n = 1
  ref = Pm_element
FEATURE [App::DocumentObjectGroupPython] G4_Pm  # scripted group (container) (typed FeaturePython)
  Dunit = g/cm3
  Dvalue = 7.22
  Group = -> [Pm_element001]
  conduct = 2
  density = 1
  expand = 3
  formula = Pm
  name = G4_Pm
  specific = 4
FEATURE [App::DocumentObjectGroupPython] Sm_element001  label="Sm_element : 1"  # scripted group (container) (typed FeaturePython)
  n = 1
  ref = Sm_element
FEATURE [App::DocumentObjectGroupPython] G4_Sm  # scripted group (container) (typed FeaturePython)
  Dunit = g/cm3
  Dvalue = 7.46
  Group = -> [Sm_element001]
  conduct = 2
  density = 1
  expand = 3
  formula = Sm
  name = G4_Sm
  specific = 4
FEATURE [App::DocumentObjectGroupPython] Eu_element001  label="Eu_element : 1"  # scripted group (container) (typed FeaturePython)
  n = 1
  ref = Eu_element
FEATURE [App::DocumentObjectGroupPython] G4_Eu  # scripted group (container) (typed FeaturePython)
  Dunit = g/cm3
  Dvalue = 5.243
  Group = -> [Eu_element001]
  conduct = 2
  density = 1
  expand = 3
  formula = Eu
  name = G4_Eu
  specific = 4
FEATURE [App::DocumentObjectGroupPython] Gd_element002  label="Gd_element : 1"  # scripted group (container) (typed FeaturePython)
  n = 1
  ref = Gd_element
FEATURE [App::DocumentObjectGroupPython] G4_Gd  # scripted group (container) (typed FeaturePython)
  Dunit = g/cm3
  Dvalue = 7.9004
  Group = -> [Gd_element002]
  conduct = 2
  density = 1
  expand = 3
  formula = Gd
  name = G4_Gd
  specific = 4
FEATURE [App::DocumentObjectGroupPython] Tb_element001  label="Tb_element : 1"  # scripted group (container) (typed FeaturePython)
  n = 1
  ref = Tb_element
FEATURE [App::DocumentObjectGroupPython] G4_Tb  # scripted group (container) (typed FeaturePython)
  Dunit = g/cm3
  Dvalue = 8.229
  Group = -> [Tb_element001]
  conduct = 2
  density = 1
  expand = 3
  formula = Tb
  name = G4_Tb
  specific = 4
FEATURE [App::DocumentObjectGroupPython] Dy_element001  label="Dy_element : 1"  # scripted group (container) (typed FeaturePython)
  n = 1
  ref = Dy_element
FEATURE [App::DocumentObjectGroupPython] G4_Dy  # scripted group (container) (typed FeaturePython)
  Dunit = g/cm3
  Dvalue = 8.55
  Group = -> [Dy_element001]
  conduct = 2
  density = 1
  expand = 3
  formula = Dy
  name = G4_Dy
  specific = 4
FEATURE [App::DocumentObjectGroupPython] Ho_element001  label="Ho_element : 1"  # scripted group (container) (typed FeaturePython)
  n = 1
  ref = Ho_element
FEATURE [App::DocumentObjectGroupPython] G4_Ho  # scripted group (container) (typed FeaturePython)
  Dunit = g/cm3
  Dvalue = 8.795
  Group = -> [Ho_element001]
  conduct = 2
  density = 1
  expand = 3
  formula = Ho
  name = G4_Ho
  specific = 4
FEATURE [App::DocumentObjectGroupPython] Er_element001  label="Er_element : 1"  # scripted group (container) (typed FeaturePython)
  n = 1
  ref = Er_element
FEATURE [App::DocumentObjectGroupPython] G4_Er  # scripted group (container) (typed FeaturePython)
  Dunit = g/cm3
  Dvalue = 9.066
  Group = -> [Er_element001]
  conduct = 2
  density = 1
  expand = 3
  formula = Er
  name = G4_Er
  specific = 4
FEATURE [App::DocumentObjectGroupPython] Tm_element001  label="Tm_element : 1"  # scripted group (container) (typed FeaturePython)
  n = 1
  ref = Tm_element
FEATURE [App::DocumentObjectGroupPython] G4_Tm  # scripted group (container) (typed FeaturePython)
  Dunit = g/cm3
  Dvalue = 9.321
  Group = -> [Tm_element001]
  conduct = 2
  density = 1
  expand = 3
  formula = Tm
  name = G4_Tm
  specific = 4
FEATURE [App::DocumentObjectGroupPython] Yb_element001  label="Yb_element : 1"  # scripted group (container) (typed FeaturePython)
  n = 1
  ref = Yb_element
FEATURE [App::DocumentObjectGroupPython] G4_Yb  # scripted group (container) (typed FeaturePython)
  Dunit = g/cm3
  Dvalue = 6.73
  Group = -> [Yb_element001]
  conduct = 2
  density = 1
  expand = 3
  formula = Yb
  name = G4_Yb
  specific = 4
FEATURE [App::DocumentObjectGroupPython] Lu_element001  label="Lu_element : 1"  # scripted group (container) (typed FeaturePython)
  n = 1
  ref = Lu_element
FEATURE [App::DocumentObjectGroupPython] G4_Lu  # scripted group (container) (typed FeaturePython)
  Dunit = g/cm3
  Dvalue = 9.84
  Group = -> [Lu_element001]
  conduct = 2
  density = 1
  expand = 3
  formula = Lu
  name = G4_Lu
  specific = 4
FEATURE [App::DocumentObjectGroupPython] Hf_element001  label="Hf_element : 1"  # scripted group (container) (typed FeaturePython)
  n = 1
  ref = Hf_element
FEATURE [App::DocumentObjectGroupPython] G4_Hf  # scripted group (container) (typed FeaturePython)
  Dunit = g/cm3
  Dvalue = 13.31
  Group = -> [Hf_element001]
  conduct = 2
  density = 1
  expand = 3
  formula = Hf
  name = G4_Hf
  specific = 4
FEATURE [App::DocumentObjectGroupPython] Ta_element001  label="Ta_element : 1"  # scripted group (container) (typed FeaturePython)
  n = 1
  ref = Ta_element
FEATURE [App::DocumentObjectGroupPython] G4_Ta  # scripted group (container) (typed FeaturePython)
  Dunit = g/cm3
  Dvalue = 16.654
  Group = -> [Ta_element001]
  conduct = 2
  density = 1
  expand = 3
  formula = Ta
  name = G4_Ta
  specific = 4
FEATURE [App::DocumentObjectGroupPython] W_element004  label="W_element : 004"  # scripted group (container) (typed FeaturePython)
  n = 1
  ref = W_element
FEATURE [App::DocumentObjectGroupPython] G4_W  # scripted group (container) (typed FeaturePython)
  Dunit = g/cm3
  Dvalue = 19.3
  Group = -> [W_element004]
  conduct = 2
  density = 1
  expand = 3
  formula = W
  name = G4_W
  specific = 4
FEATURE [App::DocumentObjectGroupPython] Re_element001  label="Re_element : 1"  # scripted group (container) (typed FeaturePython)
  n = 1
  ref = Re_element
FEATURE [App::DocumentObjectGroupPython] G4_Re  # scripted group (container) (typed FeaturePython)
  Dunit = g/cm3
  Dvalue = 21.02
  Group = -> [Re_element001]
  conduct = 2
  density = 1
  expand = 3
  formula = Re
  name = G4_Re
  specific = 4
FEATURE [App::DocumentObjectGroupPython] Os_element001  label="Os_element : 1"  # scripted group (container) (typed FeaturePython)
  n = 1
  ref = Os_element
FEATURE [App::DocumentObjectGroupPython] G4_Os  # scripted group (container) (typed FeaturePython)
  Dunit = g/cm3
  Dvalue = 22.57
  Group = -> [Os_element001]
  conduct = 2
  density = 1
  expand = 3
  formula = Os
  name = G4_Os
  specific = 4
FEATURE [App::DocumentObjectGroupPython] Ir_element001  label="Ir_element : 1"  # scripted group (container) (typed FeaturePython)
  n = 1
  ref = Ir_element
FEATURE [App::DocumentObjectGroupPython] G4_Ir  # scripted group (container) (typed FeaturePython)
  Dunit = g/cm3
  Dvalue = 22.42
  Group = -> [Ir_element001]
  conduct = 2
  density = 1
  expand = 3
  formula = Ir
  name = G4_Ir
  specific = 4
FEATURE [App::DocumentObjectGroupPython] Pt_element001  label="Pt_element : 1"  # scripted group (container) (typed FeaturePython)
  n = 1
  ref = Pt_element
FEATURE [App::DocumentObjectGroupPython] G4_Pt  # scripted group (container) (typed FeaturePython)
  Dunit = g/cm3
  Dvalue = 21.45
  Group = -> [Pt_element001]
  conduct = 2
  density = 1
  expand = 3
  formula = Pt
  name = G4_Pt
  specific = 4
FEATURE [App::DocumentObjectGroupPython] Au_element001  label="Au_element : 1"  # scripted group (container) (typed FeaturePython)
  n = 1
  ref = Au_element
FEATURE [App::DocumentObjectGroupPython] G4_Au  # scripted group (container) (typed FeaturePython)
  Dunit = g/cm3
  Dvalue = 19.32
  Group = -> [Au_element001]
  conduct = 2
  density = 1
  expand = 3
  formula = Au
  name = G4_Au
  specific = 4
FEATURE [App::DocumentObjectGroupPython] Hg_element002  label="Hg_element : 002"  # scripted group (container) (typed FeaturePython)
  n = 1
  ref = Hg_element
FEATURE [App::DocumentObjectGroupPython] G4_Hg  # scripted group (container) (typed FeaturePython)
  Dunit = g/cm3
  Dvalue = 13.546
  Group = -> [Hg_element002]
  conduct = 2
  density = 1
  expand = 3
  formula = Hg
  name = G4_Hg
  specific = 4
FEATURE [App::DocumentObjectGroupPython] Tl_element002  label="Tl_element : 002"  # scripted group (container) (typed FeaturePython)
  n = 1
  ref = Tl_element
FEATURE [App::DocumentObjectGroupPython] G4_Tl  # scripted group (container) (typed FeaturePython)
  Dunit = g/cm3
  Dvalue = 11.72
  Group = -> [Tl_element002]
  conduct = 2
  density = 1
  expand = 3
  formula = Tl
  name = G4_Tl
  specific = 4
FEATURE [App::DocumentObjectGroupPython] Pb_element003  label="Pb_element : 1"  # scripted group (container) (typed FeaturePython)
  n = 1
  ref = Pb_element
FEATURE [App::DocumentObjectGroupPython] G4_Pb  # scripted group (container) (typed FeaturePython)
  Dunit = g/cm3
  Dvalue = 11.35
  Group = -> [Pb_element003]
  conduct = 2
  density = 1
  expand = 3
  formula = Pb
  name = G4_Pb
  specific = 4
FEATURE [App::DocumentObjectGroupPython] Bi_element002  label="Bi_element : 1"  # scripted group (container) (typed FeaturePython)
  n = 1
  ref = Bi_element
FEATURE [App::DocumentObjectGroupPython] G4_Bi  # scripted group (container) (typed FeaturePython)
  Dunit = g/cm3
  Dvalue = 9.747
  Group = -> [Bi_element002]
  conduct = 2
  density = 1
  expand = 3
  formula = Bi
  name = G4_Bi
  specific = 4
FEATURE [App::DocumentObjectGroupPython] Po_element001  label="Po_element : 1"  # scripted group (container) (typed FeaturePython)
  n = 1
  ref = Po_element
FEATURE [App::DocumentObjectGroupPython] G4_Po  # scripted group (container) (typed FeaturePython)
  Dunit = g/cm3
  Dvalue = 9.32
  Group = -> [Po_element001]
  conduct = 2
  density = 1
  expand = 3
  formula = Po
  name = G4_Po
  specific = 4
FEATURE [App::DocumentObjectGroupPython] At_element001  label="At_element : 1"  # scripted group (container) (typed FeaturePython)
  n = 1
  ref = At_element
FEATURE [App::DocumentObjectGroupPython] G4_At  # scripted group (container) (typed FeaturePython)
  Dunit = g/cm3
  Dvalue = 9.32
  Group = -> [At_element001]
  conduct = 2
  density = 1
  expand = 3
  formula = At
  name = G4_At
  specific = 4
FEATURE [App::DocumentObjectGroupPython] Rn_element001  label="Rn_element : 1"  # scripted group (container) (typed FeaturePython)
  n = 1
  ref = Rn_element
FEATURE [App::DocumentObjectGroupPython] G4_Rn  # scripted group (container) (typed FeaturePython)
  Dunit = g/cm3
  Dvalue = 0.00900662
  Group = -> [Rn_element001]
  conduct = 2
  density = 1
  expand = 3
  formula = Rn
  name = G4_Rn
  specific = 4
FEATURE [App::DocumentObjectGroupPython] Fr_element001  label="Fr_element : 1"  # scripted group (container) (typed FeaturePython)
  n = 1
  ref = Fr_element
FEATURE [App::DocumentObjectGroupPython] G4_Fr  # scripted group (container) (typed FeaturePython)
  Dunit = g/cm3
  Dvalue = 1
  Group = -> [Fr_element001]
  conduct = 2
  density = 1
  expand = 3
  formula = Fr
  name = G4_Fr
  specific = 4
FEATURE [App::DocumentObjectGroupPython] Ra_element001  label="Ra_element : 1"  # scripted group (container) (typed FeaturePython)
  n = 1
  ref = Ra_element
FEATURE [App::DocumentObjectGroupPython] G4_Ra  # scripted group (container) (typed FeaturePython)
  Dunit = g/cm3
  Dvalue = 5
  Group = -> [Ra_element001]
  conduct = 2
  density = 1
  expand = 3
  formula = Ra
  name = G4_Ra
  specific = 4
FEATURE [App::DocumentObjectGroupPython] Ac_element001  label="Ac_element : 1"  # scripted group (container) (typed FeaturePython)
  n = 1
  ref = Ac_element
FEATURE [App::DocumentObjectGroupPython] G4_Ac  # scripted group (container) (typed FeaturePython)
  Dunit = g/cm3
  Dvalue = 10.07
  Group = -> [Ac_element001]
  conduct = 2
  density = 1
  expand = 3
  formula = Ac
  name = G4_Ac
  specific = 4
FEATURE [App::DocumentObjectGroupPython] Th_element001  label="Th_element : 1"  # scripted group (container) (typed FeaturePython)
  n = 1
  ref = Th_element
FEATURE [App::DocumentObjectGroupPython] G4_Th  # scripted group (container) (typed FeaturePython)
  Dunit = g/cm3
  Dvalue = 11.72
  Group = -> [Th_element001]
  conduct = 2
  density = 1
  expand = 3
  formula = Th
  name = G4_Th
  specific = 4
FEATURE [App::DocumentObjectGroupPython] Pa_element001  label="Pa_element : 1"  # scripted group (container) (typed FeaturePython)
  n = 1
  ref = Pa_element
FEATURE [App::DocumentObjectGroupPython] G4_Pa  # scripted group (container) (typed FeaturePython)
  Dunit = g/cm3
  Dvalue = 15.37
  Group = -> [Pa_element001]
  conduct = 2
  density = 1
  expand = 3
  formula = Pa
  name = G4_Pa
  specific = 4
FEATURE [App::DocumentObjectGroupPython] U_element004  label="U_element : 004"  # scripted group (container) (typed FeaturePython)
  n = 1
  ref = U_element
FEATURE [App::DocumentObjectGroupPython] G4_U  # scripted group (container) (typed FeaturePython)
  Dunit = g/cm3
  Dvalue = 18.95
  Group = -> [U_element004]
  conduct = 2
  density = 1
  expand = 3
  formula = U
  name = G4_U
  specific = 4
FEATURE [App::DocumentObjectGroupPython] Np_element001  label="Np_element : 1"  # scripted group (container) (typed FeaturePython)
  n = 1
  ref = Np_element
FEATURE [App::DocumentObjectGroupPython] G4_Np  # scripted group (container) (typed FeaturePython)
  Dunit = g/cm3
  Dvalue = 20.25
  Group = -> [Np_element001]
  conduct = 2
  density = 1
  expand = 3
  formula = Np
  name = G4_Np
  specific = 4
FEATURE [App::DocumentObjectGroupPython] Pu_element002  label="Pu_element : 002"  # scripted group (container) (typed FeaturePython)
  n = 1
  ref = Pu_element
FEATURE [App::DocumentObjectGroupPython] G4_Pu  # scripted group (container) (typed FeaturePython)
  Dunit = g/cm3
  Dvalue = 19.84
  Group = -> [Pu_element002]
  conduct = 2
  density = 1
  expand = 3
  formula = Pu
  name = G4_Pu
  specific = 4
FEATURE [App::DocumentObjectGroupPython] Am_element001  label="Am_element : 1"  # scripted group (container) (typed FeaturePython)
  n = 1
  ref = Am_element
FEATURE [App::DocumentObjectGroupPython] G4_Am  # scripted group (container) (typed FeaturePython)
  Dunit = g/cm3
  Dvalue = 13.67
  Group = -> [Am_element001]
  conduct = 2
  density = 1
  expand = 3
  formula = Am
  name = G4_Am
  specific = 4
FEATURE [App::DocumentObjectGroupPython] Cm_element001  label="Cm_element : 1"  # scripted group (container) (typed FeaturePython)
  n = 1
  ref = Cm_element
FEATURE [App::DocumentObjectGroupPython] G4_Cm  # scripted group (container) (typed FeaturePython)
  Dunit = g/cm3
  Dvalue = 13.51
  Group = -> [Cm_element001]
  conduct = 2
  density = 1
  expand = 3
  formula = Cm
  name = G4_Cm
  specific = 4
FEATURE [App::DocumentObjectGroupPython] Bk_element001  label="Bk_element : 1"  # scripted group (container) (typed FeaturePython)
  n = 1
  ref = Bk_element
FEATURE [App::DocumentObjectGroupPython] G4_Bk  # scripted group (container) (typed FeaturePython)
  Dunit = g/cm3
  Dvalue = 14
  Group = -> [Bk_element001]
  conduct = 2
  density = 1
  expand = 3
  formula = Bk
  name = G4_Bk
  specific = 4
FEATURE [App::DocumentObjectGroupPython] Cf_element001  label="Cf_element : 1"  # scripted group (container) (typed FeaturePython)
  n = 1
  ref = Cf_element
FEATURE [App::DocumentObjectGroupPython] G4_Cf  # scripted group (container) (typed FeaturePython)
  Dunit = g/cm3
  Dvalue = 10
  Group = -> [Cf_element001]
  conduct = 2
  density = 1
  expand = 3
  formula = Cf
  name = G4_Cf
  specific = 4
FEATURE [App::DocumentObjectGroupPython] Element  # scripted group (container) (typed FeaturePython)
  Group = -> [G4_H,G4_He,G4_Li,G4_Be,G4_B,G4_C,G4_N,G4_O,G4_F,G4_Ne,G4_Na,G4_Mg,G4_Al,G4_Si,G4_P,G4_S,G4_Cl,G4_Ar,G4_K,G4_Ca,G4_Sc,G4_Ti,G4_V,G4_Cr,G4_Mn,G4_Fe,G4_Co,G4_Ni,G4_Cu,G4_Zn,G4_Ga,G4_Ge,G4_As,G4_Se,G4_Br,G4_Kr,G4_Rb,G4_Sr,G4_Y,G4_Zr,G4_Nb,G4_Mo,G4_Tc,G4_Ru,G4_Rh,G4_Pd,G4_Ag,G4_Cd,G4_In,G4_Sn,G4_Sb,G4_Te,G4_I,G4_Xe,G4_Cs,G4_Ba,G4_La,G4_Ce,G4_Pr,G4_Nd,G4_Pm,G4_Sm,G4_Eu,G4_Gd,G4_Tb,G4_Dy,G4_Ho,G4_Er,+30 more]
FEATURE [App::DocumentObjectGroupPython] H_element114  label="H_element : 063"  # scripted group (container) (typed FeaturePython)
  n = 2
  ref = H_element
FEATURE [App::DocumentObjectGroupPython] G4_lH2  # scripted group (container) (typed FeaturePython)
  Dunit = g/cm3
  Dvalue = 0.0708
  Group = -> [H_element114]
  conduct = 2
  density = 1
  expand = 3
  formula = G4_lH2
  name = G4_lH2
  specific = 4
FEATURE [App::DocumentObjectGroupPython] N_element049  label="N_element : 022"  # scripted group (container) (typed FeaturePython)
  n = 2
  ref = N_element
FEATURE [App::DocumentObjectGroupPython] G4_lN2  # scripted group (container) (typed FeaturePython)
  Dunit = g/cm3
  Dvalue = 0.807
  Group = -> [N_element049]
  conduct = 2
  density = 1
  expand = 3
  formula = G4_lN2
  name = G4_lN2
  specific = 4
FEATURE [App::DocumentObjectGroupPython] O_element106  label="O_element : 060"  # scripted group (container) (typed FeaturePython)
  n = 2
  ref = O_element
FEATURE [App::DocumentObjectGroupPython] G4_lO2  # scripted group (container) (typed FeaturePython)
  Dunit = g/cm3
  Dvalue = 1.141
  Group = -> [O_element106]
  conduct = 2
  density = 1
  expand = 3
  formula = G4_lO2
  name = G4_lO2
  specific = 4
FEATURE [App::DocumentObjectGroupPython] Ar_element003  label="Ar_element : 002"  # scripted group (container) (typed FeaturePython)
  n = 1
  ref = Ar_element
FEATURE [App::DocumentObjectGroupPython] G4_lAr  # scripted group (container) (typed FeaturePython)
  Dunit = g/cm3
  Dvalue = 1.396
  Group = -> [Ar_element003]
  conduct = 2
  density = 1
  expand = 3
  formula = G4_lAr
  name = G4_lAr
  specific = 4
FEATURE [App::DocumentObjectGroupPython] Br_element008  label="Br_element : 005"  # scripted group (container) (typed FeaturePython)
  n = 1
  ref = Br_element
FEATURE [App::DocumentObjectGroupPython] G4_lBr  # scripted group (container) (typed FeaturePython)
  Dunit = g/cm3
  Dvalue = 3.1028
  Group = -> [Br_element008]
  conduct = 2
  density = 1
  expand = 3
  formula = G4_lBr
  name = G4_lBr
  specific = 4
FEATURE [App::DocumentObjectGroupPython] Kr_element002  label="Kr_element : 002"  # scripted group (container) (typed FeaturePython)
  n = 1
  ref = Kr_element
FEATURE [App::DocumentObjectGroupPython] G4_lKr  # scripted group (container) (typed FeaturePython)
  Dunit = g/cm3
  Dvalue = 2.418
  Group = -> [Kr_element002]
  conduct = 2
  density = 1
  expand = 3
  formula = G4_lKr
  name = G4_lKr
  specific = 4
FEATURE [App::DocumentObjectGroupPython] Xe_element002  label="Xe_element : 002"  # scripted group (container) (typed FeaturePython)
  n = 1
  ref = Xe_element
FEATURE [App::DocumentObjectGroupPython] G4_lXe  # scripted group (container) (typed FeaturePython)
  Dunit = g/cm3
  Dvalue = 2.953
  Group = -> [Xe_element002]
  conduct = 2
  density = 1
  expand = 3
  formula = G4_lXe
  name = G4_lXe
  specific = 4
FEATURE [App::DocumentObjectGroupPython] O_element107  label="O_element : 061"  # scripted group (container) (typed FeaturePython)
  n = 4
  ref = O_element
FEATURE [App::DocumentObjectGroupPython] Pb_element004  label="Pb_element : 002"  # scripted group (container) (typed FeaturePython)
  n = 1
  ref = Pb_element
FEATURE [App::DocumentObjectGroupPython] W_element005  label="W_element : 005"  # scripted group (container) (typed FeaturePython)
  n = 1
  ref = W_element
FEATURE [App::DocumentObjectGroupPython] G4_PbWO4  # scripted group (container) (typed FeaturePython)
  Dunit = g/cm3
  Dvalue = 8.28
  Group = -> [O_element107,Pb_element004,W_element005]
  conduct = 2
  density = 1
  expand = 3
  formula = G4_PbWO4
  name = G4_PbWO4
  specific = 4
FEATURE [App::DocumentObjectGroupPython] H_element115  label="H_element : 064"  # scripted group (container) (typed FeaturePython)
  n = 1
  ref = H_element
FEATURE [App::DocumentObjectGroupPython] G4_Galactic  # scripted group (container) (typed FeaturePython)
  Dunit = g/cm3
  Dvalue = 0
  Group = -> [H_element115]
  conduct = 2
  density = 1
  expand = 3
  formula = G4_Galactic
  name = G4_Galactic
  specific = 4
FEATURE [App::DocumentObjectGroupPython] C_element125  label="C_element : 071"  # scripted group (container) (typed FeaturePython)
  n = 1
  ref = C_element
FEATURE [App::DocumentObjectGroupPython] G4_GRAPHITE_POROUS  # scripted group (container) (typed FeaturePython)
  Dunit = g/cm3
  Dvalue = 1.7
  Group = -> [C_element125]
  conduct = 2
  density = 1
  expand = 3
  formula = G4_GRAPHITE_POROUS
  name = G4_GRAPHITE_POROUS
  specific = 4
FEATURE [App::DocumentObjectGroupPython] H_element116  label="H_element : 0.150"  # scripted group (container) (typed FeaturePython)
  n = 0.080538
FEATURE [App::DocumentObjectGroupPython] C_element126  label="C_element : 0.600"  # scripted group (container) (typed FeaturePython)
  n = 0.599848
FEATURE [App::DocumentObjectGroupPython] O_element108  label="O_element : 0.320"  # scripted group (container) (typed FeaturePython)
  n = 0.319614
FEATURE [App::DocumentObjectGroupPython] G4_LUCITE  # scripted group (container) (typed FeaturePython)
  Dunit = g/cm3
  Dvalue = 1.19
  Group = -> [H_element116,C_element126,O_element108]
  conduct = 2
  density = 1
  expand = 3
  formula = G4_LUCITE
  name = G4_LUCITE
  specific = 4
FEATURE [App::DocumentObjectGroupPython] Cu_element002  label="Cu_element : 62"  # scripted group (container) (typed FeaturePython)
  n = 62
  ref = Cu_element
FEATURE [App::DocumentObjectGroupPython] Zn_element002  label="Zn_element : 35"  # scripted group (container) (typed FeaturePython)
  n = 35
  ref = Zn_element
FEATURE [App::DocumentObjectGroupPython] Pb_element005  label="Pb_element : 3"  # scripted group (container) (typed FeaturePython)
  n = 3
  ref = Pb_element
FEATURE [App::DocumentObjectGroupPython] G4_BRASS  # scripted group (container) (typed FeaturePython)
  Dunit = g/cm3
  Dvalue = 8.52
  Group = -> [Cu_element002,Zn_element002,Pb_element005]
  conduct = 2
  density = 1
  expand = 3
  formula = G4_BRASS
  name = G4_BRASS
  specific = 4
FEATURE [App::DocumentObjectGroupPython] Cu_element003  label="Cu_element : 89"  # scripted group (container) (typed FeaturePython)
  n = 89
  ref = Cu_element
FEATURE [App::DocumentObjectGroupPython] Zn_element003  label="Zn_element : 9"  # scripted group (container) (typed FeaturePython)
  n = 9
  ref = Zn_element
FEATURE [App::DocumentObjectGroupPython] Pb_element006  label="Pb_element : 2"  # scripted group (container) (typed FeaturePython)
  n = 2
  ref = Pb_element
FEATURE [App::DocumentObjectGroupPython] G4_BRONZE  # scripted group (container) (typed FeaturePython)
  Dunit = g/cm3
  Dvalue = 8.82
  Group = -> [Cu_element003,Zn_element003,Pb_element006]
  conduct = 2
  density = 1
  expand = 3
  formula = G4_BRONZE
  name = G4_BRONZE
  specific = 4
FEATURE [App::DocumentObjectGroupPython] Fe_element008  label="Fe_element : 74"  # scripted group (container) (typed FeaturePython)
  n = 74
  ref = Fe_element
FEATURE [App::DocumentObjectGroupPython] Cr_element002  label="Cr_element : 18"  # scripted group (container) (typed FeaturePython)
  n = 18
  ref = Cr_element
FEATURE [App::DocumentObjectGroupPython] Ni_element002  label="Ni_element : 8"  # scripted group (container) (typed FeaturePython)
  n = 8
  ref = Ni_element
FEATURE [App::DocumentObjectGroupPython] G4_STAINLESS_STEEL  label="G4_STAINLESS-STEEL"  # scripted group (container) (typed FeaturePython)
  Dunit = g/cm3
  Dvalue = 8
  Group = -> [Fe_element008,Cr_element002,Ni_element002]
  conduct = 2
  density = 1
  expand = 3
  formula = G4_STAINLESS-STEEL
  name = G4_STAINLESS-STEEL
  specific = 4
FEATURE [App::DocumentObjectGroupPython] H_element117  label="H_element : 065"  # scripted group (container) (typed FeaturePython)
  n = 18
  ref = H_element
FEATURE [App::DocumentObjectGroupPython] C_element127  label="C_element : 072"  # scripted group (container) (typed FeaturePython)
  n = 12
  ref = C_element
FEATURE [App::DocumentObjectGroupPython] O_element109  label="O_element : 062"  # scripted group (container) (typed FeaturePython)
  n = 7
  ref = O_element
FEATURE [App::DocumentObjectGroupPython] G4_CR39  # scripted group (container) (typed FeaturePython)
  Dunit = g/cm3
  Dvalue = 1.32
  Group = -> [H_element117,C_element127,O_element109]
  conduct = 2
  density = 1
  expand = 3
  formula = G4_CR39
  name = G4_CR39
  specific = 4
FEATURE [App::DocumentObjectGroupPython] H_element118  label="H_element : 38"  # scripted group (container) (typed FeaturePython)
  n = 38
  ref = H_element
FEATURE [App::DocumentObjectGroupPython] C_element128  label="C_element : 073"  # scripted group (container) (typed FeaturePython)
  n = 18
  ref = C_element
FEATURE [App::DocumentObjectGroupPython] O_element110  label="O_element : 063"  # scripted group (container) (typed FeaturePython)
  n = 1
  ref = O_element
FEATURE [App::DocumentObjectGroupPython] G4_OCTADECANOL  # scripted group (container) (typed FeaturePython)
  Dunit = g/cm3
  Dvalue = 0.812
  Group = -> [H_element118,C_element128,O_element110]
  conduct = 2
  density = 1
  expand = 3
  formula = G4_OCTADECANOL
  name = G4_OCTADECANOL
  specific = 4
FEATURE [App::DocumentObjectGroupPython] HEP  # scripted group (container) (typed FeaturePython)
  Group = -> [G4_lH2,G4_lN2,G4_lO2,G4_lAr,G4_lBr,G4_lKr,G4_lXe,G4_PbWO4,G4_Galactic,G4_GRAPHITE_POROUS,G4_LUCITE,G4_BRASS,G4_BRONZE,G4_STAINLESS_STEEL,G4_CR39,G4_OCTADECANOL]
FEATURE [App::DocumentObjectGroupPython] C_element129  label="C_element : 074"  # scripted group (container) (typed FeaturePython)
  n = 14
  ref = C_element
FEATURE [App::DocumentObjectGroupPython] H_element119  label="H_element : 066"  # scripted group (container) (typed FeaturePython)
  n = 10
  ref = H_element
FEATURE [App::DocumentObjectGroupPython] O_element111  label="O_element : 064"  # scripted group (container) (typed FeaturePython)
  n = 2
  ref = O_element
FEATURE [App::DocumentObjectGroupPython] N_element050  label="N_element : 023"  # scripted group (container) (typed FeaturePython)
  n = 2
  ref = N_element
FEATURE [App::DocumentObjectGroupPython] G4_KEVLAR  # scripted group (container) (typed FeaturePython)
  Dunit = g/cm3
  Dvalue = 1.44
  Group = -> [C_element129,H_element119,O_element111,N_element050]
  conduct = 2
  density = 1
  expand = 3
  formula = G4_KEVLAR
  name = G4_KEVLAR
  specific = 4
FEATURE [App::DocumentObjectGroupPython] C_element130  label="C_element : 075"  # scripted group (container) (typed FeaturePython)
  n = 10
  ref = C_element
FEATURE [App::DocumentObjectGroupPython] H_element120  label="H_element : 067"  # scripted group (container) (typed FeaturePython)
  n = 8
  ref = H_element
FEATURE [App::DocumentObjectGroupPython] O_element112  label="O_element : 065"  # scripted group (container) (typed FeaturePython)
  n = 4
  ref = O_element
FEATURE [App::DocumentObjectGroupPython] G4_DACRON  # scripted group (container) (typed FeaturePython)
  Dunit = g/cm3
  Dvalue = 1.4
  Group = -> [C_element130,H_element120,O_element112]
  conduct = 2
  density = 1
  expand = 3
  formula = G4_DACRON
  name = G4_DACRON
  specific = 4
FEATURE [App::DocumentObjectGroupPython] C_element131  label="C_element : 076"  # scripted group (container) (typed FeaturePython)
  n = 4
  ref = C_element
FEATURE [App::DocumentObjectGroupPython] H_element121  label="H_element : 068"  # scripted group (container) (typed FeaturePython)
  n = 5
  ref = H_element
FEATURE [App::DocumentObjectGroupPython] Cl_element030  label="Cl_element : 016"  # scripted group (container) (typed FeaturePython)
  n = 1
  ref = Cl_element
FEATURE [App::DocumentObjectGroupPython] G4_NEOPRENE  # scripted group (container) (typed FeaturePython)
  Dunit = g/cm3
  Dvalue = 1.23
  Group = -> [C_element131,H_element121,Cl_element030]
  conduct = 2
  density = 1
  expand = 3
  formula = G4_NEOPRENE
  name = G4_NEOPRENE
  specific = 4
FEATURE [App::DocumentObjectGroupPython] Space  # scripted group (container) (typed FeaturePython)
  Group = -> [G4_KEVLAR,G4_DACRON,G4_NEOPRENE]
FEATURE [App::DocumentObjectGroupPython] H_element122  label="H_element : 069"  # scripted group (container) (typed FeaturePython)
  n = 5
  ref = H_element
FEATURE [App::DocumentObjectGroupPython] C_element132  label="C_element : 077"  # scripted group (container) (typed FeaturePython)
  n = 4
  ref = C_element
FEATURE [App::DocumentObjectGroupPython] N_element051  label="N_element : 3"  # scripted group (container) (typed FeaturePython)
  n = 3
  ref = N_element
FEATURE [App::DocumentObjectGroupPython] O_element113  label="O_element : 066"  # scripted group (container) (typed FeaturePython)
  n = 1
  ref = O_element
FEATURE [App::DocumentObjectGroupPython] G4_CYTOSINE  # scripted group (container) (typed FeaturePython)
  Dunit = g/cm3
  Dvalue = 1.55
  Group = -> [H_element122,C_element132,N_element051,O_element113]
  conduct = 2
  density = 1
  expand = 3
  formula = G4_CYTOSINE
  name = G4_CYTOSINE
  specific = 4
FEATURE [App::DocumentObjectGroupPython] H_element123  label="H_element : 070"  # scripted group (container) (typed FeaturePython)
  n = 6
  ref = H_element
FEATURE [App::DocumentObjectGroupPython] C_element133  label="C_element : 078"  # scripted group (container) (typed FeaturePython)
  n = 5
  ref = C_element
FEATURE [App::DocumentObjectGroupPython] N_element052  label="N_element : 024"  # scripted group (container) (typed FeaturePython)
  n = 2
  ref = N_element
FEATURE [App::DocumentObjectGroupPython] O_element114  label="O_element : 067"  # scripted group (container) (typed FeaturePython)
  n = 2
  ref = O_element
FEATURE [App::DocumentObjectGroupPython] G4_THYMINE  # scripted group (container) (typed FeaturePython)
  Dunit = g/cm3
  Dvalue = 1.23
  Group = -> [H_element123,C_element133,N_element052,O_element114]
  conduct = 2
  density = 1
  expand = 3
  formula = G4_THYMINE
  name = G4_THYMINE
  specific = 4
FEATURE [App::DocumentObjectGroupPython] H_element124  label="H_element : 071"  # scripted group (container) (typed FeaturePython)
  n = 4
  ref = H_element
FEATURE [App::DocumentObjectGroupPython] C_element134  label="C_element : 079"  # scripted group (container) (typed FeaturePython)
  n = 4
  ref = C_element
FEATURE [App::DocumentObjectGroupPython] N_element053  label="N_element : 025"  # scripted group (container) (typed FeaturePython)
  n = 2
  ref = N_element
FEATURE [App::DocumentObjectGroupPython] O_element115  label="O_element : 068"  # scripted group (container) (typed FeaturePython)
  n = 2
  ref = O_element
FEATURE [App::DocumentObjectGroupPython] G4_URACIL  # scripted group (container) (typed FeaturePython)
  Dunit = g/cm3
  Dvalue = 1.32
  Group = -> [H_element124,C_element134,N_element053,O_element115]
  conduct = 2
  density = 1
  expand = 3
  formula = G4_URACIL
  name = G4_URACIL
  specific = 4
FEATURE [App::DocumentObjectGroupPython] H_element125  label="H_element : 072"  # scripted group (container) (typed FeaturePython)
  n = 4
  ref = H_element
FEATURE [App::DocumentObjectGroupPython] C_element135  label="C_element : 080"  # scripted group (container) (typed FeaturePython)
  n = 5
  ref = C_element
FEATURE [App::DocumentObjectGroupPython] N_element054  label="N_element : 026"  # scripted group (container) (typed FeaturePython)
  n = 5
  ref = N_element
FEATURE [App::DocumentObjectGroupPython] G4_DNA_ADENINE  # scripted group (container) (typed FeaturePython)
  Dunit = g/cm3
  Dvalue = 1
  Group = -> [H_element125,C_element135,N_element054]
  conduct = 2
  density = 1
  expand = 3
  formula = G4_DNA_ADENINE
  name = G4_DNA_ADENINE
  specific = 4
FEATURE [App::DocumentObjectGroupPython] H_element126  label="H_element : 073"  # scripted group (container) (typed FeaturePython)
  n = 4
  ref = H_element
FEATURE [App::DocumentObjectGroupPython] C_element136  label="C_element : 081"  # scripted group (container) (typed FeaturePython)
  n = 5
  ref = C_element
FEATURE [App::DocumentObjectGroupPython] N_element055  label="N_element : 027"  # scripted group (container) (typed FeaturePython)
  n = 5
  ref = N_element
FEATURE [App::DocumentObjectGroupPython] O_element116  label="O_element : 069"  # scripted group (container) (typed FeaturePython)
  n = 1
  ref = O_element
FEATURE [App::DocumentObjectGroupPython] G4_DNA_GUANINE  # scripted group (container) (typed FeaturePython)
  Dunit = g/cm3
  Dvalue = 1
  Group = -> [H_element126,C_element136,N_element055,O_element116]
  conduct = 2
  density = 1
  expand = 3
  formula = G4_DNA_GUANINE
  name = G4_DNA_GUANINE
  specific = 4
FEATURE [App::DocumentObjectGroupPython] H_element127  label="H_element : 074"  # scripted group (container) (typed FeaturePython)
  n = 4
  ref = H_element
FEATURE [App::DocumentObjectGroupPython] C_element137  label="C_element : 082"  # scripted group (container) (typed FeaturePython)
  n = 4
  ref = C_element
FEATURE [App::DocumentObjectGroupPython] N_element056  label="N_element : 028"  # scripted group (container) (typed FeaturePython)
  n = 3
  ref = N_element
FEATURE [App::DocumentObjectGroupPython] O_element117  label="O_element : 070"  # scripted group (container) (typed FeaturePython)
  n = 1
  ref = O_element
FEATURE [App::DocumentObjectGroupPython] G4_DNA_CYTOSINE  # scripted group (container) (typed FeaturePython)
  Dunit = g/cm3
  Dvalue = 1
  Group = -> [H_element127,C_element137,N_element056,O_element117]
  conduct = 2
  density = 1
  expand = 3
  formula = G4_DNA_CYTOSINE
  name = G4_DNA_CYTOSINE
  specific = 4
FEATURE [App::DocumentObjectGroupPython] H_element128  label="H_element : 075"  # scripted group (container) (typed FeaturePython)
  n = 5
  ref = H_element
FEATURE [App::DocumentObjectGroupPython] C_element138  label="C_element : 083"  # scripted group (container) (typed FeaturePython)
  n = 5
  ref = C_element
FEATURE [App::DocumentObjectGroupPython] N_element057  label="N_element : 029"  # scripted group (container) (typed FeaturePython)
  n = 2
  ref = N_element
FEATURE [App::DocumentObjectGroupPython] O_element118  label="O_element : 071"  # scripted group (container) (typed FeaturePython)
  n = 2
  ref = O_element
FEATURE [App::DocumentObjectGroupPython] G4_DNA_THYMINE  # scripted group (container) (typed FeaturePython)
  Dunit = g/cm3
  Dvalue = 1
  Group = -> [H_element128,C_element138,N_element057,O_element118]
  conduct = 2
  density = 1
  expand = 3
  formula = G4_DNA_THYMINE
  name = G4_DNA_THYMINE
  specific = 4
FEATURE [App::DocumentObjectGroupPython] H_element129  label="H_element : 076"  # scripted group (container) (typed FeaturePython)
  n = 3
  ref = H_element
FEATURE [App::DocumentObjectGroupPython] C_element139  label="C_element : 084"  # scripted group (container) (typed FeaturePython)
  n = 4
  ref = C_element
FEATURE [App::DocumentObjectGroupPython] N_element058  label="N_element : 030"  # scripted group (container) (typed FeaturePython)
  n = 2
  ref = N_element
FEATURE [App::DocumentObjectGroupPython] O_element119  label="O_element : 072"  # scripted group (container) (typed FeaturePython)
  n = 2
  ref = O_element
FEATURE [App::DocumentObjectGroupPython] G4_DNA_URACIL  # scripted group (container) (typed FeaturePython)
  Dunit = g/cm3
  Dvalue = 1
  Group = -> [H_element129,C_element139,N_element058,O_element119]
  conduct = 2
  density = 1
  expand = 3
  formula = G4_DNA_URACIL
  name = G4_DNA_URACIL
  specific = 4
FEATURE [App::DocumentObjectGroupPython] H_element130  label="H_element : 077"  # scripted group (container) (typed FeaturePython)
  n = 10
  ref = H_element
FEATURE [App::DocumentObjectGroupPython] C_element140  label="C_element : 085"  # scripted group (container) (typed FeaturePython)
  n = 10
  ref = C_element
FEATURE [App::DocumentObjectGroupPython] N_element059  label="N_element : 031"  # scripted group (container) (typed FeaturePython)
  n = 5
  ref = N_element
FEATURE [App::DocumentObjectGroupPython] O_element120  label="O_element : 073"  # scripted group (container) (typed FeaturePython)
  n = 4
  ref = O_element
FEATURE [App::DocumentObjectGroupPython] G4_DNA_ADENOSINE  # scripted group (container) (typed FeaturePython)
  Dunit = g/cm3
  Dvalue = 1
  Group = -> [H_element130,C_element140,N_element059,O_element120]
  conduct = 2
  density = 1
  expand = 3
  formula = G4_DNA_ADENOSINE
  name = G4_DNA_ADENOSINE
  specific = 4
FEATURE [App::DocumentObjectGroupPython] H_element131  label="H_element : 078"  # scripted group (container) (typed FeaturePython)
  n = 10
  ref = H_element
FEATURE [App::DocumentObjectGroupPython] C_element141  label="C_element : 086"  # scripted group (container) (typed FeaturePython)
  n = 10
  ref = C_element
FEATURE [App::DocumentObjectGroupPython] N_element060  label="N_element : 032"  # scripted group (container) (typed FeaturePython)
  n = 5
  ref = N_element
FEATURE [App::DocumentObjectGroupPython] O_element121  label="O_element : 074"  # scripted group (container) (typed FeaturePython)
  n = 5
  ref = O_element
FEATURE [App::DocumentObjectGroupPython] G4_DNA_GUANOSINE  # scripted group (container) (typed FeaturePython)
  Dunit = g/cm3
  Dvalue = 1
  Group = -> [H_element131,C_element141,N_element060,O_element121]
  conduct = 2
  density = 1
  expand = 3
  formula = G4_DNA_GUANOSINE
  name = G4_DNA_GUANOSINE
  specific = 4
FEATURE [App::DocumentObjectGroupPython] H_element132  label="H_element : 079"  # scripted group (container) (typed FeaturePython)
  n = 10
  ref = H_element
FEATURE [App::DocumentObjectGroupPython] C_element142  label="C_element : 087"  # scripted group (container) (typed FeaturePython)
  n = 9
  ref = C_element
FEATURE [App::DocumentObjectGroupPython] N_element061  label="N_element : 033"  # scripted group (container) (typed FeaturePython)
  n = 3
  ref = N_element
FEATURE [App::DocumentObjectGroupPython] O_element122  label="O_element : 075"  # scripted group (container) (typed FeaturePython)
  n = 5
  ref = O_element
FEATURE [App::DocumentObjectGroupPython] G4_DNA_CYTIDINE  # scripted group (container) (typed FeaturePython)
  Dunit = g/cm3
  Dvalue = 1
  Group = -> [H_element132,C_element142,N_element061,O_element122]
  conduct = 2
  density = 1
  expand = 3
  formula = G4_DNA_CYTIDINE
  name = G4_DNA_CYTIDINE
  specific = 4
FEATURE [App::DocumentObjectGroupPython] H_element133  label="H_element : 080"  # scripted group (container) (typed FeaturePython)
  n = 9
  ref = H_element
FEATURE [App::DocumentObjectGroupPython] C_element143  label="C_element : 088"  # scripted group (container) (typed FeaturePython)
  n = 9
  ref = C_element
FEATURE [App::DocumentObjectGroupPython] N_element062  label="N_element : 034"  # scripted group (container) (typed FeaturePython)
  n = 2
  ref = N_element
FEATURE [App::DocumentObjectGroupPython] O_element123  label="O_element : 076"  # scripted group (container) (typed FeaturePython)
  n = 6
  ref = O_element
FEATURE [App::DocumentObjectGroupPython] G4_DNA_URIDINE  # scripted group (container) (typed FeaturePython)
  Dunit = g/cm3
  Dvalue = 1
  Group = -> [H_element133,C_element143,N_element062,O_element123]
  conduct = 2
  density = 1
  expand = 3
  formula = G4_DNA_URIDINE
  name = G4_DNA_URIDINE
  specific = 4
FEATURE [App::DocumentObjectGroupPython] H_element134  label="H_element : 081"  # scripted group (container) (typed FeaturePython)
  n = 11
  ref = H_element
FEATURE [App::DocumentObjectGroupPython] C_element144  label="C_element : 089"  # scripted group (container) (typed FeaturePython)
  n = 10
  ref = C_element
FEATURE [App::DocumentObjectGroupPython] N_element063  label="N_element : 035"  # scripted group (container) (typed FeaturePython)
  n = 2
  ref = N_element
FEATURE [App::DocumentObjectGroupPython] O_element124  label="O_element : 077"  # scripted group (container) (typed FeaturePython)
  n = 6
  ref = O_element
FEATURE [App::DocumentObjectGroupPython] G4_DNA_METHYLURIDINE  # scripted group (container) (typed FeaturePython)
  Dunit = g/cm3
  Dvalue = 1
  Group = -> [H_element134,C_element144,N_element063,O_element124]
  conduct = 2
  density = 1
  expand = 3
  formula = G4_DNA_METHYLURIDINE
  name = G4_DNA_METHYLURIDINE
  specific = 4
FEATURE [App::DocumentObjectGroupPython] P_element014  label="P_element : 003"  # scripted group (container) (typed FeaturePython)
  n = 1
  ref = P_element
FEATURE [App::DocumentObjectGroupPython] O_element125  label="O_element : 078"  # scripted group (container) (typed FeaturePython)
  n = 3
  ref = O_element
FEATURE [App::DocumentObjectGroupPython] G4_DNA_MONOPHOSPHATE  # scripted group (container) (typed FeaturePython)
  Dunit = g/cm3
  Dvalue = 1
  Group = -> [P_element014,O_element125]
  conduct = 2
  density = 1
  expand = 3
  formula = G4_DNA_MONOPHOSPHATE
  name = G4_DNA_MONOPHOSPHATE
  specific = 4
FEATURE [App::DocumentObjectGroupPython] H_element135  label="H_element : 082"  # scripted group (container) (typed FeaturePython)
  n = 10
  ref = H_element
FEATURE [App::DocumentObjectGroupPython] C_element145  label="C_element : 090"  # scripted group (container) (typed FeaturePython)
  n = 10
  ref = C_element
FEATURE [App::DocumentObjectGroupPython] N_element064  label="N_element : 036"  # scripted group (container) (typed FeaturePython)
  n = 5
  ref = N_element
FEATURE [App::DocumentObjectGroupPython] O_element126  label="O_element : 079"  # scripted group (container) (typed FeaturePython)
  n = 7
  ref = O_element
FEATURE [App::DocumentObjectGroupPython] P_element015  label="P_element : 004"  # scripted group (container) (typed FeaturePython)
  n = 1
  ref = P_element
FEATURE [App::DocumentObjectGroupPython] G4_DNA_A  # scripted group (container) (typed FeaturePython)
  Dunit = g/cm3
  Dvalue = 1
  Group = -> [H_element135,C_element145,N_element064,O_element126,P_element015]
  conduct = 2
  density = 1
  expand = 3
  formula = G4_DNA_A
  name = G4_DNA_A
  specific = 4
FEATURE [App::DocumentObjectGroupPython] H_element136  label="H_element : 083"  # scripted group (container) (typed FeaturePython)
  n = 10
  ref = H_element
FEATURE [App::DocumentObjectGroupPython] C_element146  label="C_element : 091"  # scripted group (container) (typed FeaturePython)
  n = 10
  ref = C_element
FEATURE [App::DocumentObjectGroupPython] N_element065  label="N_element : 037"  # scripted group (container) (typed FeaturePython)
  n = 5
  ref = N_element
FEATURE [App::DocumentObjectGroupPython] O_element127  label="O_element : 8"  # scripted group (container) (typed FeaturePython)
  n = 8
  ref = O_element
FEATURE [App::DocumentObjectGroupPython] P_element016  label="P_element : 005"  # scripted group (container) (typed FeaturePython)
  n = 1
  ref = P_element
FEATURE [App::DocumentObjectGroupPython] G4_DNA_G  # scripted group (container) (typed FeaturePython)
  Dunit = g/cm3
  Dvalue = 1
  Group = -> [H_element136,C_element146,N_element065,O_element127,P_element016]
  conduct = 2
  density = 1
  expand = 3
  formula = G4_DNA_G
  name = G4_DNA_G
  specific = 4
FEATURE [App::DocumentObjectGroupPython] H_element137  label="H_element : 084"  # scripted group (container) (typed FeaturePython)
  n = 10
  ref = H_element
FEATURE [App::DocumentObjectGroupPython] C_element147  label="C_element : 092"  # scripted group (container) (typed FeaturePython)
  n = 9
  ref = C_element
FEATURE [App::DocumentObjectGroupPython] N_element066  label="N_element : 038"  # scripted group (container) (typed FeaturePython)
  n = 3
  ref = N_element
FEATURE [App::DocumentObjectGroupPython] O_element128  label="O_element : 080"  # scripted group (container) (typed FeaturePython)
  n = 8
  ref = O_element
FEATURE [App::DocumentObjectGroupPython] P_element017  label="P_element : 006"  # scripted group (container) (typed FeaturePython)
  n = 1
  ref = P_element
FEATURE [App::DocumentObjectGroupPython] G4_DNA_C  # scripted group (container) (typed FeaturePython)
  Dunit = g/cm3
  Dvalue = 1
  Group = -> [H_element137,C_element147,N_element066,O_element128,P_element017]
  conduct = 2
  density = 1
  expand = 3
  formula = G4_DNA_C
  name = G4_DNA_C
  specific = 4
FEATURE [App::DocumentObjectGroupPython] H_element138  label="H_element : 085"  # scripted group (container) (typed FeaturePython)
  n = 9
  ref = H_element
FEATURE [App::DocumentObjectGroupPython] C_element148  label="C_element : 093"  # scripted group (container) (typed FeaturePython)
  n = 9
  ref = C_element
FEATURE [App::DocumentObjectGroupPython] N_element067  label="N_element : 039"  # scripted group (container) (typed FeaturePython)
  n = 2
  ref = N_element
FEATURE [App::DocumentObjectGroupPython] O_element129  label="O_element : 9"  # scripted group (container) (typed FeaturePython)
  n = 9
  ref = O_element
FEATURE [App::DocumentObjectGroupPython] P_element018  label="P_element : 007"  # scripted group (container) (typed FeaturePython)
  n = 1
  ref = P_element
FEATURE [App::DocumentObjectGroupPython] G4_DNA_U  # scripted group (container) (typed FeaturePython)
  Dunit = g/cm3
  Dvalue = 1
  Group = -> [H_element138,C_element148,N_element067,O_element129,P_element018]
  conduct = 2
  density = 1
  expand = 3
  formula = G4_DNA_U
  name = G4_DNA_U
  specific = 4
FEATURE [App::DocumentObjectGroupPython] H_element139  label="H_element : 086"  # scripted group (container) (typed FeaturePython)
  n = 11
  ref = H_element
FEATURE [App::DocumentObjectGroupPython] C_element149  label="C_element : 094"  # scripted group (container) (typed FeaturePython)
  n = 10
  ref = C_element
FEATURE [App::DocumentObjectGroupPython] N_element068  label="N_element : 040"  # scripted group (container) (typed FeaturePython)
  n = 2
  ref = N_element
FEATURE [App::DocumentObjectGroupPython] O_element130  label="O_element : 081"  # scripted group (container) (typed FeaturePython)
  n = 9
  ref = O_element
FEATURE [App::DocumentObjectGroupPython] P_element019  label="P_element : 008"  # scripted group (container) (typed FeaturePython)
  n = 1
  ref = P_element
FEATURE [App::DocumentObjectGroupPython] G4_DNA_MU  # scripted group (container) (typed FeaturePython)
  Dunit = g/cm3
  Dvalue = 1
  Group = -> [H_element139,C_element149,N_element068,O_element130,P_element019]
  conduct = 2
  density = 1
  expand = 3
  formula = G4_DNA_MU
  name = G4_DNA_MU
  specific = 4
FEATURE [App::DocumentObjectGroupPython] BioChemical  # scripted group (container) (typed FeaturePython)
  Group = -> [G4_CYTOSINE,G4_THYMINE,G4_URACIL,G4_DNA_ADENINE,G4_DNA_GUANINE,G4_DNA_CYTOSINE,G4_DNA_THYMINE,G4_DNA_URACIL,G4_DNA_ADENOSINE,G4_DNA_GUANOSINE,G4_DNA_CYTIDINE,G4_DNA_URIDINE,G4_DNA_METHYLURIDINE,G4_DNA_MONOPHOSPHATE,G4_DNA_A,G4_DNA_G,G4_DNA_C,G4_DNA_U,G4_DNA_MU]
FEATURE [App::DocumentObjectGroupPython] G4Materials  # scripted group (container) (typed FeaturePython)
  Group = -> [NIST,Element,HEP,Space,BioChemical]
  version = 1
FEATURE [App::DocumentObjectGroupPython] Geant4  # scripted group (container) (typed FeaturePython)
  Group = -> [G4Isotopes,G4Elements,G4Materials]
FEATURE [App::DocumentObjectGroupPython] Materials  # scripted group (container) (typed FeaturePython)
  Group = -> [Geant4]
FEATURE [Part::FeaturePython] GDMLBox_WorldBox  # WARN: FeaturePython — macro-defined, semantics opaque (R4)
  lunit = 2
  material = 5
  x = 200.2
  y = 130
  z = 130
FEATURE [Part::FeaturePython] GDMLBox_Box  # WARN: FeaturePython — macro-defined, semantics opaque (R4)
  Placement = pos=(30,0,0) rot=(0,0,1;0rad)
  lunit = 2
  material = 0
  x = 10
  y = 10
  z = 10
FEATURE [Part::FeaturePython] GDMLTorus  # WARN: FeaturePython — macro-defined, semantics opaque (R4)
  Placement = pos=(30,0,0) rot=(0,1,0;1.5708rad)
  aunit = deg
  deltaphi = 360
  lunit = 2
  material = 0
  rmax = 2
  rmin = 0
  rtor = 8
  startphi = 0
FEATURE [Part::MultiFuse] Fusion
  Shapes = -> [GDMLBox_Box,GDMLTorus]
FEATURE [Part::FeaturePython] Array  # Draft array (typed FeaturePython)
  AlwaysSyncPlacement = false
  Angle = 180
  ArrayType = 1
  Axis = (0,0,1)
  Base = -> Fusion
  Center = (0,0,0)
  Count = 5
  ExpandArray = false
  Fuse = false
  IntervalAxis = (0,0,0)
  IntervalX = (50,0,0)
  IntervalY = (0,50,0)
  IntervalZ = (0,0,50)
  NumberCircles = 3
  NumberPolar = 5
  NumberX = 2
  NumberY = 2
  NumberZ = 1
  Placement = pos=(0,0,0) rot=(0,0,1;0.785398rad)
  PlacementList = 5 placements: [(0,0,0),(0,0,0),(0,0,0),(0,0,0),(0,0,0)]
  RadialDistance = 50
  ScaleList = (5) [(1,1,1),(1,1,1),(1,1,1),(1,1,1),(1,1,1)]
  Symmetry = 1
  TangentialDistance = 25
FEATURE [App::Part] Part001
  Group = -> [Array]
  Origin = -> Origin004
FEATURE [App::Part] worldVOL
  Group = -> [GDMLBox_WorldBox,Part001]
  Origin = -> Origin
